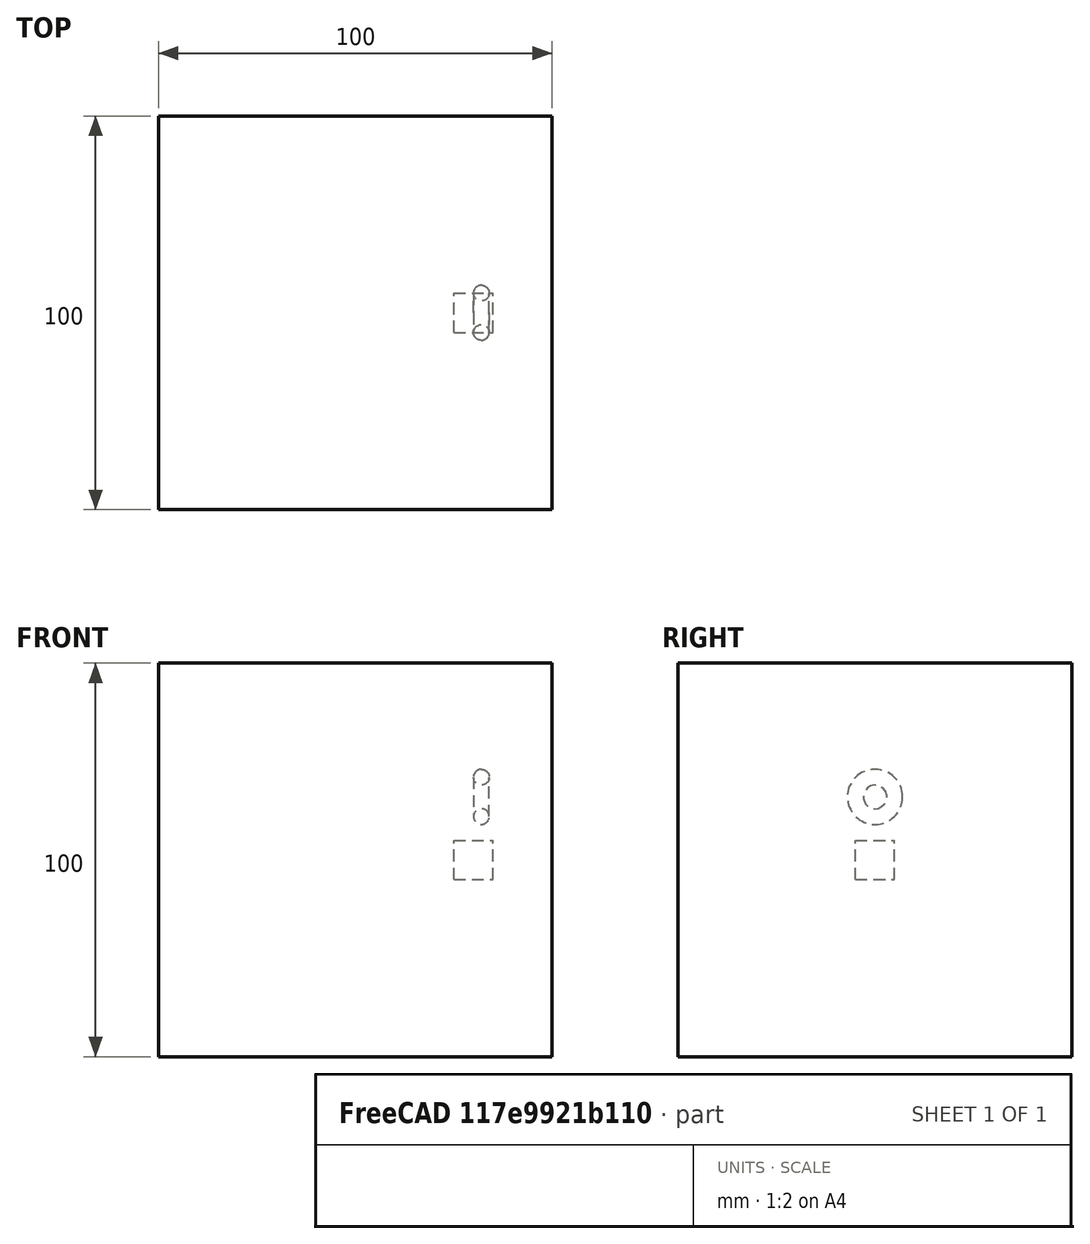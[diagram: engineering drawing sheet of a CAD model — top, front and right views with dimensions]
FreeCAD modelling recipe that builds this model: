
FCSTD DOCUMENT  (FreeCAD 0.20RUnknown)
Label: polarArray-7
License: All rights reserved
objects: App::DocumentObjectGroupPython×1251, Part::FeaturePython×4, App::Part×2, Part::MultiFuse×1
note: 4 computed .brp shape members not serialized (recipe doc carries the construction recipe); baked Part::Feature solids carry a one-line shape summary decoded from their .brp

FEATURE [App::DocumentObjectGroupPython] HALFPI  # scripted group (container) (typed FeaturePython)
  name = HALFPI
  value = pi/2.
FEATURE [App::DocumentObjectGroupPython] PI  # scripted group (container) (typed FeaturePython)
  name = PI
  value = 1.*pi
FEATURE [App::DocumentObjectGroupPython] TWOPI  # scripted group (container) (typed FeaturePython)
  name = TWOPI
  value = 2.*pi
FEATURE [App::DocumentObjectGroupPython] Constants  # scripted group (container) (typed FeaturePython)
  Group = -> [HALFPI,PI,TWOPI]
FEATURE [App::DocumentObjectGroupPython] Variables  # scripted group (container) (typed FeaturePython)
FEATURE [App::DocumentObjectGroupPython] Quantities  # scripted group (container) (typed FeaturePython)
FEATURE [App::DocumentObjectGroupPython] Isotopes  # scripted group (container) (typed FeaturePython)
FEATURE [App::DocumentObjectGroupPython] Elements  # scripted group (container) (typed FeaturePython)
FEATURE [App::DocumentObjectGroupPython] Matrix  # scripted group (container) (typed FeaturePython)
FEATURE [App::DocumentObjectGroupPython] Surfaces  # scripted group (container) (typed FeaturePython)
FEATURE [App::DocumentObjectGroupPython] Opticals  # scripted group (container) (typed FeaturePython)
  Group = -> [Matrix,Surfaces]
FEATURE [App::DocumentObjectGroupPython] G4Isotopes  # scripted group (container) (typed FeaturePython)
FEATURE [App::DocumentObjectGroupPython] H_element  # scripted group (container) (typed FeaturePython)
  Z = 1
  atom_value = 1.008
  formula = H
  name = H_element
FEATURE [App::DocumentObjectGroupPython] He_element  # scripted group (container) (typed FeaturePython)
  Z = 2
  atom_value = 4.0026
  formula = He
  name = He_element
FEATURE [App::DocumentObjectGroupPython] Li_element  # scripted group (container) (typed FeaturePython)
  Z = 3
  atom_value = 6.94
  formula = Li
  name = Li_element
FEATURE [App::DocumentObjectGroupPython] Be_element  # scripted group (container) (typed FeaturePython)
  Z = 4
  atom_value = 9.01218
  formula = Be
  name = Be_element
FEATURE [App::DocumentObjectGroupPython] B_element  # scripted group (container) (typed FeaturePython)
  Z = 5
  atom_value = 10.81
  formula = B
  name = B_element
FEATURE [App::DocumentObjectGroupPython] C_element  # scripted group (container) (typed FeaturePython)
  Z = 6
  atom_value = 12.011
  formula = C
  name = C_element
FEATURE [App::DocumentObjectGroupPython] N_element  # scripted group (container) (typed FeaturePython)
  Z = 7
  atom_value = 14.007
  formula = N
  name = N_element
FEATURE [App::DocumentObjectGroupPython] O_element  # scripted group (container) (typed FeaturePython)
  Z = 8
  atom_value = 15.999
  formula = O
  name = O_element
FEATURE [App::DocumentObjectGroupPython] F_element  # scripted group (container) (typed FeaturePython)
  Z = 9
  atom_value = 18.9984
  formula = F
  name = F_element
FEATURE [App::DocumentObjectGroupPython] Ne_element  # scripted group (container) (typed FeaturePython)
  Z = 10
  atom_value = 20.1797
  formula = Ne
  name = Ne_element
FEATURE [App::DocumentObjectGroupPython] Na_element  # scripted group (container) (typed FeaturePython)
  Z = 11
  atom_value = 22.9898
  formula = Na
  name = Na_element
FEATURE [App::DocumentObjectGroupPython] Mg_element  # scripted group (container) (typed FeaturePython)
  Z = 12
  atom_value = 24.305
  formula = Mg
  name = Mg_element
FEATURE [App::DocumentObjectGroupPython] Al_element  # scripted group (container) (typed FeaturePython)
  Z = 13
  atom_value = 26.9815
  formula = Al
  name = Al_element
FEATURE [App::DocumentObjectGroupPython] Si_element  # scripted group (container) (typed FeaturePython)
  Z = 14
  atom_value = 28.085
  formula = Si
  name = Si_element
FEATURE [App::DocumentObjectGroupPython] P_element  # scripted group (container) (typed FeaturePython)
  Z = 15
  atom_value = 30.9738
  formula = P
  name = P_element
FEATURE [App::DocumentObjectGroupPython] S_element  # scripted group (container) (typed FeaturePython)
  Z = 16
  atom_value = 32.06
  formula = S
  name = S_element
FEATURE [App::DocumentObjectGroupPython] Cl_element  # scripted group (container) (typed FeaturePython)
  Z = 17
  atom_value = 35.45
  formula = Cl
  name = Cl_element
FEATURE [App::DocumentObjectGroupPython] Ar_element  # scripted group (container) (typed FeaturePython)
  Z = 18
  atom_value = 39.95
  formula = Ar
  name = Ar_element
FEATURE [App::DocumentObjectGroupPython] K_element  # scripted group (container) (typed FeaturePython)
  Z = 19
  atom_value = 39.0983
  formula = K
  name = K_element
FEATURE [App::DocumentObjectGroupPython] Ca_element  # scripted group (container) (typed FeaturePython)
  Z = 20
  atom_value = 40.078
  formula = Ca
  name = Ca_element
FEATURE [App::DocumentObjectGroupPython] Sc_element  # scripted group (container) (typed FeaturePython)
  Z = 21
  atom_value = 44.9559
  formula = Sc
  name = Sc_element
FEATURE [App::DocumentObjectGroupPython] Ti_element  # scripted group (container) (typed FeaturePython)
  Z = 22
  atom_value = 47.867
  formula = Ti
  name = Ti_element
FEATURE [App::DocumentObjectGroupPython] V_element  # scripted group (container) (typed FeaturePython)
  Z = 23
  atom_value = 50.9415
  formula = V
  name = V_element
FEATURE [App::DocumentObjectGroupPython] Cr_element  # scripted group (container) (typed FeaturePython)
  Z = 24
  atom_value = 51.9961
  formula = Cr
  name = Cr_element
FEATURE [App::DocumentObjectGroupPython] Mn_element  # scripted group (container) (typed FeaturePython)
  Z = 25
  atom_value = 54.938
  formula = Mn
  name = Mn_element
FEATURE [App::DocumentObjectGroupPython] Fe_element  # scripted group (container) (typed FeaturePython)
  Z = 26
  atom_value = 55.845
  formula = Fe
  name = Fe_element
FEATURE [App::DocumentObjectGroupPython] Co_element  # scripted group (container) (typed FeaturePython)
  Z = 27
  atom_value = 58.9332
  formula = Co
  name = Co_element
FEATURE [App::DocumentObjectGroupPython] Ni_element  # scripted group (container) (typed FeaturePython)
  Z = 28
  atom_value = 58.6934
  formula = Ni
  name = Ni_element
FEATURE [App::DocumentObjectGroupPython] Cu_element  # scripted group (container) (typed FeaturePython)
  Z = 29
  atom_value = 63.546
  formula = Cu
  name = Cu_element
FEATURE [App::DocumentObjectGroupPython] Zn_element  # scripted group (container) (typed FeaturePython)
  Z = 30
  atom_value = 65.38
  formula = Zn
  name = Zn_element
FEATURE [App::DocumentObjectGroupPython] Ga_element  # scripted group (container) (typed FeaturePython)
  Z = 31
  atom_value = 69.723
  formula = Ga
  name = Ga_element
FEATURE [App::DocumentObjectGroupPython] Ge_element  # scripted group (container) (typed FeaturePython)
  Z = 32
  atom_value = 72.63
  formula = Ge
  name = Ge_element
FEATURE [App::DocumentObjectGroupPython] As_element  # scripted group (container) (typed FeaturePython)
  Z = 33
  atom_value = 74.9216
  formula = As
  name = As_element
FEATURE [App::DocumentObjectGroupPython] Se_element  # scripted group (container) (typed FeaturePython)
  Z = 34
  atom_value = 78.971
  formula = Se
  name = Se_element
FEATURE [App::DocumentObjectGroupPython] Br_element  # scripted group (container) (typed FeaturePython)
  Z = 35
  atom_value = 79.904
  formula = Br
  name = Br_element
FEATURE [App::DocumentObjectGroupPython] Kr_element  # scripted group (container) (typed FeaturePython)
  Z = 36
  atom_value = 83.798
  formula = Kr
  name = Kr_element
FEATURE [App::DocumentObjectGroupPython] Rb_element  # scripted group (container) (typed FeaturePython)
  Z = 37
  atom_value = 85.4678
  formula = Rb
  name = Rb_element
FEATURE [App::DocumentObjectGroupPython] Sr_element  # scripted group (container) (typed FeaturePython)
  Z = 38
  atom_value = 87.62
  formula = Sr
  name = Sr_element
FEATURE [App::DocumentObjectGroupPython] Y_element  # scripted group (container) (typed FeaturePython)
  Z = 39
  atom_value = 88.9058
  formula = Y
  name = Y_element
FEATURE [App::DocumentObjectGroupPython] Zr_element  # scripted group (container) (typed FeaturePython)
  Z = 40
  atom_value = 91.224
  formula = Zr
  name = Zr_element
FEATURE [App::DocumentObjectGroupPython] Nb_element  # scripted group (container) (typed FeaturePython)
  Z = 41
  atom_value = 92.9064
  formula = Nb
  name = Nb_element
FEATURE [App::DocumentObjectGroupPython] Mo_element  # scripted group (container) (typed FeaturePython)
  Z = 42
  atom_value = 95.95
  formula = Mo
  name = Mo_element
FEATURE [App::DocumentObjectGroupPython] Tc_element  # scripted group (container) (typed FeaturePython)
  Z = 43
  atom_value = 97
  formula = Tc
  name = Tc_element
FEATURE [App::DocumentObjectGroupPython] Ru_element  # scripted group (container) (typed FeaturePython)
  Z = 44
  atom_value = 101.07
  formula = Ru
  name = Ru_element
FEATURE [App::DocumentObjectGroupPython] Rh_element  # scripted group (container) (typed FeaturePython)
  Z = 45
  atom_value = 102.905
  formula = Rh
  name = Rh_element
FEATURE [App::DocumentObjectGroupPython] Pd_element  # scripted group (container) (typed FeaturePython)
  Z = 46
  atom_value = 106.42
  formula = Pd
  name = Pd_element
FEATURE [App::DocumentObjectGroupPython] Ag_element  # scripted group (container) (typed FeaturePython)
  Z = 47
  atom_value = 107.868
  formula = Ag
  name = Ag_element
FEATURE [App::DocumentObjectGroupPython] Cd_element  # scripted group (container) (typed FeaturePython)
  Z = 48
  atom_value = 112.414
  formula = Cd
  name = Cd_element
FEATURE [App::DocumentObjectGroupPython] In_element  # scripted group (container) (typed FeaturePython)
  Z = 49
  atom_value = 114.818
  formula = In
  name = In_element
FEATURE [App::DocumentObjectGroupPython] Sn_element  # scripted group (container) (typed FeaturePython)
  Z = 50
  atom_value = 118.71
  formula = Sn
  name = Sn_element
FEATURE [App::DocumentObjectGroupPython] Sb_element  # scripted group (container) (typed FeaturePython)
  Z = 51
  atom_value = 121.76
  formula = Sb
  name = Sb_element
FEATURE [App::DocumentObjectGroupPython] Te_element  # scripted group (container) (typed FeaturePython)
  Z = 52
  atom_value = 127.6
  formula = Te
  name = Te_element
FEATURE [App::DocumentObjectGroupPython] I_element  # scripted group (container) (typed FeaturePython)
  Z = 53
  atom_value = 126.904
  formula = I
  name = I_element
FEATURE [App::DocumentObjectGroupPython] Xe_element  # scripted group (container) (typed FeaturePython)
  Z = 54
  atom_value = 131.293
  formula = Xe
  name = Xe_element
FEATURE [App::DocumentObjectGroupPython] Cs_element  # scripted group (container) (typed FeaturePython)
  Z = 55
  atom_value = 132.905
  formula = Cs
  name = Cs_element
FEATURE [App::DocumentObjectGroupPython] Ba_element  # scripted group (container) (typed FeaturePython)
  Z = 56
  atom_value = 137.327
  formula = Ba
  name = Ba_element
FEATURE [App::DocumentObjectGroupPython] La_element  # scripted group (container) (typed FeaturePython)
  Z = 57
  atom_value = 138.905
  formula = La
  name = La_element
FEATURE [App::DocumentObjectGroupPython] Ce_element  # scripted group (container) (typed FeaturePython)
  Z = 58
  atom_value = 140.116
  formula = Ce
  name = Ce_element
FEATURE [App::DocumentObjectGroupPython] Pr_element  # scripted group (container) (typed FeaturePython)
  Z = 59
  atom_value = 140.908
  formula = Pr
  name = Pr_element
FEATURE [App::DocumentObjectGroupPython] Nd_element  # scripted group (container) (typed FeaturePython)
  Z = 60
  atom_value = 144.242
  formula = Nd
  name = Nd_element
FEATURE [App::DocumentObjectGroupPython] Pm_element  # scripted group (container) (typed FeaturePython)
  Z = 61
  atom_value = 145
  formula = Pm
  name = Pm_element
FEATURE [App::DocumentObjectGroupPython] Sm_element  # scripted group (container) (typed FeaturePython)
  Z = 62
  atom_value = 150.36
  formula = Sm
  name = Sm_element
FEATURE [App::DocumentObjectGroupPython] Eu_element  # scripted group (container) (typed FeaturePython)
  Z = 63
  atom_value = 151.964
  formula = Eu
  name = Eu_element
FEATURE [App::DocumentObjectGroupPython] Gd_element  # scripted group (container) (typed FeaturePython)
  Z = 64
  atom_value = 157.25
  formula = Gd
  name = Gd_element
FEATURE [App::DocumentObjectGroupPython] Tb_element  # scripted group (container) (typed FeaturePython)
  Z = 65
  atom_value = 158.925
  formula = Tb
  name = Tb_element
FEATURE [App::DocumentObjectGroupPython] Dy_element  # scripted group (container) (typed FeaturePython)
  Z = 66
  atom_value = 162.5
  formula = Dy
  name = Dy_element
FEATURE [App::DocumentObjectGroupPython] Ho_element  # scripted group (container) (typed FeaturePython)
  Z = 67
  atom_value = 164.93
  formula = Ho
  name = Ho_element
FEATURE [App::DocumentObjectGroupPython] Er_element  # scripted group (container) (typed FeaturePython)
  Z = 68
  atom_value = 167.259
  formula = Er
  name = Er_element
FEATURE [App::DocumentObjectGroupPython] Tm_element  # scripted group (container) (typed FeaturePython)
  Z = 69
  atom_value = 168.934
  formula = Tm
  name = Tm_element
FEATURE [App::DocumentObjectGroupPython] Yb_element  # scripted group (container) (typed FeaturePython)
  Z = 70
  atom_value = 173.045
  formula = Yb
  name = Yb_element
FEATURE [App::DocumentObjectGroupPython] Lu_element  # scripted group (container) (typed FeaturePython)
  Z = 71
  atom_value = 174.967
  formula = Lu
  name = Lu_element
FEATURE [App::DocumentObjectGroupPython] Hf_element  # scripted group (container) (typed FeaturePython)
  Z = 72
  atom_value = 178.49
  formula = Hf
  name = Hf_element
FEATURE [App::DocumentObjectGroupPython] Ta_element  # scripted group (container) (typed FeaturePython)
  Z = 73
  atom_value = 180.948
  formula = Ta
  name = Ta_element
FEATURE [App::DocumentObjectGroupPython] W_element  # scripted group (container) (typed FeaturePython)
  Z = 74
  atom_value = 183.84
  formula = W
  name = W_element
FEATURE [App::DocumentObjectGroupPython] Re_element  # scripted group (container) (typed FeaturePython)
  Z = 75
  atom_value = 186.207
  formula = Re
  name = Re_element
FEATURE [App::DocumentObjectGroupPython] Os_element  # scripted group (container) (typed FeaturePython)
  Z = 76
  atom_value = 190.23
  formula = Os
  name = Os_element
FEATURE [App::DocumentObjectGroupPython] Ir_element  # scripted group (container) (typed FeaturePython)
  Z = 77
  atom_value = 192.217
  formula = Ir
  name = Ir_element
FEATURE [App::DocumentObjectGroupPython] Pt_element  # scripted group (container) (typed FeaturePython)
  Z = 78
  atom_value = 195.084
  formula = Pt
  name = Pt_element
FEATURE [App::DocumentObjectGroupPython] Au_element  # scripted group (container) (typed FeaturePython)
  Z = 79
  atom_value = 196.967
  formula = Au
  name = Au_element
FEATURE [App::DocumentObjectGroupPython] Hg_element  # scripted group (container) (typed FeaturePython)
  Z = 80
  atom_value = 200.592
  formula = Hg
  name = Hg_element
FEATURE [App::DocumentObjectGroupPython] Tl_element  # scripted group (container) (typed FeaturePython)
  Z = 81
  atom_value = 204.38
  formula = Tl
  name = Tl_element
FEATURE [App::DocumentObjectGroupPython] Pb_element  # scripted group (container) (typed FeaturePython)
  Z = 82
  atom_value = 207.2
  formula = Pb
  name = Pb_element
FEATURE [App::DocumentObjectGroupPython] Bi_element  # scripted group (container) (typed FeaturePython)
  Z = 83
  atom_value = 208.98
  formula = Bi
  name = Bi_element
FEATURE [App::DocumentObjectGroupPython] Po_element  # scripted group (container) (typed FeaturePython)
  Z = 84
  atom_value = 209
  formula = Po
  name = Po_element
FEATURE [App::DocumentObjectGroupPython] At_element  # scripted group (container) (typed FeaturePython)
  Z = 85
  atom_value = 210
  formula = At
  name = At_element
FEATURE [App::DocumentObjectGroupPython] Rn_element  # scripted group (container) (typed FeaturePython)
  Z = 86
  atom_value = 222
  formula = Rn
  name = Rn_element
FEATURE [App::DocumentObjectGroupPython] Fr_element  # scripted group (container) (typed FeaturePython)
  Z = 87
  atom_value = 223
  formula = Fr
  name = Fr_element
FEATURE [App::DocumentObjectGroupPython] Ra_element  # scripted group (container) (typed FeaturePython)
  Z = 88
  atom_value = 226
  formula = Ra
  name = Ra_element
FEATURE [App::DocumentObjectGroupPython] Ac_element  # scripted group (container) (typed FeaturePython)
  Z = 89
  atom_value = 227
  formula = Ac
  name = Ac_element
FEATURE [App::DocumentObjectGroupPython] Th_element  # scripted group (container) (typed FeaturePython)
  Z = 90
  atom_value = 232.038
  formula = Th
  name = Th_element
FEATURE [App::DocumentObjectGroupPython] Pa_element  # scripted group (container) (typed FeaturePython)
  Z = 91
  atom_value = 231.036
  formula = Pa
  name = Pa_element
FEATURE [App::DocumentObjectGroupPython] U_element  # scripted group (container) (typed FeaturePython)
  Z = 92
  atom_value = 238.029
  formula = U
  name = U_element
FEATURE [App::DocumentObjectGroupPython] Np_element  # scripted group (container) (typed FeaturePython)
  Z = 93
  atom_value = 237
  formula = Np
  name = Np_element
FEATURE [App::DocumentObjectGroupPython] Pu_element  # scripted group (container) (typed FeaturePython)
  Z = 94
  atom_value = 244
  formula = Pu
  name = Pu_element
FEATURE [App::DocumentObjectGroupPython] Am_element  # scripted group (container) (typed FeaturePython)
  Z = 95
  atom_value = 243
  formula = Am
  name = Am_element
FEATURE [App::DocumentObjectGroupPython] Cm_element  # scripted group (container) (typed FeaturePython)
  Z = 96
  atom_value = 247
  formula = Cm
  name = Cm_element
FEATURE [App::DocumentObjectGroupPython] Bk_element  # scripted group (container) (typed FeaturePython)
  Z = 97
  atom_value = 247
  formula = Bk
  name = Bk_element
FEATURE [App::DocumentObjectGroupPython] Cf_element  # scripted group (container) (typed FeaturePython)
  Z = 98
  atom_value = 251
  formula = Cf
  name = Cf_element
FEATURE [App::DocumentObjectGroupPython] G4Elements  # scripted group (container) (typed FeaturePython)
  Group = -> [H_element,He_element,Li_element,Be_element,B_element,C_element,N_element,O_element,F_element,Ne_element,Na_element,Mg_element,Al_element,Si_element,P_element,S_element,Cl_element,Ar_element,K_element,Ca_element,Sc_element,Ti_element,V_element,Cr_element,Mn_element,Fe_element,Co_element,Ni_element,Cu_element,Zn_element,Ga_element,Ge_element,As_element,Se_element,Br_element,Kr_element,Rb_element,+61 more]
FEATURE [App::DocumentObjectGroupPython] H_element001  label="H_element : 0.101"  # scripted group (container) (typed FeaturePython)
  n = 0.101327
FEATURE [App::DocumentObjectGroupPython] C_element001  label="C_element : 0.775"  # scripted group (container) (typed FeaturePython)
  n = 0.7755
FEATURE [App::DocumentObjectGroupPython] N_element001  label="N_element : 0.035"  # scripted group (container) (typed FeaturePython)
  n = 0.035057
FEATURE [App::DocumentObjectGroupPython] O_element001  label="O_element : 0.052"  # scripted group (container) (typed FeaturePython)
  n = 0.0523159
FEATURE [App::DocumentObjectGroupPython] F_element001  label="F_element : 0.017"  # scripted group (container) (typed FeaturePython)
  n = 0.017422
FEATURE [App::DocumentObjectGroupPython] Ca_element001  label="Ca_element : 0.018"  # scripted group (container) (typed FeaturePython)
  n = 0.018378
FEATURE [App::DocumentObjectGroupPython] G4_A_150_TISSUE  label="G4_A-150_TISSUE"  # scripted group (container) (typed FeaturePython)
  Dunit = g/cm3
  Dvalue = 1.127
  Group = -> [H_element001,C_element001,N_element001,O_element001,F_element001,Ca_element001]
  conduct = 2
  density = 1
  expand = 3
  formula = G4_A-150_TISSUE
  name = G4_A-150_TISSUE
  specific = 4
FEATURE [App::DocumentObjectGroupPython] C_element002  label="C_element : 3"  # scripted group (container) (typed FeaturePython)
  n = 3
  ref = C_element
FEATURE [App::DocumentObjectGroupPython] H_element002  label="H_element : 6"  # scripted group (container) (typed FeaturePython)
  n = 6
  ref = H_element
FEATURE [App::DocumentObjectGroupPython] O_element002  label="O_element : 1"  # scripted group (container) (typed FeaturePython)
  n = 1
  ref = O_element
FEATURE [App::DocumentObjectGroupPython] G4_ACETONE  # scripted group (container) (typed FeaturePython)
  Dunit = g/cm3
  Dvalue = 0.7899
  Group = -> [C_element002,H_element002,O_element002]
  conduct = 2
  density = 1
  expand = 3
  formula = G4_ACETONE
  name = G4_ACETONE
  specific = 4
FEATURE [App::DocumentObjectGroupPython] C_element003  label="C_element : 2"  # scripted group (container) (typed FeaturePython)
  n = 2
  ref = C_element
FEATURE [App::DocumentObjectGroupPython] H_element003  label="H_element : 2"  # scripted group (container) (typed FeaturePython)
  n = 2
  ref = H_element
FEATURE [App::DocumentObjectGroupPython] G4_ACETYLENE  # scripted group (container) (typed FeaturePython)
  Dunit = g/cm3
  Dvalue = 0.0010967
  Group = -> [C_element003,H_element003]
  conduct = 2
  density = 1
  expand = 3
  formula = G4_ACETYLENE
  name = G4_ACETYLENE
  specific = 4
FEATURE [App::DocumentObjectGroupPython] C_element004  label="C_element : 5"  # scripted group (container) (typed FeaturePython)
  n = 5
  ref = C_element
FEATURE [App::DocumentObjectGroupPython] H_element004  label="H_element : 5"  # scripted group (container) (typed FeaturePython)
  n = 5
  ref = H_element
FEATURE [App::DocumentObjectGroupPython] N_element002  label="N_element : 5"  # scripted group (container) (typed FeaturePython)
  n = 5
  ref = N_element
FEATURE [App::DocumentObjectGroupPython] G4_ADENINE  # scripted group (container) (typed FeaturePython)
  Dunit = g/cm3
  Dvalue = 1.6
  Group = -> [C_element004,H_element004,N_element002]
  conduct = 2
  density = 1
  expand = 3
  formula = G4_ADENINE
  name = G4_ADENINE
  specific = 4
FEATURE [App::DocumentObjectGroupPython] H_element005  label="H_element : 0.114"  # scripted group (container) (typed FeaturePython)
  n = 0.114
FEATURE [App::DocumentObjectGroupPython] C_element005  label="C_element : 0.598"  # scripted group (container) (typed FeaturePython)
  n = 0.598
FEATURE [App::DocumentObjectGroupPython] N_element003  label="N_element : 0.007"  # scripted group (container) (typed FeaturePython)
  n = 0.007
FEATURE [App::DocumentObjectGroupPython] O_element003  label="O_element : 0.278"  # scripted group (container) (typed FeaturePython)
  n = 0.278
FEATURE [App::DocumentObjectGroupPython] Na_element001  label="Na_element : 0.001"  # scripted group (container) (typed FeaturePython)
  n = 0.001
FEATURE [App::DocumentObjectGroupPython] S_element001  label="S_element : 0.001"  # scripted group (container) (typed FeaturePython)
  n = 0.001
FEATURE [App::DocumentObjectGroupPython] Cl_element001  label="Cl_element : 0.001"  # scripted group (container) (typed FeaturePython)
  n = 0.001
FEATURE [App::DocumentObjectGroupPython] G4_ADIPOSE_TISSUE_ICRP  # scripted group (container) (typed FeaturePython)
  Dunit = g/cm3
  Dvalue = 0.95
  Group = -> [H_element005,C_element005,N_element003,O_element003,Na_element001,S_element001,Cl_element001]
  conduct = 2
  density = 1
  expand = 3
  formula = G4_ADIPOSE_TISSUE_ICRP
  name = G4_ADIPOSE_TISSUE_ICRP
  specific = 4
FEATURE [App::DocumentObjectGroupPython] C_element006  label="C_element : 0.000"  # scripted group (container) (typed FeaturePython)
  n = 0.000124
FEATURE [App::DocumentObjectGroupPython] N_element004  label="N_element : 0.755"  # scripted group (container) (typed FeaturePython)
  n = 0.755268
FEATURE [App::DocumentObjectGroupPython] O_element004  label="O_element : 0.232"  # scripted group (container) (typed FeaturePython)
  n = 0.231781
FEATURE [App::DocumentObjectGroupPython] Ar_element001  label="Ar_element : 0.013"  # scripted group (container) (typed FeaturePython)
  n = 0.012827
FEATURE [App::DocumentObjectGroupPython] G4_AIR  # scripted group (container) (typed FeaturePython)
  Dunit = g/cm3
  Dvalue = 0.00120479
  Group = -> [C_element006,N_element004,O_element004,Ar_element001]
  conduct = 2
  density = 1
  expand = 3
  formula = G4_AIR
  name = G4_AIR
  specific = 4
FEATURE [App::DocumentObjectGroupPython] C_element007  label="C_element : 006"  # scripted group (container) (typed FeaturePython)
  n = 3
  ref = C_element
FEATURE [App::DocumentObjectGroupPython] H_element006  label="H_element : 7"  # scripted group (container) (typed FeaturePython)
  n = 7
  ref = H_element
FEATURE [App::DocumentObjectGroupPython] N_element005  label="N_element : 1"  # scripted group (container) (typed FeaturePython)
  n = 1
  ref = N_element
FEATURE [App::DocumentObjectGroupPython] O_element005  label="O_element : 2"  # scripted group (container) (typed FeaturePython)
  n = 2
  ref = O_element
FEATURE [App::DocumentObjectGroupPython] G4_ALANINE  # scripted group (container) (typed FeaturePython)
  Dunit = g/cm3
  Dvalue = 1.42
  Group = -> [C_element007,H_element006,N_element005,O_element005]
  conduct = 2
  density = 1
  expand = 3
  formula = G4_ALANINE
  name = G4_ALANINE
  specific = 4
FEATURE [App::DocumentObjectGroupPython] Al_element001  label="Al_element : 2"  # scripted group (container) (typed FeaturePython)
  n = 2
  ref = Al_element
FEATURE [App::DocumentObjectGroupPython] O_element006  label="O_element : 3"  # scripted group (container) (typed FeaturePython)
  n = 3
  ref = O_element
FEATURE [App::DocumentObjectGroupPython] G4_ALUMINUM_OXIDE  # scripted group (container) (typed FeaturePython)
  Dunit = g/cm3
  Dvalue = 3.97
  Group = -> [Al_element001,O_element006]
  conduct = 2
  density = 1
  expand = 3
  formula = G4_ALUMINUM_OXIDE
  name = G4_ALUMINUM_OXIDE
  specific = 4
FEATURE [App::DocumentObjectGroupPython] H_element007  label="H_element : 0.106"  # scripted group (container) (typed FeaturePython)
  n = 0.10593
FEATURE [App::DocumentObjectGroupPython] C_element008  label="C_element : 0.789"  # scripted group (container) (typed FeaturePython)
  n = 0.788974
FEATURE [App::DocumentObjectGroupPython] O_element007  label="O_element : 0.105"  # scripted group (container) (typed FeaturePython)
  n = 0.105096
FEATURE [App::DocumentObjectGroupPython] G4_AMBER  # scripted group (container) (typed FeaturePython)
  Dunit = g/cm3
  Dvalue = 1.1
  Group = -> [H_element007,C_element008,O_element007]
  conduct = 2
  density = 1
  expand = 3
  formula = G4_AMBER
  name = G4_AMBER
  specific = 4
FEATURE [App::DocumentObjectGroupPython] N_element006  label="N_element : 006"  # scripted group (container) (typed FeaturePython)
  n = 1
  ref = N_element
FEATURE [App::DocumentObjectGroupPython] H_element008  label="H_element : 3"  # scripted group (container) (typed FeaturePython)
  n = 3
  ref = H_element
FEATURE [App::DocumentObjectGroupPython] G4_AMMONIA  # scripted group (container) (typed FeaturePython)
  Dunit = g/cm3
  Dvalue = 0.000826019
  Group = -> [N_element006,H_element008]
  conduct = 2
  density = 1
  expand = 3
  formula = G4_AMMONIA
  name = G4_AMMONIA
  specific = 4
FEATURE [App::DocumentObjectGroupPython] C_element009  label="C_element : 6"  # scripted group (container) (typed FeaturePython)
  n = 6
  ref = C_element
FEATURE [App::DocumentObjectGroupPython] H_element009  label="H_element : 008"  # scripted group (container) (typed FeaturePython)
  n = 7
  ref = H_element
FEATURE [App::DocumentObjectGroupPython] N_element007  label="N_element : 007"  # scripted group (container) (typed FeaturePython)
  n = 1
  ref = N_element
FEATURE [App::DocumentObjectGroupPython] G4_ANILINE  # scripted group (container) (typed FeaturePython)
  Dunit = g/cm3
  Dvalue = 1.0235
  Group = -> [C_element009,H_element009,N_element007]
  conduct = 2
  density = 1
  expand = 3
  formula = G4_ANILINE
  name = G4_ANILINE
  specific = 4
FEATURE [App::DocumentObjectGroupPython] C_element010  label="C_element : 14"  # scripted group (container) (typed FeaturePython)
  n = 14
  ref = C_element
FEATURE [App::DocumentObjectGroupPython] H_element010  label="H_element : 10"  # scripted group (container) (typed FeaturePython)
  n = 10
  ref = H_element
FEATURE [App::DocumentObjectGroupPython] G4_ANTHRACENE  # scripted group (container) (typed FeaturePython)
  Dunit = g/cm3
  Dvalue = 1.283
  Group = -> [C_element010,H_element010]
  conduct = 2
  density = 1
  expand = 3
  formula = G4_ANTHRACENE
  name = G4_ANTHRACENE
  specific = 4
FEATURE [App::DocumentObjectGroupPython] H_element011  label="H_element : 0.065"  # scripted group (container) (typed FeaturePython)
  n = 0.0654709
FEATURE [App::DocumentObjectGroupPython] C_element011  label="C_element : 0.537"  # scripted group (container) (typed FeaturePython)
  n = 0.536944
FEATURE [App::DocumentObjectGroupPython] N_element008  label="N_element : 0.021"  # scripted group (container) (typed FeaturePython)
  n = 0.0215
FEATURE [App::DocumentObjectGroupPython] O_element008  label="O_element : 0.032"  # scripted group (container) (typed FeaturePython)
  n = 0.032085
FEATURE [App::DocumentObjectGroupPython] F_element002  label="F_element : 0.167"  # scripted group (container) (typed FeaturePython)
  n = 0.167411
FEATURE [App::DocumentObjectGroupPython] Ca_element002  label="Ca_element : 0.177"  # scripted group (container) (typed FeaturePython)
  n = 0.176589
FEATURE [App::DocumentObjectGroupPython] G4_B_100_BONE  label="G4_B-100_BONE"  # scripted group (container) (typed FeaturePython)
  Dunit = g/cm3
  Dvalue = 1.45
  Group = -> [H_element011,C_element011,N_element008,O_element008,F_element002,Ca_element002]
  conduct = 2
  density = 1
  expand = 3
  formula = G4_B-100_BONE
  name = G4_B-100_BONE
  specific = 4
FEATURE [App::DocumentObjectGroupPython] H_element012  label="H_element : 0.057"  # scripted group (container) (typed FeaturePython)
  n = 0.057441
FEATURE [App::DocumentObjectGroupPython] C_element012  label="C_element : 0.790"  # scripted group (container) (typed FeaturePython)
  n = 0.774591
FEATURE [App::DocumentObjectGroupPython] O_element009  label="O_element : 0.168"  # scripted group (container) (typed FeaturePython)
  n = 0.167968
FEATURE [App::DocumentObjectGroupPython] G4_BAKELITE  # scripted group (container) (typed FeaturePython)
  Dunit = g/cm3
  Dvalue = 1.25
  Group = -> [H_element012,C_element012,O_element009]
  conduct = 2
  density = 1
  expand = 3
  formula = G4_BAKELITE
  name = G4_BAKELITE
  specific = 4
FEATURE [App::DocumentObjectGroupPython] Ba_element001  label="Ba_element : 1"  # scripted group (container) (typed FeaturePython)
  n = 1
  ref = Ba_element
FEATURE [App::DocumentObjectGroupPython] F_element003  label="F_element : 2"  # scripted group (container) (typed FeaturePython)
  n = 2
  ref = F_element
FEATURE [App::DocumentObjectGroupPython] G4_BARIUM_FLUORIDE  # scripted group (container) (typed FeaturePython)
  Dunit = g/cm3
  Dvalue = 4.89
  Group = -> [Ba_element001,F_element003]
  conduct = 2
  density = 1
  expand = 3
  formula = G4_BARIUM_FLUORIDE
  name = G4_BARIUM_FLUORIDE
  specific = 4
FEATURE [App::DocumentObjectGroupPython] Ba_element002  label="Ba_element : 002"  # scripted group (container) (typed FeaturePython)
  n = 1
  ref = Ba_element
FEATURE [App::DocumentObjectGroupPython] S_element002  label="S_element : 1"  # scripted group (container) (typed FeaturePython)
  n = 1
  ref = S_element
FEATURE [App::DocumentObjectGroupPython] O_element010  label="O_element : 4"  # scripted group (container) (typed FeaturePython)
  n = 4
  ref = O_element
FEATURE [App::DocumentObjectGroupPython] G4_BARIUM_SULFATE  # scripted group (container) (typed FeaturePython)
  Dunit = g/cm3
  Dvalue = 4.5
  Group = -> [Ba_element002,S_element002,O_element010]
  conduct = 2
  density = 1
  expand = 3
  formula = G4_BARIUM_SULFATE
  name = G4_BARIUM_SULFATE
  specific = 4
FEATURE [App::DocumentObjectGroupPython] C_element013  label="C_element : 007"  # scripted group (container) (typed FeaturePython)
  n = 6
  ref = C_element
FEATURE [App::DocumentObjectGroupPython] H_element013  label="H_element : 009"  # scripted group (container) (typed FeaturePython)
  n = 6
  ref = H_element
FEATURE [App::DocumentObjectGroupPython] G4_BENZENE  # scripted group (container) (typed FeaturePython)
  Dunit = g/cm3
  Dvalue = 0.87865
  Group = -> [C_element013,H_element013]
  conduct = 2
  density = 1
  expand = 3
  formula = G4_BENZENE
  name = G4_BENZENE
  specific = 4
FEATURE [App::DocumentObjectGroupPython] Be_element001  label="Be_element : 1"  # scripted group (container) (typed FeaturePython)
  n = 1
  ref = Be_element
FEATURE [App::DocumentObjectGroupPython] O_element011  label="O_element : 005"  # scripted group (container) (typed FeaturePython)
  n = 1
  ref = O_element
FEATURE [App::DocumentObjectGroupPython] G4_BERYLLIUM_OXIDE  # scripted group (container) (typed FeaturePython)
  Dunit = g/cm3
  Dvalue = 3.01
  Group = -> [Be_element001,O_element011]
  conduct = 2
  density = 1
  expand = 3
  formula = G4_BERYLLIUM_OXIDE
  name = G4_BERYLLIUM_OXIDE
  specific = 4
FEATURE [App::DocumentObjectGroupPython] Bi_element001  label="Bi_element : 4"  # scripted group (container) (typed FeaturePython)
  n = 4
  ref = Bi_element
FEATURE [App::DocumentObjectGroupPython] Ge_element001  label="Ge_element : 3"  # scripted group (container) (typed FeaturePython)
  n = 3
  ref = Ge_element
FEATURE [App::DocumentObjectGroupPython] O_element012  label="O_element : 12"  # scripted group (container) (typed FeaturePython)
  n = 12
  ref = O_element
FEATURE [App::DocumentObjectGroupPython] G4_BGO  # scripted group (container) (typed FeaturePython)
  Dunit = g/cm3
  Dvalue = 7.13
  Group = -> [Bi_element001,Ge_element001,O_element012]
  conduct = 2
  density = 1
  expand = 3
  formula = G4_BGO
  name = G4_BGO
  specific = 4
FEATURE [App::DocumentObjectGroupPython] H_element014  label="H_element : 0.102"  # scripted group (container) (typed FeaturePython)
  n = 0.102
FEATURE [App::DocumentObjectGroupPython] C_element014  label="C_element : 0.110"  # scripted group (container) (typed FeaturePython)
  n = 0.11
FEATURE [App::DocumentObjectGroupPython] N_element009  label="N_element : 0.033"  # scripted group (container) (typed FeaturePython)
  n = 0.033
FEATURE [App::DocumentObjectGroupPython] O_element013  label="O_element : 0.745"  # scripted group (container) (typed FeaturePython)
  n = 0.745
FEATURE [App::DocumentObjectGroupPython] Na_element002  label="Na_element : 0.002"  # scripted group (container) (typed FeaturePython)
  n = 0.001
FEATURE [App::DocumentObjectGroupPython] P_element001  label="P_element : 0.001"  # scripted group (container) (typed FeaturePython)
  n = 0.001
FEATURE [App::DocumentObjectGroupPython] S_element003  label="S_element : 0.002"  # scripted group (container) (typed FeaturePython)
  n = 0.002
FEATURE [App::DocumentObjectGroupPython] Cl_element002  label="Cl_element : 0.003"  # scripted group (container) (typed FeaturePython)
  n = 0.003
FEATURE [App::DocumentObjectGroupPython] K_element001  label="K_element : 0.002"  # scripted group (container) (typed FeaturePython)
  n = 0.002
FEATURE [App::DocumentObjectGroupPython] Fe_element001  label="Fe_element : 0.001"  # scripted group (container) (typed FeaturePython)
  n = 0.001
FEATURE [App::DocumentObjectGroupPython] G4_BLOOD_ICRP  # scripted group (container) (typed FeaturePython)
  Dunit = g/cm3
  Dvalue = 1.06
  Group = -> [H_element014,C_element014,N_element009,O_element013,Na_element002,P_element001,S_element003,Cl_element002,K_element001,Fe_element001]
  conduct = 2
  density = 1
  expand = 3
  formula = G4_BLOOD_ICRP
  name = G4_BLOOD_ICRP
  specific = 4
FEATURE [App::DocumentObjectGroupPython] H_element015  label="H_element : 0.064"  # scripted group (container) (typed FeaturePython)
  n = 0.064
FEATURE [App::DocumentObjectGroupPython] C_element015  label="C_element : 0.278"  # scripted group (container) (typed FeaturePython)
  n = 0.278
FEATURE [App::DocumentObjectGroupPython] N_element010  label="N_element : 0.027"  # scripted group (container) (typed FeaturePython)
  n = 0.027
FEATURE [App::DocumentObjectGroupPython] O_element014  label="O_element : 0.410"  # scripted group (container) (typed FeaturePython)
  n = 0.41
FEATURE [App::DocumentObjectGroupPython] Mg_element001  label="Mg_element : 0.002"  # scripted group (container) (typed FeaturePython)
  n = 0.002
FEATURE [App::DocumentObjectGroupPython] P_element002  label="P_element : 0.070"  # scripted group (container) (typed FeaturePython)
  n = 0.07
FEATURE [App::DocumentObjectGroupPython] S_element004  label="S_element : 0.003"  # scripted group (container) (typed FeaturePython)
  n = 0.002
FEATURE [App::DocumentObjectGroupPython] Ca_element003  label="Ca_element : 0.147"  # scripted group (container) (typed FeaturePython)
  n = 0.147
FEATURE [App::DocumentObjectGroupPython] G4_BONE_COMPACT_ICRU  # scripted group (container) (typed FeaturePython)
  Dunit = g/cm3
  Dvalue = 1.85
  Group = -> [H_element015,C_element015,N_element010,O_element014,Mg_element001,P_element002,S_element004,Ca_element003]
  conduct = 2
  density = 1
  expand = 3
  formula = G4_BONE_COMPACT_ICRU
  name = G4_BONE_COMPACT_ICRU
  specific = 4
FEATURE [App::DocumentObjectGroupPython] H_element016  label="H_element : 0.034"  # scripted group (container) (typed FeaturePython)
  n = 0.034
FEATURE [App::DocumentObjectGroupPython] C_element016  label="C_element : 0.155"  # scripted group (container) (typed FeaturePython)
  n = 0.155
FEATURE [App::DocumentObjectGroupPython] N_element011  label="N_element : 0.042"  # scripted group (container) (typed FeaturePython)
  n = 0.042
FEATURE [App::DocumentObjectGroupPython] O_element015  label="O_element : 0.435"  # scripted group (container) (typed FeaturePython)
  n = 0.435
FEATURE [App::DocumentObjectGroupPython] Na_element003  label="Na_element : 0.003"  # scripted group (container) (typed FeaturePython)
  n = 0.001
FEATURE [App::DocumentObjectGroupPython] Mg_element002  label="Mg_element : 0.003"  # scripted group (container) (typed FeaturePython)
  n = 0.002
FEATURE [App::DocumentObjectGroupPython] P_element003  label="P_element : 0.103"  # scripted group (container) (typed FeaturePython)
  n = 0.103
FEATURE [App::DocumentObjectGroupPython] S_element005  label="S_element : 0.004"  # scripted group (container) (typed FeaturePython)
  n = 0.003
FEATURE [App::DocumentObjectGroupPython] Ca_element004  label="Ca_element : 0.225"  # scripted group (container) (typed FeaturePython)
  n = 0.225
FEATURE [App::DocumentObjectGroupPython] G4_BONE_CORTICAL_ICRP  # scripted group (container) (typed FeaturePython)
  Dunit = g/cm3
  Dvalue = 1.92
  Group = -> [H_element016,C_element016,N_element011,O_element015,Na_element003,Mg_element002,P_element003,S_element005,Ca_element004]
  conduct = 2
  density = 1
  expand = 3
  formula = G4_BONE_CORTICAL_ICRP
  name = G4_BONE_CORTICAL_ICRP
  specific = 4
FEATURE [App::DocumentObjectGroupPython] B_element001  label="B_element : 4"  # scripted group (container) (typed FeaturePython)
  n = 4
  ref = B_element
FEATURE [App::DocumentObjectGroupPython] C_element017  label="C_element : 1"  # scripted group (container) (typed FeaturePython)
  n = 1
  ref = C_element
FEATURE [App::DocumentObjectGroupPython] G4_BORON_CARBIDE  # scripted group (container) (typed FeaturePython)
  Dunit = g/cm3
  Dvalue = 2.52
  Group = -> [B_element001,C_element017]
  conduct = 2
  density = 1
  expand = 3
  formula = G4_BORON_CARBIDE
  name = G4_BORON_CARBIDE
  specific = 4
FEATURE [App::DocumentObjectGroupPython] B_element002  label="B_element : 2"  # scripted group (container) (typed FeaturePython)
  n = 2
  ref = B_element
FEATURE [App::DocumentObjectGroupPython] O_element016  label="O_element : 006"  # scripted group (container) (typed FeaturePython)
  n = 3
  ref = O_element
FEATURE [App::DocumentObjectGroupPython] G4_BORON_OXIDE  # scripted group (container) (typed FeaturePython)
  Dunit = g/cm3
  Dvalue = 1.812
  Group = -> [B_element002,O_element016]
  conduct = 2
  density = 1
  expand = 3
  formula = G4_BORON_OXIDE
  name = G4_BORON_OXIDE
  specific = 4
FEATURE [App::DocumentObjectGroupPython] H_element017  label="H_element : 0.107"  # scripted group (container) (typed FeaturePython)
  n = 0.107
FEATURE [App::DocumentObjectGroupPython] C_element018  label="C_element : 0.145"  # scripted group (container) (typed FeaturePython)
  n = 0.145
FEATURE [App::DocumentObjectGroupPython] N_element012  label="N_element : 0.022"  # scripted group (container) (typed FeaturePython)
  n = 0.022
FEATURE [App::DocumentObjectGroupPython] O_element017  label="O_element : 0.712"  # scripted group (container) (typed FeaturePython)
  n = 0.712
FEATURE [App::DocumentObjectGroupPython] Na_element004  label="Na_element : 0.004"  # scripted group (container) (typed FeaturePython)
  n = 0.002
FEATURE [App::DocumentObjectGroupPython] P_element004  label="P_element : 0.004"  # scripted group (container) (typed FeaturePython)
  n = 0.004
FEATURE [App::DocumentObjectGroupPython] S_element006  label="S_element : 0.005"  # scripted group (container) (typed FeaturePython)
  n = 0.002
FEATURE [App::DocumentObjectGroupPython] Cl_element003  label="Cl_element : 0.004"  # scripted group (container) (typed FeaturePython)
  n = 0.003
FEATURE [App::DocumentObjectGroupPython] K_element002  label="K_element : 0.003"  # scripted group (container) (typed FeaturePython)
  n = 0.003
FEATURE [App::DocumentObjectGroupPython] G4_BRAIN_ICRP  # scripted group (container) (typed FeaturePython)
  Dunit = g/cm3
  Dvalue = 1.04
  Group = -> [H_element017,C_element018,N_element012,O_element017,Na_element004,P_element004,S_element006,Cl_element003,K_element002]
  conduct = 2
  density = 1
  expand = 3
  formula = G4_BRAIN_ICRP
  name = G4_BRAIN_ICRP
  specific = 4
FEATURE [App::DocumentObjectGroupPython] C_element019  label="C_element : 4"  # scripted group (container) (typed FeaturePython)
  n = 4
  ref = C_element
FEATURE [App::DocumentObjectGroupPython] H_element018  label="H_element : 010"  # scripted group (container) (typed FeaturePython)
  n = 10
  ref = H_element
FEATURE [App::DocumentObjectGroupPython] G4_BUTANE  # scripted group (container) (typed FeaturePython)
  Dunit = g/cm3
  Dvalue = 0.00249343
  Group = -> [C_element019,H_element018]
  conduct = 2
  density = 1
  expand = 3
  formula = G4_BUTANE
  name = G4_BUTANE
  specific = 4
FEATURE [App::DocumentObjectGroupPython] C_element020  label="C_element : 008"  # scripted group (container) (typed FeaturePython)
  n = 4
  ref = C_element
FEATURE [App::DocumentObjectGroupPython] H_element019  label="H_element : 011"  # scripted group (container) (typed FeaturePython)
  n = 10
  ref = H_element
FEATURE [App::DocumentObjectGroupPython] O_element018  label="O_element : 007"  # scripted group (container) (typed FeaturePython)
  n = 1
  ref = O_element
FEATURE [App::DocumentObjectGroupPython] G4_N_BUTYL_ALCOHOL  label="G4_N-BUTYL_ALCOHOL"  # scripted group (container) (typed FeaturePython)
  Dunit = g/cm3
  Dvalue = 0.8098
  Group = -> [C_element020,H_element019,O_element018]
  conduct = 2
  density = 1
  expand = 3
  formula = G4_N-BUTYL_ALCOHOL
  name = G4_N-BUTYL_ALCOHOL
  specific = 4
FEATURE [App::DocumentObjectGroupPython] H_element020  label="H_element : 0.025"  # scripted group (container) (typed FeaturePython)
  n = 0.02468
FEATURE [App::DocumentObjectGroupPython] C_element021  label="C_element : 0.502"  # scripted group (container) (typed FeaturePython)
  n = 0.501611
FEATURE [App::DocumentObjectGroupPython] O_element019  label="O_element : 0.005"  # scripted group (container) (typed FeaturePython)
  n = 0.004527
FEATURE [App::DocumentObjectGroupPython] F_element004  label="F_element : 0.465"  # scripted group (container) (typed FeaturePython)
  n = 0.465209
FEATURE [App::DocumentObjectGroupPython] Si_element001  label="Si_element : 0.004"  # scripted group (container) (typed FeaturePython)
  n = 0.003973
FEATURE [App::DocumentObjectGroupPython] G4_C_552  label="G4_C-552"  # scripted group (container) (typed FeaturePython)
  Dunit = g/cm3
  Dvalue = 1.76
  Group = -> [H_element020,C_element021,O_element019,F_element004,Si_element001]
  conduct = 2
  density = 1
  expand = 3
  formula = G4_C-552
  name = G4_C-552
  specific = 4
FEATURE [App::DocumentObjectGroupPython] Cd_element001  label="Cd_element : 1"  # scripted group (container) (typed FeaturePython)
  n = 1
  ref = Cd_element
FEATURE [App::DocumentObjectGroupPython] Te_element001  label="Te_element : 1"  # scripted group (container) (typed FeaturePython)
  n = 1
  ref = Te_element
FEATURE [App::DocumentObjectGroupPython] G4_CADMIUM_TELLURIDE  # scripted group (container) (typed FeaturePython)
  Dunit = g/cm3
  Dvalue = 6.2
  Group = -> [Cd_element001,Te_element001]
  conduct = 2
  density = 1
  expand = 3
  formula = G4_CADMIUM_TELLURIDE
  name = G4_CADMIUM_TELLURIDE
  specific = 4
FEATURE [App::DocumentObjectGroupPython] Cd_element002  label="Cd_element : 002"  # scripted group (container) (typed FeaturePython)
  n = 1
  ref = Cd_element
FEATURE [App::DocumentObjectGroupPython] W_element001  label="W_element : 1"  # scripted group (container) (typed FeaturePython)
  n = 1
  ref = W_element
FEATURE [App::DocumentObjectGroupPython] O_element020  label="O_element : 008"  # scripted group (container) (typed FeaturePython)
  n = 4
  ref = O_element
FEATURE [App::DocumentObjectGroupPython] G4_CADMIUM_TUNGSTATE  # scripted group (container) (typed FeaturePython)
  Dunit = g/cm3
  Dvalue = 7.9
  Group = -> [Cd_element002,W_element001,O_element020]
  conduct = 2
  density = 1
  expand = 3
  formula = G4_CADMIUM_TUNGSTATE
  name = G4_CADMIUM_TUNGSTATE
  specific = 4
FEATURE [App::DocumentObjectGroupPython] Ca_element005  label="Ca_element : 1"  # scripted group (container) (typed FeaturePython)
  n = 1
  ref = Ca_element
FEATURE [App::DocumentObjectGroupPython] C_element022  label="C_element : 009"  # scripted group (container) (typed FeaturePython)
  n = 1
  ref = C_element
FEATURE [App::DocumentObjectGroupPython] O_element021  label="O_element : 009"  # scripted group (container) (typed FeaturePython)
  n = 3
  ref = O_element
FEATURE [App::DocumentObjectGroupPython] G4_CALCIUM_CARBONATE  # scripted group (container) (typed FeaturePython)
  Dunit = g/cm3
  Dvalue = 2.8
  Group = -> [Ca_element005,C_element022,O_element021]
  conduct = 2
  density = 1
  expand = 3
  formula = G4_CALCIUM_CARBONATE
  name = G4_CALCIUM_CARBONATE
  specific = 4
FEATURE [App::DocumentObjectGroupPython] Ca_element006  label="Ca_element : 002"  # scripted group (container) (typed FeaturePython)
  n = 1
  ref = Ca_element
FEATURE [App::DocumentObjectGroupPython] F_element005  label="F_element : 003"  # scripted group (container) (typed FeaturePython)
  n = 2
  ref = F_element
FEATURE [App::DocumentObjectGroupPython] G4_CALCIUM_FLUORIDE  # scripted group (container) (typed FeaturePython)
  Dunit = g/cm3
  Dvalue = 3.18
  Group = -> [Ca_element006,F_element005]
  conduct = 2
  density = 1
  expand = 3
  formula = G4_CALCIUM_FLUORIDE
  name = G4_CALCIUM_FLUORIDE
  specific = 4
FEATURE [App::DocumentObjectGroupPython] Ca_element007  label="Ca_element : 003"  # scripted group (container) (typed FeaturePython)
  n = 1
  ref = Ca_element
FEATURE [App::DocumentObjectGroupPython] O_element022  label="O_element : 010"  # scripted group (container) (typed FeaturePython)
  n = 1
  ref = O_element
FEATURE [App::DocumentObjectGroupPython] G4_CALCIUM_OXIDE  # scripted group (container) (typed FeaturePython)
  Dunit = g/cm3
  Dvalue = 3.3
  Group = -> [Ca_element007,O_element022]
  conduct = 2
  density = 1
  expand = 3
  formula = G4_CALCIUM_OXIDE
  name = G4_CALCIUM_OXIDE
  specific = 4
FEATURE [App::DocumentObjectGroupPython] Ca_element008  label="Ca_element : 004"  # scripted group (container) (typed FeaturePython)
  n = 1
  ref = Ca_element
FEATURE [App::DocumentObjectGroupPython] S_element007  label="S_element : 002"  # scripted group (container) (typed FeaturePython)
  n = 1
  ref = S_element
FEATURE [App::DocumentObjectGroupPython] O_element023  label="O_element : 011"  # scripted group (container) (typed FeaturePython)
  n = 4
  ref = O_element
FEATURE [App::DocumentObjectGroupPython] G4_CALCIUM_SULFATE  # scripted group (container) (typed FeaturePython)
  Dunit = g/cm3
  Dvalue = 2.96
  Group = -> [Ca_element008,S_element007,O_element023]
  conduct = 2
  density = 1
  expand = 3
  formula = G4_CALCIUM_SULFATE
  name = G4_CALCIUM_SULFATE
  specific = 4
FEATURE [App::DocumentObjectGroupPython] Ca_element009  label="Ca_element : 005"  # scripted group (container) (typed FeaturePython)
  n = 1
  ref = Ca_element
FEATURE [App::DocumentObjectGroupPython] W_element002  label="W_element : 002"  # scripted group (container) (typed FeaturePython)
  n = 1
  ref = W_element
FEATURE [App::DocumentObjectGroupPython] O_element024  label="O_element : 012"  # scripted group (container) (typed FeaturePython)
  n = 4
  ref = O_element
FEATURE [App::DocumentObjectGroupPython] G4_CALCIUM_TUNGSTATE  # scripted group (container) (typed FeaturePython)
  Dunit = g/cm3
  Dvalue = 6.062
  Group = -> [Ca_element009,W_element002,O_element024]
  conduct = 2
  density = 1
  expand = 3
  formula = G4_CALCIUM_TUNGSTATE
  name = G4_CALCIUM_TUNGSTATE
  specific = 4
FEATURE [App::DocumentObjectGroupPython] C_element023  label="C_element : 010"  # scripted group (container) (typed FeaturePython)
  n = 1
  ref = C_element
FEATURE [App::DocumentObjectGroupPython] O_element025  label="O_element : 013"  # scripted group (container) (typed FeaturePython)
  n = 2
  ref = O_element
FEATURE [App::DocumentObjectGroupPython] G4_CARBON_DIOXIDE  # scripted group (container) (typed FeaturePython)
  Dunit = g/cm3
  Dvalue = 0.00184212
  Group = -> [C_element023,O_element025]
  conduct = 2
  density = 1
  expand = 3
  formula = G4_CARBON_DIOXIDE
  name = G4_CARBON_DIOXIDE
  specific = 4
FEATURE [App::DocumentObjectGroupPython] C_element024  label="C_element : 011"  # scripted group (container) (typed FeaturePython)
  n = 1
  ref = C_element
FEATURE [App::DocumentObjectGroupPython] Cl_element004  label="Cl_element : 4"  # scripted group (container) (typed FeaturePython)
  n = 4
  ref = Cl_element
FEATURE [App::DocumentObjectGroupPython] G4_CARBON_TETRACHLORIDE  # scripted group (container) (typed FeaturePython)
  Dunit = g/cm3
  Dvalue = 1.594
  Group = -> [C_element024,Cl_element004]
  conduct = 2
  density = 1
  expand = 3
  formula = G4_CARBON_TETRACHLORIDE
  name = G4_CARBON_TETRACHLORIDE
  specific = 4
FEATURE [App::DocumentObjectGroupPython] C_element025  label="C_element : 012"  # scripted group (container) (typed FeaturePython)
  n = 6
  ref = C_element
FEATURE [App::DocumentObjectGroupPython] H_element021  label="H_element : 012"  # scripted group (container) (typed FeaturePython)
  n = 10
  ref = H_element
FEATURE [App::DocumentObjectGroupPython] O_element026  label="O_element : 5"  # scripted group (container) (typed FeaturePython)
  n = 5
  ref = O_element
FEATURE [App::DocumentObjectGroupPython] G4_CELLULOSE_CELLOPHANE  # scripted group (container) (typed FeaturePython)
  Dunit = g/cm3
  Dvalue = 1.42
  Group = -> [C_element025,H_element021,O_element026]
  conduct = 2
  density = 1
  expand = 3
  formula = G4_CELLULOSE_CELLOPHANE
  name = G4_CELLULOSE_CELLOPHANE
  specific = 4
FEATURE [App::DocumentObjectGroupPython] H_element022  label="H_element : 0.067"  # scripted group (container) (typed FeaturePython)
  n = 0.067125
FEATURE [App::DocumentObjectGroupPython] C_element026  label="C_element : 0.545"  # scripted group (container) (typed FeaturePython)
  n = 0.545403
FEATURE [App::DocumentObjectGroupPython] O_element027  label="O_element : 0.387"  # scripted group (container) (typed FeaturePython)
  n = 0.387472
FEATURE [App::DocumentObjectGroupPython] G4_CELLULOSE_BUTYRATE  # scripted group (container) (typed FeaturePython)
  Dunit = g/cm3
  Dvalue = 1.2
  Group = -> [H_element022,C_element026,O_element027]
  conduct = 2
  density = 1
  expand = 3
  formula = G4_CELLULOSE_BUTYRATE
  name = G4_CELLULOSE_BUTYRATE
  specific = 4
FEATURE [App::DocumentObjectGroupPython] H_element023  label="H_element : 0.029"  # scripted group (container) (typed FeaturePython)
  n = 0.029216
FEATURE [App::DocumentObjectGroupPython] C_element027  label="C_element : 0.271"  # scripted group (container) (typed FeaturePython)
  n = 0.271296
FEATURE [App::DocumentObjectGroupPython] N_element013  label="N_element : 0.121"  # scripted group (container) (typed FeaturePython)
  n = 0.121276
FEATURE [App::DocumentObjectGroupPython] O_element028  label="O_element : 0.578"  # scripted group (container) (typed FeaturePython)
  n = 0.578212
FEATURE [App::DocumentObjectGroupPython] G4_CELLULOSE_NITRATE  # scripted group (container) (typed FeaturePython)
  Dunit = g/cm3
  Dvalue = 1.49
  Group = -> [H_element023,C_element027,N_element013,O_element028]
  conduct = 2
  density = 1
  expand = 3
  formula = G4_CELLULOSE_NITRATE
  name = G4_CELLULOSE_NITRATE
  specific = 4
FEATURE [App::DocumentObjectGroupPython] H_element024  label="H_element : 0.108"  # scripted group (container) (typed FeaturePython)
  n = 0.107596
FEATURE [App::DocumentObjectGroupPython] N_element014  label="N_element : 0.001"  # scripted group (container) (typed FeaturePython)
  n = 0.0008
FEATURE [App::DocumentObjectGroupPython] O_element029  label="O_element : 0.875"  # scripted group (container) (typed FeaturePython)
  n = 0.874976
FEATURE [App::DocumentObjectGroupPython] S_element008  label="S_element : 0.015"  # scripted group (container) (typed FeaturePython)
  n = 0.014627
FEATURE [App::DocumentObjectGroupPython] Ce_element001  label="Ce_element : 0.002"  # scripted group (container) (typed FeaturePython)
  n = 0.002001
FEATURE [App::DocumentObjectGroupPython] G4_CERIC_SULFATE  # scripted group (container) (typed FeaturePython)
  Dunit = g/cm3
  Dvalue = 1.03
  Group = -> [H_element024,N_element014,O_element029,S_element008,Ce_element001]
  conduct = 2
  density = 1
  expand = 3
  formula = G4_CERIC_SULFATE
  name = G4_CERIC_SULFATE
  specific = 4
FEATURE [App::DocumentObjectGroupPython] Cs_element001  label="Cs_element : 1"  # scripted group (container) (typed FeaturePython)
  n = 1
  ref = Cs_element
FEATURE [App::DocumentObjectGroupPython] F_element006  label="F_element : 1"  # scripted group (container) (typed FeaturePython)
  n = 1
  ref = F_element
FEATURE [App::DocumentObjectGroupPython] G4_CESIUM_FLUORIDE  # scripted group (container) (typed FeaturePython)
  Dunit = g/cm3
  Dvalue = 4.115
  Group = -> [Cs_element001,F_element006]
  conduct = 2
  density = 1
  expand = 3
  formula = G4_CESIUM_FLUORIDE
  name = G4_CESIUM_FLUORIDE
  specific = 4
FEATURE [App::DocumentObjectGroupPython] Cs_element002  label="Cs_element : 002"  # scripted group (container) (typed FeaturePython)
  n = 1
  ref = Cs_element
FEATURE [App::DocumentObjectGroupPython] I_element001  label="I_element : 1"  # scripted group (container) (typed FeaturePython)
  n = 1
  ref = I_element
FEATURE [App::DocumentObjectGroupPython] G4_CESIUM_IODIDE  # scripted group (container) (typed FeaturePython)
  Dunit = g/cm3
  Dvalue = 4.51
  Group = -> [Cs_element002,I_element001]
  conduct = 2
  density = 1
  expand = 3
  formula = G4_CESIUM_IODIDE
  name = G4_CESIUM_IODIDE
  specific = 4
FEATURE [App::DocumentObjectGroupPython] C_element028  label="C_element : 013"  # scripted group (container) (typed FeaturePython)
  n = 6
  ref = C_element
FEATURE [App::DocumentObjectGroupPython] H_element025  label="H_element : 013"  # scripted group (container) (typed FeaturePython)
  n = 5
  ref = H_element
FEATURE [App::DocumentObjectGroupPython] Cl_element005  label="Cl_element : 1"  # scripted group (container) (typed FeaturePython)
  n = 1
  ref = Cl_element
FEATURE [App::DocumentObjectGroupPython] G4_CHLOROBENZENE  # scripted group (container) (typed FeaturePython)
  Dunit = g/cm3
  Dvalue = 1.1058
  Group = -> [C_element028,H_element025,Cl_element005]
  conduct = 2
  density = 1
  expand = 3
  formula = G4_CHLOROBENZENE
  name = G4_CHLOROBENZENE
  specific = 4
FEATURE [App::DocumentObjectGroupPython] C_element029  label="C_element : 014"  # scripted group (container) (typed FeaturePython)
  n = 1
  ref = C_element
FEATURE [App::DocumentObjectGroupPython] H_element026  label="H_element : 1"  # scripted group (container) (typed FeaturePython)
  n = 1
  ref = H_element
FEATURE [App::DocumentObjectGroupPython] Cl_element006  label="Cl_element : 3"  # scripted group (container) (typed FeaturePython)
  n = 3
  ref = Cl_element
FEATURE [App::DocumentObjectGroupPython] G4_CHLOROFORM  # scripted group (container) (typed FeaturePython)
  Dunit = g/cm3
  Dvalue = 1.4832
  Group = -> [C_element029,H_element026,Cl_element006]
  conduct = 2
  density = 1
  expand = 3
  formula = G4_CHLOROFORM
  name = G4_CHLOROFORM
  specific = 4
FEATURE [App::DocumentObjectGroupPython] H_element027  label="H_element : 0.010"  # scripted group (container) (typed FeaturePython)
  n = 0.01
FEATURE [App::DocumentObjectGroupPython] C_element030  label="C_element : 0.001"  # scripted group (container) (typed FeaturePython)
  n = 0.001
FEATURE [App::DocumentObjectGroupPython] O_element030  label="O_element : 0.529"  # scripted group (container) (typed FeaturePython)
  n = 0.529107
FEATURE [App::DocumentObjectGroupPython] Na_element005  label="Na_element : 0.016"  # scripted group (container) (typed FeaturePython)
  n = 0.016
FEATURE [App::DocumentObjectGroupPython] Mg_element003  label="Mg_element : 0.004"  # scripted group (container) (typed FeaturePython)
  n = 0.002
FEATURE [App::DocumentObjectGroupPython] Al_element002  label="Al_element : 0.034"  # scripted group (container) (typed FeaturePython)
  n = 0.033872
FEATURE [App::DocumentObjectGroupPython] Si_element002  label="Si_element : 0.337"  # scripted group (container) (typed FeaturePython)
  n = 0.337021
FEATURE [App::DocumentObjectGroupPython] K_element003  label="K_element : 0.013"  # scripted group (container) (typed FeaturePython)
  n = 0.013
FEATURE [App::DocumentObjectGroupPython] Ca_element010  label="Ca_element : 0.044"  # scripted group (container) (typed FeaturePython)
  n = 0.044
FEATURE [App::DocumentObjectGroupPython] Fe_element002  label="Fe_element : 0.014"  # scripted group (container) (typed FeaturePython)
  n = 0.014
FEATURE [App::DocumentObjectGroupPython] G4_CONCRETE  # scripted group (container) (typed FeaturePython)
  Dunit = g/cm3
  Dvalue = 2.3
  Group = -> [H_element027,C_element030,O_element030,Na_element005,Mg_element003,Al_element002,Si_element002,K_element003,Ca_element010,Fe_element002]
  conduct = 2
  density = 1
  expand = 3
  formula = G4_CONCRETE
  name = G4_CONCRETE
  specific = 4
FEATURE [App::DocumentObjectGroupPython] C_element031  label="C_element : 015"  # scripted group (container) (typed FeaturePython)
  n = 6
  ref = C_element
FEATURE [App::DocumentObjectGroupPython] H_element028  label="H_element : 12"  # scripted group (container) (typed FeaturePython)
  n = 12
  ref = H_element
FEATURE [App::DocumentObjectGroupPython] G4_CYCLOHEXANE  # scripted group (container) (typed FeaturePython)
  Dunit = g/cm3
  Dvalue = 0.779
  Group = -> [C_element031,H_element028]
  conduct = 2
  density = 1
  expand = 3
  formula = G4_CYCLOHEXANE
  name = G4_CYCLOHEXANE
  specific = 4
FEATURE [App::DocumentObjectGroupPython] C_element032  label="C_element : 016"  # scripted group (container) (typed FeaturePython)
  n = 6
  ref = C_element
FEATURE [App::DocumentObjectGroupPython] H_element029  label="H_element : 4"  # scripted group (container) (typed FeaturePython)
  n = 4
  ref = H_element
FEATURE [App::DocumentObjectGroupPython] Cl_element007  label="Cl_element : 2"  # scripted group (container) (typed FeaturePython)
  n = 2
  ref = Cl_element
FEATURE [App::DocumentObjectGroupPython] G4_1_2_DICHLOROBENZENE  label="G4_1.2-DICHLOROBENZENE"  # scripted group (container) (typed FeaturePython)
  Dunit = g/cm3
  Dvalue = 1.3048
  Group = -> [C_element032,H_element029,Cl_element007]
  conduct = 2
  density = 1
  expand = 3
  formula = G4_1.2-DICHLOROBENZENE
  name = G4_1.2-DICHLOROBENZENE
  specific = 4
FEATURE [App::DocumentObjectGroupPython] C_element033  label="C_element : 017"  # scripted group (container) (typed FeaturePython)
  n = 4
  ref = C_element
FEATURE [App::DocumentObjectGroupPython] H_element030  label="H_element : 8"  # scripted group (container) (typed FeaturePython)
  n = 8
  ref = H_element
FEATURE [App::DocumentObjectGroupPython] O_element031  label="O_element : 014"  # scripted group (container) (typed FeaturePython)
  n = 1
  ref = O_element
FEATURE [App::DocumentObjectGroupPython] Cl_element008  label="Cl_element : 005"  # scripted group (container) (typed FeaturePython)
  n = 2
  ref = Cl_element
FEATURE [App::DocumentObjectGroupPython] G4_DICHLORODIETHYL_ETHER  # scripted group (container) (typed FeaturePython)
  Dunit = g/cm3
  Dvalue = 1.2199
  Group = -> [C_element033,H_element030,O_element031,Cl_element008]
  conduct = 2
  density = 1
  expand = 3
  formula = G4_DICHLORODIETHYL_ETHER
  name = G4_DICHLORODIETHYL_ETHER
  specific = 4
FEATURE [App::DocumentObjectGroupPython] C_element034  label="C_element : 018"  # scripted group (container) (typed FeaturePython)
  n = 2
  ref = C_element
FEATURE [App::DocumentObjectGroupPython] H_element031  label="H_element : 014"  # scripted group (container) (typed FeaturePython)
  n = 4
  ref = H_element
FEATURE [App::DocumentObjectGroupPython] Cl_element009  label="Cl_element : 006"  # scripted group (container) (typed FeaturePython)
  n = 2
  ref = Cl_element
FEATURE [App::DocumentObjectGroupPython] G4_1_2_DICHLOROETHANE  label="G4_1.2-DICHLOROETHANE"  # scripted group (container) (typed FeaturePython)
  Dunit = g/cm3
  Dvalue = 1.2351
  Group = -> [C_element034,H_element031,Cl_element009]
  conduct = 2
  density = 1
  expand = 3
  formula = G4_1.2-DICHLOROETHANE
  name = G4_1.2-DICHLOROETHANE
  specific = 4
FEATURE [App::DocumentObjectGroupPython] C_element035  label="C_element : 019"  # scripted group (container) (typed FeaturePython)
  n = 4
  ref = C_element
FEATURE [App::DocumentObjectGroupPython] H_element032  label="H_element : 015"  # scripted group (container) (typed FeaturePython)
  n = 10
  ref = H_element
FEATURE [App::DocumentObjectGroupPython] O_element032  label="O_element : 015"  # scripted group (container) (typed FeaturePython)
  n = 1
  ref = O_element
FEATURE [App::DocumentObjectGroupPython] G4_DIETHYL_ETHER  # scripted group (container) (typed FeaturePython)
  Dunit = g/cm3
  Dvalue = 0.71378
  Group = -> [C_element035,H_element032,O_element032]
  conduct = 2
  density = 1
  expand = 3
  formula = G4_DIETHYL_ETHER
  name = G4_DIETHYL_ETHER
  specific = 4
FEATURE [App::DocumentObjectGroupPython] C_element036  label="C_element : 020"  # scripted group (container) (typed FeaturePython)
  n = 3
  ref = C_element
FEATURE [App::DocumentObjectGroupPython] H_element033  label="H_element : 016"  # scripted group (container) (typed FeaturePython)
  n = 7
  ref = H_element
FEATURE [App::DocumentObjectGroupPython] N_element015  label="N_element : 008"  # scripted group (container) (typed FeaturePython)
  n = 1
  ref = N_element
FEATURE [App::DocumentObjectGroupPython] O_element033  label="O_element : 016"  # scripted group (container) (typed FeaturePython)
  n = 1
  ref = O_element
FEATURE [App::DocumentObjectGroupPython] G4_N_N_DIMETHYL_FORMAMIDE  label="G4_N.N-DIMETHYL_FORMAMIDE"  # scripted group (container) (typed FeaturePython)
  Dunit = g/cm3
  Dvalue = 0.9487
  Group = -> [C_element036,H_element033,N_element015,O_element033]
  conduct = 2
  density = 1
  expand = 3
  formula = G4_N.N-DIMETHYL_FORMAMIDE
  name = G4_N.N-DIMETHYL_FORMAMIDE
  specific = 4
FEATURE [App::DocumentObjectGroupPython] C_element037  label="C_element : 021"  # scripted group (container) (typed FeaturePython)
  n = 2
  ref = C_element
FEATURE [App::DocumentObjectGroupPython] H_element034  label="H_element : 017"  # scripted group (container) (typed FeaturePython)
  n = 6
  ref = H_element
FEATURE [App::DocumentObjectGroupPython] O_element034  label="O_element : 017"  # scripted group (container) (typed FeaturePython)
  n = 1
  ref = O_element
FEATURE [App::DocumentObjectGroupPython] S_element009  label="S_element : 003"  # scripted group (container) (typed FeaturePython)
  n = 1
  ref = S_element
FEATURE [App::DocumentObjectGroupPython] G4_DIMETHYL_SULFOXIDE  # scripted group (container) (typed FeaturePython)
  Dunit = g/cm3
  Dvalue = 1.1014
  Group = -> [C_element037,H_element034,O_element034,S_element009]
  conduct = 2
  density = 1
  expand = 3
  formula = G4_DIMETHYL_SULFOXIDE
  name = G4_DIMETHYL_SULFOXIDE
  specific = 4
FEATURE [App::DocumentObjectGroupPython] C_element038  label="C_element : 022"  # scripted group (container) (typed FeaturePython)
  n = 2
  ref = C_element
FEATURE [App::DocumentObjectGroupPython] H_element035  label="H_element : 018"  # scripted group (container) (typed FeaturePython)
  n = 6
  ref = H_element
FEATURE [App::DocumentObjectGroupPython] G4_ETHANE  # scripted group (container) (typed FeaturePython)
  Dunit = g/cm3
  Dvalue = 0.00125324
  Group = -> [C_element038,H_element035]
  conduct = 2
  density = 1
  expand = 3
  formula = G4_ETHANE
  name = G4_ETHANE
  specific = 4
FEATURE [App::DocumentObjectGroupPython] C_element039  label="C_element : 023"  # scripted group (container) (typed FeaturePython)
  n = 2
  ref = C_element
FEATURE [App::DocumentObjectGroupPython] H_element036  label="H_element : 019"  # scripted group (container) (typed FeaturePython)
  n = 6
  ref = H_element
FEATURE [App::DocumentObjectGroupPython] O_element035  label="O_element : 018"  # scripted group (container) (typed FeaturePython)
  n = 1
  ref = O_element
FEATURE [App::DocumentObjectGroupPython] G4_ETHYL_ALCOHOL  # scripted group (container) (typed FeaturePython)
  Dunit = g/cm3
  Dvalue = 0.7893
  Group = -> [C_element039,H_element036,O_element035]
  conduct = 2
  density = 1
  expand = 3
  formula = G4_ETHYL_ALCOHOL
  name = G4_ETHYL_ALCOHOL
  specific = 4
FEATURE [App::DocumentObjectGroupPython] H_element037  label="H_element : 0.090"  # scripted group (container) (typed FeaturePython)
  n = 0.090027
FEATURE [App::DocumentObjectGroupPython] C_element040  label="C_element : 0.585"  # scripted group (container) (typed FeaturePython)
  n = 0.585182
FEATURE [App::DocumentObjectGroupPython] O_element036  label="O_element : 0.325"  # scripted group (container) (typed FeaturePython)
  n = 0.324791
FEATURE [App::DocumentObjectGroupPython] G4_ETHYL_CELLULOSE  # scripted group (container) (typed FeaturePython)
  Dunit = g/cm3
  Dvalue = 1.13
  Group = -> [H_element037,C_element040,O_element036]
  conduct = 2
  density = 1
  expand = 3
  formula = G4_ETHYL_CELLULOSE
  name = G4_ETHYL_CELLULOSE
  specific = 4
FEATURE [App::DocumentObjectGroupPython] C_element041  label="C_element : 024"  # scripted group (container) (typed FeaturePython)
  n = 2
  ref = C_element
FEATURE [App::DocumentObjectGroupPython] H_element038  label="H_element : 020"  # scripted group (container) (typed FeaturePython)
  n = 4
  ref = H_element
FEATURE [App::DocumentObjectGroupPython] G4_ETHYLENE  # scripted group (container) (typed FeaturePython)
  Dunit = g/cm3
  Dvalue = 0.00117497
  Group = -> [C_element041,H_element038]
  conduct = 2
  density = 1
  expand = 3
  formula = G4_ETHYLENE
  name = G4_ETHYLENE
  specific = 4
FEATURE [App::DocumentObjectGroupPython] H_element039  label="H_element : 0.096"  # scripted group (container) (typed FeaturePython)
  n = 0.096
FEATURE [App::DocumentObjectGroupPython] C_element042  label="C_element : 0.195"  # scripted group (container) (typed FeaturePython)
  n = 0.195
FEATURE [App::DocumentObjectGroupPython] N_element016  label="N_element : 0.057"  # scripted group (container) (typed FeaturePython)
  n = 0.057
FEATURE [App::DocumentObjectGroupPython] O_element037  label="O_element : 0.646"  # scripted group (container) (typed FeaturePython)
  n = 0.646
FEATURE [App::DocumentObjectGroupPython] Na_element006  label="Na_element : 0.017"  # scripted group (container) (typed FeaturePython)
  n = 0.001
FEATURE [App::DocumentObjectGroupPython] P_element005  label="P_element : 0.104"  # scripted group (container) (typed FeaturePython)
  n = 0.001
FEATURE [App::DocumentObjectGroupPython] S_element010  label="S_element : 0.016"  # scripted group (container) (typed FeaturePython)
  n = 0.003
FEATURE [App::DocumentObjectGroupPython] Cl_element010  label="Cl_element : 0.005"  # scripted group (container) (typed FeaturePython)
  n = 0.001
FEATURE [App::DocumentObjectGroupPython] G4_EYE_LENS_ICRP  # scripted group (container) (typed FeaturePython)
  Dunit = g/cm3
  Dvalue = 1.07
  Group = -> [H_element039,C_element042,N_element016,O_element037,Na_element006,P_element005,S_element010,Cl_element010]
  conduct = 2
  density = 1
  expand = 3
  formula = G4_EYE_LENS_ICRP
  name = G4_EYE_LENS_ICRP
  specific = 4
FEATURE [App::DocumentObjectGroupPython] Fe_element003  label="Fe_element : 2"  # scripted group (container) (typed FeaturePython)
  n = 2
  ref = Fe_element
FEATURE [App::DocumentObjectGroupPython] O_element038  label="O_element : 019"  # scripted group (container) (typed FeaturePython)
  n = 3
  ref = O_element
FEATURE [App::DocumentObjectGroupPython] G4_FERRIC_OXIDE  # scripted group (container) (typed FeaturePython)
  Dunit = g/cm3
  Dvalue = 5.2
  Group = -> [Fe_element003,O_element038]
  conduct = 2
  density = 1
  expand = 3
  formula = G4_FERRIC_OXIDE
  name = G4_FERRIC_OXIDE
  specific = 4
FEATURE [App::DocumentObjectGroupPython] Fe_element004  label="Fe_element : 1"  # scripted group (container) (typed FeaturePython)
  n = 1
  ref = Fe_element
FEATURE [App::DocumentObjectGroupPython] B_element003  label="B_element : 1"  # scripted group (container) (typed FeaturePython)
  n = 1
  ref = B_element
FEATURE [App::DocumentObjectGroupPython] G4_FERROBORIDE  # scripted group (container) (typed FeaturePython)
  Dunit = g/cm3
  Dvalue = 7.15
  Group = -> [Fe_element004,B_element003]
  conduct = 2
  density = 1
  expand = 3
  formula = G4_FERROBORIDE
  name = G4_FERROBORIDE
  specific = 4
FEATURE [App::DocumentObjectGroupPython] Fe_element005  label="Fe_element : 003"  # scripted group (container) (typed FeaturePython)
  n = 1
  ref = Fe_element
FEATURE [App::DocumentObjectGroupPython] O_element039  label="O_element : 020"  # scripted group (container) (typed FeaturePython)
  n = 1
  ref = O_element
FEATURE [App::DocumentObjectGroupPython] G4_FERROUS_OXIDE  # scripted group (container) (typed FeaturePython)
  Dunit = g/cm3
  Dvalue = 5.7
  Group = -> [Fe_element005,O_element039]
  conduct = 2
  density = 1
  expand = 3
  formula = G4_FERROUS_OXIDE
  name = G4_FERROUS_OXIDE
  specific = 4
FEATURE [App::DocumentObjectGroupPython] H_element040  label="H_element : 0.115"  # scripted group (container) (typed FeaturePython)
  n = 0.108259
FEATURE [App::DocumentObjectGroupPython] N_element017  label="N_element : 0.000"  # scripted group (container) (typed FeaturePython)
  n = 2.7e-05
FEATURE [App::DocumentObjectGroupPython] O_element040  label="O_element : 0.879"  # scripted group (container) (typed FeaturePython)
  n = 0.878636
FEATURE [App::DocumentObjectGroupPython] Na_element007  label="Na_element : 0.000"  # scripted group (container) (typed FeaturePython)
  n = 2.2e-05
FEATURE [App::DocumentObjectGroupPython] S_element011  label="S_element : 0.013"  # scripted group (container) (typed FeaturePython)
  n = 0.012968
FEATURE [App::DocumentObjectGroupPython] Cl_element011  label="Cl_element : 0.000"  # scripted group (container) (typed FeaturePython)
  n = 3.4e-05
FEATURE [App::DocumentObjectGroupPython] Fe_element006  label="Fe_element : 0.000"  # scripted group (container) (typed FeaturePython)
  n = 5.4e-05
FEATURE [App::DocumentObjectGroupPython] G4_FERROUS_SULFATE  # scripted group (container) (typed FeaturePython)
  Dunit = g/cm3
  Dvalue = 1.024
  Group = -> [H_element040,N_element017,O_element040,Na_element007,S_element011,Cl_element011,Fe_element006]
  conduct = 2
  density = 1
  expand = 3
  formula = G4_FERROUS_SULFATE
  name = G4_FERROUS_SULFATE
  specific = 4
FEATURE [App::DocumentObjectGroupPython] C_element043  label="C_element : 0.099"  # scripted group (container) (typed FeaturePython)
  n = 0.099335
FEATURE [App::DocumentObjectGroupPython] F_element007  label="F_element : 0.314"  # scripted group (container) (typed FeaturePython)
  n = 0.314247
FEATURE [App::DocumentObjectGroupPython] Cl_element012  label="Cl_element : 0.586"  # scripted group (container) (typed FeaturePython)
  n = 0.586418
FEATURE [App::DocumentObjectGroupPython] G4_FREON_12  label="G4_FREON-12"  # scripted group (container) (typed FeaturePython)
  Dunit = g/cm3
  Dvalue = 1.12
  Group = -> [C_element043,F_element007,Cl_element012]
  conduct = 2
  density = 1
  expand = 3
  formula = G4_FREON-12
  name = G4_FREON-12
  specific = 4
FEATURE [App::DocumentObjectGroupPython] C_element044  label="C_element : 0.057"  # scripted group (container) (typed FeaturePython)
  n = 0.057245
FEATURE [App::DocumentObjectGroupPython] F_element008  label="F_element : 0.181"  # scripted group (container) (typed FeaturePython)
  n = 0.181096
FEATURE [App::DocumentObjectGroupPython] Br_element001  label="Br_element : 0.762"  # scripted group (container) (typed FeaturePython)
  n = 0.761659
FEATURE [App::DocumentObjectGroupPython] G4_FREON_12B2  label="G4_FREON-12B2"  # scripted group (container) (typed FeaturePython)
  Dunit = g/cm3
  Dvalue = 1.8
  Group = -> [C_element044,F_element008,Br_element001]
  conduct = 2
  density = 1
  expand = 3
  formula = G4_FREON-12B2
  name = G4_FREON-12B2
  specific = 4
FEATURE [App::DocumentObjectGroupPython] C_element045  label="C_element : 0.115"  # scripted group (container) (typed FeaturePython)
  n = 0.114983
FEATURE [App::DocumentObjectGroupPython] F_element009  label="F_element : 0.546"  # scripted group (container) (typed FeaturePython)
  n = 0.545621
FEATURE [App::DocumentObjectGroupPython] Cl_element013  label="Cl_element : 0.339"  # scripted group (container) (typed FeaturePython)
  n = 0.339396
FEATURE [App::DocumentObjectGroupPython] G4_FREON_13  label="G4_FREON-13"  # scripted group (container) (typed FeaturePython)
  Dunit = g/cm3
  Dvalue = 0.95
  Group = -> [C_element045,F_element009,Cl_element013]
  conduct = 2
  density = 1
  expand = 3
  formula = G4_FREON-13
  name = G4_FREON-13
  specific = 4
FEATURE [App::DocumentObjectGroupPython] C_element046  label="C_element : 025"  # scripted group (container) (typed FeaturePython)
  n = 1
  ref = C_element
FEATURE [App::DocumentObjectGroupPython] F_element010  label="F_element : 3"  # scripted group (container) (typed FeaturePython)
  n = 3
  ref = F_element
FEATURE [App::DocumentObjectGroupPython] Br_element002  label="Br_element : 1"  # scripted group (container) (typed FeaturePython)
  n = 1
  ref = Br_element
FEATURE [App::DocumentObjectGroupPython] G4_FREON_13B1  label="G4_FREON-13B1"  # scripted group (container) (typed FeaturePython)
  Dunit = g/cm3
  Dvalue = 1.5
  Group = -> [C_element046,F_element010,Br_element002]
  conduct = 2
  density = 1
  expand = 3
  formula = G4_FREON-13B1
  name = G4_FREON-13B1
  specific = 4
FEATURE [App::DocumentObjectGroupPython] C_element047  label="C_element : 0.061"  # scripted group (container) (typed FeaturePython)
  n = 0.061309
FEATURE [App::DocumentObjectGroupPython] F_element011  label="F_element : 0.291"  # scripted group (container) (typed FeaturePython)
  n = 0.290924
FEATURE [App::DocumentObjectGroupPython] I_element002  label="I_element : 0.648"  # scripted group (container) (typed FeaturePython)
  n = 0.647767
FEATURE [App::DocumentObjectGroupPython] G4_FREON_13I1  label="G4_FREON-13I1"  # scripted group (container) (typed FeaturePython)
  Dunit = g/cm3
  Dvalue = 1.8
  Group = -> [C_element047,F_element011,I_element002]
  conduct = 2
  density = 1
  expand = 3
  formula = G4_FREON-13I1
  name = G4_FREON-13I1
  specific = 4
FEATURE [App::DocumentObjectGroupPython] Gd_element001  label="Gd_element : 2"  # scripted group (container) (typed FeaturePython)
  n = 2
  ref = Gd_element
FEATURE [App::DocumentObjectGroupPython] O_element041  label="O_element : 021"  # scripted group (container) (typed FeaturePython)
  n = 2
  ref = O_element
FEATURE [App::DocumentObjectGroupPython] S_element012  label="S_element : 004"  # scripted group (container) (typed FeaturePython)
  n = 1
  ref = S_element
FEATURE [App::DocumentObjectGroupPython] G4_GADOLINIUM_OXYSULFIDE  # scripted group (container) (typed FeaturePython)
  Dunit = g/cm3
  Dvalue = 7.44
  Group = -> [Gd_element001,O_element041,S_element012]
  conduct = 2
  density = 1
  expand = 3
  formula = G4_GADOLINIUM_OXYSULFIDE
  name = G4_GADOLINIUM_OXYSULFIDE
  specific = 4
FEATURE [App::DocumentObjectGroupPython] Ga_element001  label="Ga_element : 1"  # scripted group (container) (typed FeaturePython)
  n = 1
  ref = Ga_element
FEATURE [App::DocumentObjectGroupPython] As_element001  label="As_element : 1"  # scripted group (container) (typed FeaturePython)
  n = 1
  ref = As_element
FEATURE [App::DocumentObjectGroupPython] G4_GALLIUM_ARSENIDE  # scripted group (container) (typed FeaturePython)
  Dunit = g/cm3
  Dvalue = 5.31
  Group = -> [Ga_element001,As_element001]
  conduct = 2
  density = 1
  expand = 3
  formula = G4_GALLIUM_ARSENIDE
  name = G4_GALLIUM_ARSENIDE
  specific = 4
FEATURE [App::DocumentObjectGroupPython] H_element041  label="H_element : 0.081"  # scripted group (container) (typed FeaturePython)
  n = 0.08118
FEATURE [App::DocumentObjectGroupPython] C_element048  label="C_element : 0.416"  # scripted group (container) (typed FeaturePython)
  n = 0.41606
FEATURE [App::DocumentObjectGroupPython] N_element018  label="N_element : 0.111"  # scripted group (container) (typed FeaturePython)
  n = 0.11124
FEATURE [App::DocumentObjectGroupPython] O_element042  label="O_element : 0.381"  # scripted group (container) (typed FeaturePython)
  n = 0.38064
FEATURE [App::DocumentObjectGroupPython] S_element013  label="S_element : 0.011"  # scripted group (container) (typed FeaturePython)
  n = 0.01088
FEATURE [App::DocumentObjectGroupPython] G4_GEL_PHOTO_EMULSION  # scripted group (container) (typed FeaturePython)
  Dunit = g/cm3
  Dvalue = 1.2914
  Group = -> [H_element041,C_element048,N_element018,O_element042,S_element013]
  conduct = 2
  density = 1
  expand = 3
  formula = G4_GEL_PHOTO_EMULSION
  name = G4_GEL_PHOTO_EMULSION
  specific = 4
FEATURE [App::DocumentObjectGroupPython] B_element004  label="B_element : 0.040"  # scripted group (container) (typed FeaturePython)
  n = 0.0400639
FEATURE [App::DocumentObjectGroupPython] O_element043  label="O_element : 0.540"  # scripted group (container) (typed FeaturePython)
  n = 0.539561
FEATURE [App::DocumentObjectGroupPython] Na_element008  label="Na_element : 0.028"  # scripted group (container) (typed FeaturePython)
  n = 0.0281909
FEATURE [App::DocumentObjectGroupPython] Al_element003  label="Al_element : 0.012"  # scripted group (container) (typed FeaturePython)
  n = 0.011644
FEATURE [App::DocumentObjectGroupPython] Si_element003  label="Si_element : 0.377"  # scripted group (container) (typed FeaturePython)
  n = 0.377219
FEATURE [App::DocumentObjectGroupPython] K_element004  label="K_element : 0.014"  # scripted group (container) (typed FeaturePython)
  n = 0.00332099
FEATURE [App::DocumentObjectGroupPython] G4_Pyrex_Glass  # scripted group (container) (typed FeaturePython)
  Dunit = g/cm3
  Dvalue = 2.23
  Group = -> [B_element004,O_element043,Na_element008,Al_element003,Si_element003,K_element004]
  conduct = 2
  density = 1
  expand = 3
  formula = G4_Pyrex_Glass
  name = G4_Pyrex_Glass
  specific = 4
FEATURE [App::DocumentObjectGroupPython] O_element044  label="O_element : 0.156"  # scripted group (container) (typed FeaturePython)
  n = 0.156453
FEATURE [App::DocumentObjectGroupPython] Si_element004  label="Si_element : 0.081"  # scripted group (container) (typed FeaturePython)
  n = 0.080866
FEATURE [App::DocumentObjectGroupPython] Ti_element001  label="Ti_element : 0.008"  # scripted group (container) (typed FeaturePython)
  n = 0.008092
FEATURE [App::DocumentObjectGroupPython] As_element002  label="As_element : 0.003"  # scripted group (container) (typed FeaturePython)
  n = 0.002651
FEATURE [App::DocumentObjectGroupPython] Pb_element001  label="Pb_element : 0.752"  # scripted group (container) (typed FeaturePython)
  n = 0.751938
FEATURE [App::DocumentObjectGroupPython] G4_GLASS_LEAD  # scripted group (container) (typed FeaturePython)
  Dunit = g/cm3
  Dvalue = 6.22
  Group = -> [O_element044,Si_element004,Ti_element001,As_element002,Pb_element001]
  conduct = 2
  density = 1
  expand = 3
  formula = G4_GLASS_LEAD
  name = G4_GLASS_LEAD
  specific = 4
FEATURE [App::DocumentObjectGroupPython] O_element045  label="O_element : 0.460"  # scripted group (container) (typed FeaturePython)
  n = 0.4598
FEATURE [App::DocumentObjectGroupPython] Na_element009  label="Na_element : 0.096"  # scripted group (container) (typed FeaturePython)
  n = 0.0964411
FEATURE [App::DocumentObjectGroupPython] Si_element005  label="Si_element : 0.378"  # scripted group (container) (typed FeaturePython)
  n = 0.336553
FEATURE [App::DocumentObjectGroupPython] Ca_element011  label="Ca_element : 0.107"  # scripted group (container) (typed FeaturePython)
  n = 0.107205
FEATURE [App::DocumentObjectGroupPython] G4_GLASS_PLATE  # scripted group (container) (typed FeaturePython)
  Dunit = g/cm3
  Dvalue = 2.4
  Group = -> [O_element045,Na_element009,Si_element005,Ca_element011]
  conduct = 2
  density = 1
  expand = 3
  formula = G4_GLASS_PLATE
  name = G4_GLASS_PLATE
  specific = 4
FEATURE [App::DocumentObjectGroupPython] C_element049  label="C_element : 026"  # scripted group (container) (typed FeaturePython)
  n = 5
  ref = C_element
FEATURE [App::DocumentObjectGroupPython] H_element042  label="H_element : 021"  # scripted group (container) (typed FeaturePython)
  n = 10
  ref = H_element
FEATURE [App::DocumentObjectGroupPython] N_element019  label="N_element : 2"  # scripted group (container) (typed FeaturePython)
  n = 2
  ref = N_element
FEATURE [App::DocumentObjectGroupPython] O_element046  label="O_element : 022"  # scripted group (container) (typed FeaturePython)
  n = 3
  ref = O_element
FEATURE [App::DocumentObjectGroupPython] G4_GLUTAMINE  # scripted group (container) (typed FeaturePython)
  Dunit = g/cm3
  Dvalue = 1.46
  Group = -> [C_element049,H_element042,N_element019,O_element046]
  conduct = 2
  density = 1
  expand = 3
  formula = G4_GLUTAMINE
  name = G4_GLUTAMINE
  specific = 4
FEATURE [App::DocumentObjectGroupPython] C_element050  label="C_element : 027"  # scripted group (container) (typed FeaturePython)
  n = 3
  ref = C_element
FEATURE [App::DocumentObjectGroupPython] H_element043  label="H_element : 022"  # scripted group (container) (typed FeaturePython)
  n = 8
  ref = H_element
FEATURE [App::DocumentObjectGroupPython] O_element047  label="O_element : 023"  # scripted group (container) (typed FeaturePython)
  n = 3
  ref = O_element
FEATURE [App::DocumentObjectGroupPython] G4_GLYCEROL  # scripted group (container) (typed FeaturePython)
  Dunit = g/cm3
  Dvalue = 1.2613
  Group = -> [C_element050,H_element043,O_element047]
  conduct = 2
  density = 1
  expand = 3
  formula = G4_GLYCEROL
  name = G4_GLYCEROL
  specific = 4
FEATURE [App::DocumentObjectGroupPython] C_element051  label="C_element : 028"  # scripted group (container) (typed FeaturePython)
  n = 5
  ref = C_element
FEATURE [App::DocumentObjectGroupPython] H_element044  label="H_element : 023"  # scripted group (container) (typed FeaturePython)
  n = 5
  ref = H_element
FEATURE [App::DocumentObjectGroupPython] N_element020  label="N_element : 009"  # scripted group (container) (typed FeaturePython)
  n = 5
  ref = N_element
FEATURE [App::DocumentObjectGroupPython] O_element048  label="O_element : 024"  # scripted group (container) (typed FeaturePython)
  n = 1
  ref = O_element
FEATURE [App::DocumentObjectGroupPython] G4_GUANINE  # scripted group (container) (typed FeaturePython)
  Dunit = g/cm3
  Dvalue = 2.2
  Group = -> [C_element051,H_element044,N_element020,O_element048]
  conduct = 2
  density = 1
  expand = 3
  formula = G4_GUANINE
  name = G4_GUANINE
  specific = 4
FEATURE [App::DocumentObjectGroupPython] Ca_element012  label="Ca_element : 006"  # scripted group (container) (typed FeaturePython)
  n = 1
  ref = Ca_element
FEATURE [App::DocumentObjectGroupPython] S_element014  label="S_element : 005"  # scripted group (container) (typed FeaturePython)
  n = 1
  ref = S_element
FEATURE [App::DocumentObjectGroupPython] O_element049  label="O_element : 6"  # scripted group (container) (typed FeaturePython)
  n = 6
  ref = O_element
FEATURE [App::DocumentObjectGroupPython] H_element045  label="H_element : 024"  # scripted group (container) (typed FeaturePython)
  n = 4
  ref = H_element
FEATURE [App::DocumentObjectGroupPython] G4_GYPSUM  # scripted group (container) (typed FeaturePython)
  Dunit = g/cm3
  Dvalue = 2.32
  Group = -> [Ca_element012,S_element014,O_element049,H_element045]
  conduct = 2
  density = 1
  expand = 3
  formula = G4_GYPSUM
  name = G4_GYPSUM
  specific = 4
FEATURE [App::DocumentObjectGroupPython] C_element052  label="C_element : 7"  # scripted group (container) (typed FeaturePython)
  n = 7
  ref = C_element
FEATURE [App::DocumentObjectGroupPython] H_element046  label="H_element : 16"  # scripted group (container) (typed FeaturePython)
  n = 16
  ref = H_element
FEATURE [App::DocumentObjectGroupPython] G4_N_HEPTANE  label="G4_N-HEPTANE"  # scripted group (container) (typed FeaturePython)
  Dunit = g/cm3
  Dvalue = 0.68376
  Group = -> [C_element052,H_element046]
  conduct = 2
  density = 1
  expand = 3
  formula = G4_N-HEPTANE
  name = G4_N-HEPTANE
  specific = 4
FEATURE [App::DocumentObjectGroupPython] C_element053  label="C_element : 029"  # scripted group (container) (typed FeaturePython)
  n = 6
  ref = C_element
FEATURE [App::DocumentObjectGroupPython] H_element047  label="H_element : 14"  # scripted group (container) (typed FeaturePython)
  n = 14
  ref = H_element
FEATURE [App::DocumentObjectGroupPython] G4_N_HEXANE  label="G4_N-HEXANE"  # scripted group (container) (typed FeaturePython)
  Dunit = g/cm3
  Dvalue = 0.6603
  Group = -> [C_element053,H_element047]
  conduct = 2
  density = 1
  expand = 3
  formula = G4_N-HEXANE
  name = G4_N-HEXANE
  specific = 4
FEATURE [App::DocumentObjectGroupPython] C_element054  label="C_element : 22"  # scripted group (container) (typed FeaturePython)
  n = 22
  ref = C_element
FEATURE [App::DocumentObjectGroupPython] H_element048  label="H_element : 025"  # scripted group (container) (typed FeaturePython)
  n = 10
  ref = H_element
FEATURE [App::DocumentObjectGroupPython] N_element021  label="N_element : 010"  # scripted group (container) (typed FeaturePython)
  n = 2
  ref = N_element
FEATURE [App::DocumentObjectGroupPython] O_element050  label="O_element : 025"  # scripted group (container) (typed FeaturePython)
  n = 5
  ref = O_element
FEATURE [App::DocumentObjectGroupPython] G4_KAPTON  # scripted group (container) (typed FeaturePython)
  Dunit = g/cm3
  Dvalue = 1.42
  Group = -> [C_element054,H_element048,N_element021,O_element050]
  conduct = 2
  density = 1
  expand = 3
  formula = G4_KAPTON
  name = G4_KAPTON
  specific = 4
FEATURE [App::DocumentObjectGroupPython] La_element001  label="La_element : 1"  # scripted group (container) (typed FeaturePython)
  n = 1
  ref = La_element
FEATURE [App::DocumentObjectGroupPython] Br_element003  label="Br_element : 002"  # scripted group (container) (typed FeaturePython)
  n = 1
  ref = Br_element
FEATURE [App::DocumentObjectGroupPython] O_element051  label="O_element : 026"  # scripted group (container) (typed FeaturePython)
  n = 1
  ref = O_element
FEATURE [App::DocumentObjectGroupPython] G4_LANTHANUM_OXYBROMIDE  # scripted group (container) (typed FeaturePython)
  Dunit = g/cm3
  Dvalue = 6.28
  Group = -> [La_element001,Br_element003,O_element051]
  conduct = 2
  density = 1
  expand = 3
  formula = G4_LANTHANUM_OXYBROMIDE
  name = G4_LANTHANUM_OXYBROMIDE
  specific = 4
FEATURE [App::DocumentObjectGroupPython] La_element002  label="La_element : 2"  # scripted group (container) (typed FeaturePython)
  n = 2
  ref = La_element
FEATURE [App::DocumentObjectGroupPython] O_element052  label="O_element : 027"  # scripted group (container) (typed FeaturePython)
  n = 2
  ref = O_element
FEATURE [App::DocumentObjectGroupPython] S_element015  label="S_element : 006"  # scripted group (container) (typed FeaturePython)
  n = 1
  ref = S_element
FEATURE [App::DocumentObjectGroupPython] G4_LANTHANUM_OXYSULFIDE  # scripted group (container) (typed FeaturePython)
  Dunit = g/cm3
  Dvalue = 5.86
  Group = -> [La_element002,O_element052,S_element015]
  conduct = 2
  density = 1
  expand = 3
  formula = G4_LANTHANUM_OXYSULFIDE
  name = G4_LANTHANUM_OXYSULFIDE
  specific = 4
FEATURE [App::DocumentObjectGroupPython] O_element053  label="O_element : 0.072"  # scripted group (container) (typed FeaturePython)
  n = 0.071682
FEATURE [App::DocumentObjectGroupPython] Pb_element002  label="Pb_element : 0.928"  # scripted group (container) (typed FeaturePython)
  n = 0.928318
FEATURE [App::DocumentObjectGroupPython] G4_LEAD_OXIDE  # scripted group (container) (typed FeaturePython)
  Dunit = g/cm3
  Dvalue = 9.53
  Group = -> [O_element053,Pb_element002]
  conduct = 2
  density = 1
  expand = 3
  formula = G4_LEAD_OXIDE
  name = G4_LEAD_OXIDE
  specific = 4
FEATURE [App::DocumentObjectGroupPython] Li_element001  label="Li_element : 1"  # scripted group (container) (typed FeaturePython)
  n = 1
  ref = Li_element
FEATURE [App::DocumentObjectGroupPython] N_element022  label="N_element : 011"  # scripted group (container) (typed FeaturePython)
  n = 1
  ref = N_element
FEATURE [App::DocumentObjectGroupPython] H_element049  label="H_element : 026"  # scripted group (container) (typed FeaturePython)
  n = 2
  ref = H_element
FEATURE [App::DocumentObjectGroupPython] G4_LITHIUM_AMIDE  # scripted group (container) (typed FeaturePython)
  Dunit = g/cm3
  Dvalue = 1.178
  Group = -> [Li_element001,N_element022,H_element049]
  conduct = 2
  density = 1
  expand = 3
  formula = G4_LITHIUM_AMIDE
  name = G4_LITHIUM_AMIDE
  specific = 4
FEATURE [App::DocumentObjectGroupPython] Li_element002  label="Li_element : 2"  # scripted group (container) (typed FeaturePython)
  n = 2
  ref = Li_element
FEATURE [App::DocumentObjectGroupPython] C_element055  label="C_element : 030"  # scripted group (container) (typed FeaturePython)
  n = 1
  ref = C_element
FEATURE [App::DocumentObjectGroupPython] O_element054  label="O_element : 028"  # scripted group (container) (typed FeaturePython)
  n = 3
  ref = O_element
FEATURE [App::DocumentObjectGroupPython] G4_LITHIUM_CARBONATE  # scripted group (container) (typed FeaturePython)
  Dunit = g/cm3
  Dvalue = 2.11
  Group = -> [Li_element002,C_element055,O_element054]
  conduct = 2
  density = 1
  expand = 3
  formula = G4_LITHIUM_CARBONATE
  name = G4_LITHIUM_CARBONATE
  specific = 4
FEATURE [App::DocumentObjectGroupPython] Li_element003  label="Li_element : 003"  # scripted group (container) (typed FeaturePython)
  n = 1
  ref = Li_element
FEATURE [App::DocumentObjectGroupPython] F_element012  label="F_element : 004"  # scripted group (container) (typed FeaturePython)
  n = 1
  ref = F_element
FEATURE [App::DocumentObjectGroupPython] G4_LITHIUM_FLUORIDE  # scripted group (container) (typed FeaturePython)
  Dunit = g/cm3
  Dvalue = 2.635
  Group = -> [Li_element003,F_element012]
  conduct = 2
  density = 1
  expand = 3
  formula = G4_LITHIUM_FLUORIDE
  name = G4_LITHIUM_FLUORIDE
  specific = 4
FEATURE [App::DocumentObjectGroupPython] Li_element004  label="Li_element : 004"  # scripted group (container) (typed FeaturePython)
  n = 1
  ref = Li_element
FEATURE [App::DocumentObjectGroupPython] H_element050  label="H_element : 027"  # scripted group (container) (typed FeaturePython)
  n = 1
  ref = H_element
FEATURE [App::DocumentObjectGroupPython] G4_LITHIUM_HYDRIDE  # scripted group (container) (typed FeaturePython)
  Dunit = g/cm3
  Dvalue = 0.82
  Group = -> [Li_element004,H_element050]
  conduct = 2
  density = 1
  expand = 3
  formula = G4_LITHIUM_HYDRIDE
  name = G4_LITHIUM_HYDRIDE
  specific = 4
FEATURE [App::DocumentObjectGroupPython] Li_element005  label="Li_element : 005"  # scripted group (container) (typed FeaturePython)
  n = 1
  ref = Li_element
FEATURE [App::DocumentObjectGroupPython] I_element003  label="I_element : 002"  # scripted group (container) (typed FeaturePython)
  n = 1
  ref = I_element
FEATURE [App::DocumentObjectGroupPython] G4_LITHIUM_IODIDE  # scripted group (container) (typed FeaturePython)
  Dunit = g/cm3
  Dvalue = 3.494
  Group = -> [Li_element005,I_element003]
  conduct = 2
  density = 1
  expand = 3
  formula = G4_LITHIUM_IODIDE
  name = G4_LITHIUM_IODIDE
  specific = 4
FEATURE [App::DocumentObjectGroupPython] Li_element006  label="Li_element : 006"  # scripted group (container) (typed FeaturePython)
  n = 2
  ref = Li_element
FEATURE [App::DocumentObjectGroupPython] O_element055  label="O_element : 029"  # scripted group (container) (typed FeaturePython)
  n = 1
  ref = O_element
FEATURE [App::DocumentObjectGroupPython] G4_LITHIUM_OXIDE  # scripted group (container) (typed FeaturePython)
  Dunit = g/cm3
  Dvalue = 2.013
  Group = -> [Li_element006,O_element055]
  conduct = 2
  density = 1
  expand = 3
  formula = G4_LITHIUM_OXIDE
  name = G4_LITHIUM_OXIDE
  specific = 4
FEATURE [App::DocumentObjectGroupPython] Li_element007  label="Li_element : 007"  # scripted group (container) (typed FeaturePython)
  n = 2
  ref = Li_element
FEATURE [App::DocumentObjectGroupPython] B_element005  label="B_element : 005"  # scripted group (container) (typed FeaturePython)
  n = 4
  ref = B_element
FEATURE [App::DocumentObjectGroupPython] O_element056  label="O_element : 7"  # scripted group (container) (typed FeaturePython)
  n = 7
  ref = O_element
FEATURE [App::DocumentObjectGroupPython] G4_LITHIUM_TETRABORATE  # scripted group (container) (typed FeaturePython)
  Dunit = g/cm3
  Dvalue = 2.44
  Group = -> [Li_element007,B_element005,O_element056]
  conduct = 2
  density = 1
  expand = 3
  formula = G4_LITHIUM_TETRABORATE
  name = G4_LITHIUM_TETRABORATE
  specific = 4
FEATURE [App::DocumentObjectGroupPython] H_element051  label="H_element : 0.105"  # scripted group (container) (typed FeaturePython)
  n = 0.105
FEATURE [App::DocumentObjectGroupPython] C_element056  label="C_element : 0.083"  # scripted group (container) (typed FeaturePython)
  n = 0.083
FEATURE [App::DocumentObjectGroupPython] N_element023  label="N_element : 0.023"  # scripted group (container) (typed FeaturePython)
  n = 0.023
FEATURE [App::DocumentObjectGroupPython] O_element057  label="O_element : 0.779"  # scripted group (container) (typed FeaturePython)
  n = 0.779
FEATURE [App::DocumentObjectGroupPython] Na_element010  label="Na_element : 0.097"  # scripted group (container) (typed FeaturePython)
  n = 0.002
FEATURE [App::DocumentObjectGroupPython] P_element006  label="P_element : 0.105"  # scripted group (container) (typed FeaturePython)
  n = 0.001
FEATURE [App::DocumentObjectGroupPython] S_element016  label="S_element : 0.017"  # scripted group (container) (typed FeaturePython)
  n = 0.002
FEATURE [App::DocumentObjectGroupPython] Cl_element014  label="Cl_element : 0.587"  # scripted group (container) (typed FeaturePython)
  n = 0.003
FEATURE [App::DocumentObjectGroupPython] K_element005  label="K_element : 0.015"  # scripted group (container) (typed FeaturePython)
  n = 0.002
FEATURE [App::DocumentObjectGroupPython] G4_LUNG_ICRP  # scripted group (container) (typed FeaturePython)
  Dunit = g/cm3
  Dvalue = 1.04
  Group = -> [H_element051,C_element056,N_element023,O_element057,Na_element010,P_element006,S_element016,Cl_element014,K_element005]
  conduct = 2
  density = 1
  expand = 3
  formula = G4_LUNG_ICRP
  name = G4_LUNG_ICRP
  specific = 4
FEATURE [App::DocumentObjectGroupPython] H_element052  label="H_element : 0.116"  # scripted group (container) (typed FeaturePython)
  n = 0.114318
FEATURE [App::DocumentObjectGroupPython] C_element057  label="C_element : 0.656"  # scripted group (container) (typed FeaturePython)
  n = 0.655824
FEATURE [App::DocumentObjectGroupPython] O_element058  label="O_element : 0.092"  # scripted group (container) (typed FeaturePython)
  n = 0.0921831
FEATURE [App::DocumentObjectGroupPython] Mg_element004  label="Mg_element : 0.135"  # scripted group (container) (typed FeaturePython)
  n = 0.134792
FEATURE [App::DocumentObjectGroupPython] Ca_element013  label="Ca_element : 0.003"  # scripted group (container) (typed FeaturePython)
  n = 0.002883
FEATURE [App::DocumentObjectGroupPython] G4_M3_WAX  # scripted group (container) (typed FeaturePython)
  Dunit = g/cm3
  Dvalue = 1.05
  Group = -> [H_element052,C_element057,O_element058,Mg_element004,Ca_element013]
  conduct = 2
  density = 1
  expand = 3
  formula = G4_M3_WAX
  name = G4_M3_WAX
  specific = 4
FEATURE [App::DocumentObjectGroupPython] Mg_element005  label="Mg_element : 1"  # scripted group (container) (typed FeaturePython)
  n = 1
  ref = Mg_element
FEATURE [App::DocumentObjectGroupPython] C_element058  label="C_element : 031"  # scripted group (container) (typed FeaturePython)
  n = 1
  ref = C_element
FEATURE [App::DocumentObjectGroupPython] O_element059  label="O_element : 030"  # scripted group (container) (typed FeaturePython)
  n = 3
  ref = O_element
FEATURE [App::DocumentObjectGroupPython] G4_MAGNESIUM_CARBONATE  # scripted group (container) (typed FeaturePython)
  Dunit = g/cm3
  Dvalue = 2.958
  Group = -> [Mg_element005,C_element058,O_element059]
  conduct = 2
  density = 1
  expand = 3
  formula = G4_MAGNESIUM_CARBONATE
  name = G4_MAGNESIUM_CARBONATE
  specific = 4
FEATURE [App::DocumentObjectGroupPython] Mg_element006  label="Mg_element : 002"  # scripted group (container) (typed FeaturePython)
  n = 1
  ref = Mg_element
FEATURE [App::DocumentObjectGroupPython] F_element013  label="F_element : 005"  # scripted group (container) (typed FeaturePython)
  n = 2
  ref = F_element
FEATURE [App::DocumentObjectGroupPython] G4_MAGNESIUM_FLUORIDE  # scripted group (container) (typed FeaturePython)
  Dunit = g/cm3
  Dvalue = 3
  Group = -> [Mg_element006,F_element013]
  conduct = 2
  density = 1
  expand = 3
  formula = G4_MAGNESIUM_FLUORIDE
  name = G4_MAGNESIUM_FLUORIDE
  specific = 4
FEATURE [App::DocumentObjectGroupPython] Mg_element007  label="Mg_element : 003"  # scripted group (container) (typed FeaturePython)
  n = 1
  ref = Mg_element
FEATURE [App::DocumentObjectGroupPython] O_element060  label="O_element : 031"  # scripted group (container) (typed FeaturePython)
  n = 1
  ref = O_element
FEATURE [App::DocumentObjectGroupPython] G4_MAGNESIUM_OXIDE  # scripted group (container) (typed FeaturePython)
  Dunit = g/cm3
  Dvalue = 3.58
  Group = -> [Mg_element007,O_element060]
  conduct = 2
  density = 1
  expand = 3
  formula = G4_MAGNESIUM_OXIDE
  name = G4_MAGNESIUM_OXIDE
  specific = 4
FEATURE [App::DocumentObjectGroupPython] Mg_element008  label="Mg_element : 004"  # scripted group (container) (typed FeaturePython)
  n = 1
  ref = Mg_element
FEATURE [App::DocumentObjectGroupPython] B_element006  label="B_element : 006"  # scripted group (container) (typed FeaturePython)
  n = 4
  ref = B_element
FEATURE [App::DocumentObjectGroupPython] O_element061  label="O_element : 032"  # scripted group (container) (typed FeaturePython)
  n = 7
  ref = O_element
FEATURE [App::DocumentObjectGroupPython] G4_MAGNESIUM_TETRABORATE  # scripted group (container) (typed FeaturePython)
  Dunit = g/cm3
  Dvalue = 2.53
  Group = -> [Mg_element008,B_element006,O_element061]
  conduct = 2
  density = 1
  expand = 3
  formula = G4_MAGNESIUM_TETRABORATE
  name = G4_MAGNESIUM_TETRABORATE
  specific = 4
FEATURE [App::DocumentObjectGroupPython] Hg_element001  label="Hg_element : 1"  # scripted group (container) (typed FeaturePython)
  n = 1
  ref = Hg_element
FEATURE [App::DocumentObjectGroupPython] I_element004  label="I_element : 2"  # scripted group (container) (typed FeaturePython)
  n = 2
  ref = I_element
FEATURE [App::DocumentObjectGroupPython] G4_MERCURIC_IODIDE  # scripted group (container) (typed FeaturePython)
  Dunit = g/cm3
  Dvalue = 6.36
  Group = -> [Hg_element001,I_element004]
  conduct = 2
  density = 1
  expand = 3
  formula = G4_MERCURIC_IODIDE
  name = G4_MERCURIC_IODIDE
  specific = 4
FEATURE [App::DocumentObjectGroupPython] C_element059  label="C_element : 032"  # scripted group (container) (typed FeaturePython)
  n = 1
  ref = C_element
FEATURE [App::DocumentObjectGroupPython] H_element053  label="H_element : 028"  # scripted group (container) (typed FeaturePython)
  n = 4
  ref = H_element
FEATURE [App::DocumentObjectGroupPython] G4_METHANE  # scripted group (container) (typed FeaturePython)
  Dunit = g/cm3
  Dvalue = 0.000667151
  Group = -> [C_element059,H_element053]
  conduct = 2
  density = 1
  expand = 3
  formula = G4_METHANE
  name = G4_METHANE
  specific = 4
FEATURE [App::DocumentObjectGroupPython] C_element060  label="C_element : 033"  # scripted group (container) (typed FeaturePython)
  n = 1
  ref = C_element
FEATURE [App::DocumentObjectGroupPython] H_element054  label="H_element : 029"  # scripted group (container) (typed FeaturePython)
  n = 4
  ref = H_element
FEATURE [App::DocumentObjectGroupPython] O_element062  label="O_element : 033"  # scripted group (container) (typed FeaturePython)
  n = 1
  ref = O_element
FEATURE [App::DocumentObjectGroupPython] G4_METHANOL  # scripted group (container) (typed FeaturePython)
  Dunit = g/cm3
  Dvalue = 0.7914
  Group = -> [C_element060,H_element054,O_element062]
  conduct = 2
  density = 1
  expand = 3
  formula = G4_METHANOL
  name = G4_METHANOL
  specific = 4
FEATURE [App::DocumentObjectGroupPython] H_element055  label="H_element : 0.134"  # scripted group (container) (typed FeaturePython)
  n = 0.13404
FEATURE [App::DocumentObjectGroupPython] C_element061  label="C_element : 0.778"  # scripted group (container) (typed FeaturePython)
  n = 0.77796
FEATURE [App::DocumentObjectGroupPython] O_element063  label="O_element : 0.035"  # scripted group (container) (typed FeaturePython)
  n = 0.03502
FEATURE [App::DocumentObjectGroupPython] Mg_element009  label="Mg_element : 0.039"  # scripted group (container) (typed FeaturePython)
  n = 0.038594
FEATURE [App::DocumentObjectGroupPython] Ti_element002  label="Ti_element : 0.014"  # scripted group (container) (typed FeaturePython)
  n = 0.014386
FEATURE [App::DocumentObjectGroupPython] G4_MIX_D_WAX  # scripted group (container) (typed FeaturePython)
  Dunit = g/cm3
  Dvalue = 0.99
  Group = -> [H_element055,C_element061,O_element063,Mg_element009,Ti_element002]
  conduct = 2
  density = 1
  expand = 3
  formula = G4_MIX_D_WAX
  name = G4_MIX_D_WAX
  specific = 4
FEATURE [App::DocumentObjectGroupPython] H_element056  label="H_element : 0.135"  # scripted group (container) (typed FeaturePython)
  n = 0.081192
FEATURE [App::DocumentObjectGroupPython] C_element062  label="C_element : 0.583"  # scripted group (container) (typed FeaturePython)
  n = 0.583442
FEATURE [App::DocumentObjectGroupPython] N_element024  label="N_element : 0.018"  # scripted group (container) (typed FeaturePython)
  n = 0.017798
FEATURE [App::DocumentObjectGroupPython] O_element064  label="O_element : 0.186"  # scripted group (container) (typed FeaturePython)
  n = 0.186381
FEATURE [App::DocumentObjectGroupPython] Mg_element010  label="Mg_element : 0.130"  # scripted group (container) (typed FeaturePython)
  n = 0.130287
FEATURE [App::DocumentObjectGroupPython] Cl_element015  label="Cl_element : 0.588"  # scripted group (container) (typed FeaturePython)
  n = 0.0009
FEATURE [App::DocumentObjectGroupPython] G4_MS20_TISSUE  # scripted group (container) (typed FeaturePython)
  Dunit = g/cm3
  Dvalue = 1
  Group = -> [H_element056,C_element062,N_element024,O_element064,Mg_element010,Cl_element015]
  conduct = 2
  density = 1
  expand = 3
  formula = G4_MS20_TISSUE
  name = G4_MS20_TISSUE
  specific = 4
FEATURE [App::DocumentObjectGroupPython] H_element057  label="H_element : 0.136"  # scripted group (container) (typed FeaturePython)
  n = 0.102
FEATURE [App::DocumentObjectGroupPython] C_element063  label="C_element : 0.143"  # scripted group (container) (typed FeaturePython)
  n = 0.143
FEATURE [App::DocumentObjectGroupPython] N_element025  label="N_element : 0.034"  # scripted group (container) (typed FeaturePython)
  n = 0.034
FEATURE [App::DocumentObjectGroupPython] O_element065  label="O_element : 0.710"  # scripted group (container) (typed FeaturePython)
  n = 0.71
FEATURE [App::DocumentObjectGroupPython] Na_element011  label="Na_element : 0.098"  # scripted group (container) (typed FeaturePython)
  n = 0.001
FEATURE [App::DocumentObjectGroupPython] P_element007  label="P_element : 0.002"  # scripted group (container) (typed FeaturePython)
  n = 0.002
FEATURE [App::DocumentObjectGroupPython] S_element017  label="S_element : 0.018"  # scripted group (container) (typed FeaturePython)
  n = 0.003
FEATURE [App::DocumentObjectGroupPython] Cl_element016  label="Cl_element : 0.589"  # scripted group (container) (typed FeaturePython)
  n = 0.001
FEATURE [App::DocumentObjectGroupPython] K_element006  label="K_element : 0.004"  # scripted group (container) (typed FeaturePython)
  n = 0.004
FEATURE [App::DocumentObjectGroupPython] G4_MUSCLE_SKELETAL_ICRP  # scripted group (container) (typed FeaturePython)
  Dunit = g/cm3
  Dvalue = 1.05
  Group = -> [H_element057,C_element063,N_element025,O_element065,Na_element011,P_element007,S_element017,Cl_element016,K_element006]
  conduct = 2
  density = 1
  expand = 3
  formula = G4_MUSCLE_SKELETAL_ICRP
  name = G4_MUSCLE_SKELETAL_ICRP
  specific = 4
FEATURE [App::DocumentObjectGroupPython] H_element058  label="H_element : 0.137"  # scripted group (container) (typed FeaturePython)
  n = 0.102102
FEATURE [App::DocumentObjectGroupPython] C_element064  label="C_element : 0.123"  # scripted group (container) (typed FeaturePython)
  n = 0.123123
FEATURE [App::DocumentObjectGroupPython] N_element026  label="N_element : 0.756"  # scripted group (container) (typed FeaturePython)
  n = 0.035035
FEATURE [App::DocumentObjectGroupPython] O_element066  label="O_element : 0.730"  # scripted group (container) (typed FeaturePython)
  n = 0.72973
FEATURE [App::DocumentObjectGroupPython] Na_element012  label="Na_element : 0.099"  # scripted group (container) (typed FeaturePython)
  n = 0.001001
FEATURE [App::DocumentObjectGroupPython] P_element008  label="P_element : 0.106"  # scripted group (container) (typed FeaturePython)
  n = 0.002002
FEATURE [App::DocumentObjectGroupPython] S_element018  label="S_element : 0.019"  # scripted group (container) (typed FeaturePython)
  n = 0.004004
FEATURE [App::DocumentObjectGroupPython] K_element007  label="K_element : 0.016"  # scripted group (container) (typed FeaturePython)
  n = 0.003003
FEATURE [App::DocumentObjectGroupPython] G4_MUSCLE_STRIATED_ICRU  # scripted group (container) (typed FeaturePython)
  Dunit = g/cm3
  Dvalue = 1.04
  Group = -> [H_element058,C_element064,N_element026,O_element066,Na_element012,P_element008,S_element018,K_element007]
  conduct = 2
  density = 1
  expand = 3
  formula = G4_MUSCLE_STRIATED_ICRU
  name = G4_MUSCLE_STRIATED_ICRU
  specific = 4
FEATURE [App::DocumentObjectGroupPython] H_element059  label="H_element : 0.098"  # scripted group (container) (typed FeaturePython)
  n = 0.0982341
FEATURE [App::DocumentObjectGroupPython] C_element065  label="C_element : 0.156"  # scripted group (container) (typed FeaturePython)
  n = 0.156214
FEATURE [App::DocumentObjectGroupPython] N_element027  label="N_element : 0.757"  # scripted group (container) (typed FeaturePython)
  n = 0.035451
FEATURE [App::DocumentObjectGroupPython] O_element067  label="O_element : 0.880"  # scripted group (container) (typed FeaturePython)
  n = 0.710101
FEATURE [App::DocumentObjectGroupPython] G4_MUSCLE_WITH_SUCROSE  # scripted group (container) (typed FeaturePython)
  Dunit = g/cm3
  Dvalue = 1.11
  Group = -> [H_element059,C_element065,N_element027,O_element067]
  conduct = 2
  density = 1
  expand = 3
  formula = G4_MUSCLE_WITH_SUCROSE
  name = G4_MUSCLE_WITH_SUCROSE
  specific = 4
FEATURE [App::DocumentObjectGroupPython] H_element060  label="H_element : 0.138"  # scripted group (container) (typed FeaturePython)
  n = 0.101969
FEATURE [App::DocumentObjectGroupPython] C_element066  label="C_element : 0.120"  # scripted group (container) (typed FeaturePython)
  n = 0.120058
FEATURE [App::DocumentObjectGroupPython] N_element028  label="N_element : 0.758"  # scripted group (container) (typed FeaturePython)
  n = 0.035451
FEATURE [App::DocumentObjectGroupPython] O_element068  label="O_element : 0.743"  # scripted group (container) (typed FeaturePython)
  n = 0.742522
FEATURE [App::DocumentObjectGroupPython] G4_MUSCLE_WITHOUT_SUCROSE  # scripted group (container) (typed FeaturePython)
  Dunit = g/cm3
  Dvalue = 1.07
  Group = -> [H_element060,C_element066,N_element028,O_element068]
  conduct = 2
  density = 1
  expand = 3
  formula = G4_MUSCLE_WITHOUT_SUCROSE
  name = G4_MUSCLE_WITHOUT_SUCROSE
  specific = 4
FEATURE [App::DocumentObjectGroupPython] C_element067  label="C_element : 10"  # scripted group (container) (typed FeaturePython)
  n = 10
  ref = C_element
FEATURE [App::DocumentObjectGroupPython] H_element061  label="H_element : 030"  # scripted group (container) (typed FeaturePython)
  n = 8
  ref = H_element
FEATURE [App::DocumentObjectGroupPython] G4_NAPHTHALENE  # scripted group (container) (typed FeaturePython)
  Dunit = g/cm3
  Dvalue = 1.145
  Group = -> [C_element067,H_element061]
  conduct = 2
  density = 1
  expand = 3
  formula = G4_NAPHTHALENE
  name = G4_NAPHTHALENE
  specific = 4
FEATURE [App::DocumentObjectGroupPython] C_element068  label="C_element : 034"  # scripted group (container) (typed FeaturePython)
  n = 6
  ref = C_element
FEATURE [App::DocumentObjectGroupPython] H_element062  label="H_element : 031"  # scripted group (container) (typed FeaturePython)
  n = 5
  ref = H_element
FEATURE [App::DocumentObjectGroupPython] N_element029  label="N_element : 012"  # scripted group (container) (typed FeaturePython)
  n = 1
  ref = N_element
FEATURE [App::DocumentObjectGroupPython] O_element069  label="O_element : 034"  # scripted group (container) (typed FeaturePython)
  n = 2
  ref = O_element
FEATURE [App::DocumentObjectGroupPython] G4_NITROBENZENE  # scripted group (container) (typed FeaturePython)
  Dunit = g/cm3
  Dvalue = 1.19867
  Group = -> [C_element068,H_element062,N_element029,O_element069]
  conduct = 2
  density = 1
  expand = 3
  formula = G4_NITROBENZENE
  name = G4_NITROBENZENE
  specific = 4
FEATURE [App::DocumentObjectGroupPython] N_element030  label="N_element : 013"  # scripted group (container) (typed FeaturePython)
  n = 2
  ref = N_element
FEATURE [App::DocumentObjectGroupPython] O_element070  label="O_element : 035"  # scripted group (container) (typed FeaturePython)
  n = 1
  ref = O_element
FEATURE [App::DocumentObjectGroupPython] G4_NITROUS_OXIDE  # scripted group (container) (typed FeaturePython)
  Dunit = g/cm3
  Dvalue = 0.00183094
  Group = -> [N_element030,O_element070]
  conduct = 2
  density = 1
  expand = 3
  formula = G4_NITROUS_OXIDE
  name = G4_NITROUS_OXIDE
  specific = 4
FEATURE [App::DocumentObjectGroupPython] H_element063  label="H_element : 0.104"  # scripted group (container) (typed FeaturePython)
  n = 0.103509
FEATURE [App::DocumentObjectGroupPython] C_element069  label="C_element : 0.648"  # scripted group (container) (typed FeaturePython)
  n = 0.648416
FEATURE [App::DocumentObjectGroupPython] N_element031  label="N_element : 0.100"  # scripted group (container) (typed FeaturePython)
  n = 0.0995361
FEATURE [App::DocumentObjectGroupPython] O_element071  label="O_element : 0.149"  # scripted group (container) (typed FeaturePython)
  n = 0.148539
FEATURE [App::DocumentObjectGroupPython] G4_NYLON_8062  label="G4_NYLON-8062"  # scripted group (container) (typed FeaturePython)
  Dunit = g/cm3
  Dvalue = 1.08
  Group = -> [H_element063,C_element069,N_element031,O_element071]
  conduct = 2
  density = 1
  expand = 3
  formula = G4_NYLON-8062
  name = G4_NYLON-8062
  specific = 4
FEATURE [App::DocumentObjectGroupPython] C_element070  label="C_element : 035"  # scripted group (container) (typed FeaturePython)
  n = 6
  ref = C_element
FEATURE [App::DocumentObjectGroupPython] H_element064  label="H_element : 11"  # scripted group (container) (typed FeaturePython)
  n = 11
  ref = H_element
FEATURE [App::DocumentObjectGroupPython] N_element032  label="N_element : 014"  # scripted group (container) (typed FeaturePython)
  n = 1
  ref = N_element
FEATURE [App::DocumentObjectGroupPython] O_element072  label="O_element : 036"  # scripted group (container) (typed FeaturePython)
  n = 1
  ref = O_element
FEATURE [App::DocumentObjectGroupPython] G4_NYLON_6_6  label="G4_NYLON-6-6"  # scripted group (container) (typed FeaturePython)
  Dunit = g/cm3
  Dvalue = 1.14
  Group = -> [C_element070,H_element064,N_element032,O_element072]
  conduct = 2
  density = 1
  expand = 3
  formula = G4_NYLON-6-6
  name = G4_NYLON-6-6
  specific = 4
FEATURE [App::DocumentObjectGroupPython] H_element065  label="H_element : 0.139"  # scripted group (container) (typed FeaturePython)
  n = 0.107062
FEATURE [App::DocumentObjectGroupPython] C_element071  label="C_element : 0.680"  # scripted group (container) (typed FeaturePython)
  n = 0.680449
FEATURE [App::DocumentObjectGroupPython] N_element033  label="N_element : 0.099"  # scripted group (container) (typed FeaturePython)
  n = 0.099189
FEATURE [App::DocumentObjectGroupPython] O_element073  label="O_element : 0.113"  # scripted group (container) (typed FeaturePython)
  n = 0.1133
FEATURE [App::DocumentObjectGroupPython] G4_NYLON_6_10  label="G4_NYLON-6-10"  # scripted group (container) (typed FeaturePython)
  Dunit = g/cm3
  Dvalue = 1.14
  Group = -> [H_element065,C_element071,N_element033,O_element073]
  conduct = 2
  density = 1
  expand = 3
  formula = G4_NYLON-6-10
  name = G4_NYLON-6-10
  specific = 4
FEATURE [App::DocumentObjectGroupPython] H_element066  label="H_element : 0.140"  # scripted group (container) (typed FeaturePython)
  n = 0.115476
FEATURE [App::DocumentObjectGroupPython] C_element072  label="C_element : 0.721"  # scripted group (container) (typed FeaturePython)
  n = 0.720818
FEATURE [App::DocumentObjectGroupPython] N_element034  label="N_element : 0.076"  # scripted group (container) (typed FeaturePython)
  n = 0.0764169
FEATURE [App::DocumentObjectGroupPython] O_element074  label="O_element : 0.087"  # scripted group (container) (typed FeaturePython)
  n = 0.0872889
FEATURE [App::DocumentObjectGroupPython] G4_NYLON_11_RILSAN  label="G4_NYLON-11_RILSAN"  # scripted group (container) (typed FeaturePython)
  Dunit = g/cm3
  Dvalue = 1.425
  Group = -> [H_element066,C_element072,N_element034,O_element074]
  conduct = 2
  density = 1
  expand = 3
  formula = G4_NYLON-11_RILSAN
  name = G4_NYLON-11_RILSAN
  specific = 4
FEATURE [App::DocumentObjectGroupPython] C_element073  label="C_element : 8"  # scripted group (container) (typed FeaturePython)
  n = 8
  ref = C_element
FEATURE [App::DocumentObjectGroupPython] H_element067  label="H_element : 18"  # scripted group (container) (typed FeaturePython)
  n = 18
  ref = H_element
FEATURE [App::DocumentObjectGroupPython] G4_OCTANE  # scripted group (container) (typed FeaturePython)
  Dunit = g/cm3
  Dvalue = 0.7026
  Group = -> [C_element073,H_element067]
  conduct = 2
  density = 1
  expand = 3
  formula = G4_OCTANE
  name = G4_OCTANE
  specific = 4
FEATURE [App::DocumentObjectGroupPython] C_element074  label="C_element : 25"  # scripted group (container) (typed FeaturePython)
  n = 25
  ref = C_element
FEATURE [App::DocumentObjectGroupPython] H_element068  label="H_element : 52"  # scripted group (container) (typed FeaturePython)
  n = 52
  ref = H_element
FEATURE [App::DocumentObjectGroupPython] G4_PARAFFIN  # scripted group (container) (typed FeaturePython)
  Dunit = g/cm3
  Dvalue = 0.93
  Group = -> [C_element074,H_element068]
  conduct = 2
  density = 1
  expand = 3
  formula = G4_PARAFFIN
  name = G4_PARAFFIN
  specific = 4
FEATURE [App::DocumentObjectGroupPython] C_element075  label="C_element : 036"  # scripted group (container) (typed FeaturePython)
  n = 5
  ref = C_element
FEATURE [App::DocumentObjectGroupPython] H_element069  label="H_element : 032"  # scripted group (container) (typed FeaturePython)
  n = 12
  ref = H_element
FEATURE [App::DocumentObjectGroupPython] G4_N_PENTANE  label="G4_N-PENTANE"  # scripted group (container) (typed FeaturePython)
  Dunit = g/cm3
  Dvalue = 0.6262
  Group = -> [C_element075,H_element069]
  conduct = 2
  density = 1
  expand = 3
  formula = G4_N-PENTANE
  name = G4_N-PENTANE
  specific = 4
FEATURE [App::DocumentObjectGroupPython] H_element070  label="H_element : 0.014"  # scripted group (container) (typed FeaturePython)
  n = 0.0141
FEATURE [App::DocumentObjectGroupPython] C_element076  label="C_element : 0.072"  # scripted group (container) (typed FeaturePython)
  n = 0.072261
FEATURE [App::DocumentObjectGroupPython] N_element035  label="N_element : 0.019"  # scripted group (container) (typed FeaturePython)
  n = 0.01932
FEATURE [App::DocumentObjectGroupPython] O_element075  label="O_element : 0.066"  # scripted group (container) (typed FeaturePython)
  n = 0.066101
FEATURE [App::DocumentObjectGroupPython] S_element019  label="S_element : 0.020"  # scripted group (container) (typed FeaturePython)
  n = 0.00189
FEATURE [App::DocumentObjectGroupPython] Br_element004  label="Br_element : 0.349"  # scripted group (container) (typed FeaturePython)
  n = 0.349103
FEATURE [App::DocumentObjectGroupPython] Ag_element001  label="Ag_element : 0.474"  # scripted group (container) (typed FeaturePython)
  n = 0.474105
FEATURE [App::DocumentObjectGroupPython] I_element005  label="I_element : 0.003"  # scripted group (container) (typed FeaturePython)
  n = 0.00312
FEATURE [App::DocumentObjectGroupPython] G4_PHOTO_EMULSION  # scripted group (container) (typed FeaturePython)
  Dunit = g/cm3
  Dvalue = 3.815
  Group = -> [H_element070,C_element076,N_element035,O_element075,S_element019,Br_element004,Ag_element001,I_element005]
  conduct = 2
  density = 1
  expand = 3
  formula = G4_PHOTO_EMULSION
  name = G4_PHOTO_EMULSION
  specific = 4
FEATURE [App::DocumentObjectGroupPython] C_element077  label="C_element : 9"  # scripted group (container) (typed FeaturePython)
  n = 9
  ref = C_element
FEATURE [App::DocumentObjectGroupPython] H_element071  label="H_element : 033"  # scripted group (container) (typed FeaturePython)
  n = 10
  ref = H_element
FEATURE [App::DocumentObjectGroupPython] G4_PLASTIC_SC_VINYLTOLUENE  # scripted group (container) (typed FeaturePython)
  Dunit = g/cm3
  Dvalue = 1.032
  Group = -> [C_element077,H_element071]
  conduct = 2
  density = 1
  expand = 3
  formula = G4_PLASTIC_SC_VINYLTOLUENE
  name = G4_PLASTIC_SC_VINYLTOLUENE
  specific = 4
FEATURE [App::DocumentObjectGroupPython] Pu_element001  label="Pu_element : 1"  # scripted group (container) (typed FeaturePython)
  n = 1
  ref = Pu_element
FEATURE [App::DocumentObjectGroupPython] O_element076  label="O_element : 037"  # scripted group (container) (typed FeaturePython)
  n = 2
  ref = O_element
FEATURE [App::DocumentObjectGroupPython] G4_PLUTONIUM_DIOXIDE  # scripted group (container) (typed FeaturePython)
  Dunit = g/cm3
  Dvalue = 11.46
  Group = -> [Pu_element001,O_element076]
  conduct = 2
  density = 1
  expand = 3
  formula = G4_PLUTONIUM_DIOXIDE
  name = G4_PLUTONIUM_DIOXIDE
  specific = 4
FEATURE [App::DocumentObjectGroupPython] C_element078  label="C_element : 037"  # scripted group (container) (typed FeaturePython)
  n = 3
  ref = C_element
FEATURE [App::DocumentObjectGroupPython] H_element072  label="H_element : 034"  # scripted group (container) (typed FeaturePython)
  n = 3
  ref = H_element
FEATURE [App::DocumentObjectGroupPython] N_element036  label="N_element : 015"  # scripted group (container) (typed FeaturePython)
  n = 1
  ref = N_element
FEATURE [App::DocumentObjectGroupPython] G4_POLYACRYLONITRILE  # scripted group (container) (typed FeaturePython)
  Dunit = g/cm3
  Dvalue = 1.17
  Group = -> [C_element078,H_element072,N_element036]
  conduct = 2
  density = 1
  expand = 3
  formula = G4_POLYACRYLONITRILE
  name = G4_POLYACRYLONITRILE
  specific = 4
FEATURE [App::DocumentObjectGroupPython] C_element079  label="C_element : 16"  # scripted group (container) (typed FeaturePython)
  n = 16
  ref = C_element
FEATURE [App::DocumentObjectGroupPython] H_element073  label="H_element : 035"  # scripted group (container) (typed FeaturePython)
  n = 14
  ref = H_element
FEATURE [App::DocumentObjectGroupPython] O_element077  label="O_element : 038"  # scripted group (container) (typed FeaturePython)
  n = 3
  ref = O_element
FEATURE [App::DocumentObjectGroupPython] G4_POLYCARBONATE  # scripted group (container) (typed FeaturePython)
  Dunit = g/cm3
  Dvalue = 1.2
  Group = -> [C_element079,H_element073,O_element077]
  conduct = 2
  density = 1
  expand = 3
  formula = G4_POLYCARBONATE
  name = G4_POLYCARBONATE
  specific = 4
FEATURE [App::DocumentObjectGroupPython] C_element080  label="C_element : 038"  # scripted group (container) (typed FeaturePython)
  n = 8
  ref = C_element
FEATURE [App::DocumentObjectGroupPython] H_element074  label="H_element : 036"  # scripted group (container) (typed FeaturePython)
  n = 7
  ref = H_element
FEATURE [App::DocumentObjectGroupPython] Cl_element017  label="Cl_element : 007"  # scripted group (container) (typed FeaturePython)
  n = 1
  ref = Cl_element
FEATURE [App::DocumentObjectGroupPython] G4_POLYCHLOROSTYRENE  # scripted group (container) (typed FeaturePython)
  Dunit = g/cm3
  Dvalue = 1.3
  Group = -> [C_element080,H_element074,Cl_element017]
  conduct = 2
  density = 1
  expand = 3
  formula = G4_POLYCHLOROSTYRENE
  name = G4_POLYCHLOROSTYRENE
  specific = 4
FEATURE [App::DocumentObjectGroupPython] C_element081  label="C_element : 039"  # scripted group (container) (typed FeaturePython)
  n = 1
  ref = C_element
FEATURE [App::DocumentObjectGroupPython] H_element075  label="H_element : 037"  # scripted group (container) (typed FeaturePython)
  n = 2
  ref = H_element
FEATURE [App::DocumentObjectGroupPython] G4_POLYETHYLENE  # scripted group (container) (typed FeaturePython)
  Dunit = g/cm3
  Dvalue = 0.94
  Group = -> [C_element081,H_element075]
  conduct = 2
  density = 1
  expand = 3
  formula = G4_POLYETHYLENE
  name = G4_POLYETHYLENE
  specific = 4
FEATURE [App::DocumentObjectGroupPython] C_element082  label="C_element : 040"  # scripted group (container) (typed FeaturePython)
  n = 10
  ref = C_element
FEATURE [App::DocumentObjectGroupPython] H_element076  label="H_element : 038"  # scripted group (container) (typed FeaturePython)
  n = 8
  ref = H_element
FEATURE [App::DocumentObjectGroupPython] O_element078  label="O_element : 039"  # scripted group (container) (typed FeaturePython)
  n = 4
  ref = O_element
FEATURE [App::DocumentObjectGroupPython] G4_MYLAR  # scripted group (container) (typed FeaturePython)
  Dunit = g/cm3
  Dvalue = 1.4
  Group = -> [C_element082,H_element076,O_element078]
  conduct = 2
  density = 1
  expand = 3
  formula = G4_MYLAR
  name = G4_MYLAR
  specific = 4
FEATURE [App::DocumentObjectGroupPython] C_element083  label="C_element : 041"  # scripted group (container) (typed FeaturePython)
  n = 5
  ref = C_element
FEATURE [App::DocumentObjectGroupPython] H_element077  label="H_element : 039"  # scripted group (container) (typed FeaturePython)
  n = 8
  ref = H_element
FEATURE [App::DocumentObjectGroupPython] O_element079  label="O_element : 040"  # scripted group (container) (typed FeaturePython)
  n = 2
  ref = O_element
FEATURE [App::DocumentObjectGroupPython] G4_PLEXIGLASS  # scripted group (container) (typed FeaturePython)
  Dunit = g/cm3
  Dvalue = 1.19
  Group = -> [C_element083,H_element077,O_element079]
  conduct = 2
  density = 1
  expand = 3
  formula = G4_PLEXIGLASS
  name = G4_PLEXIGLASS
  specific = 4
FEATURE [App::DocumentObjectGroupPython] C_element084  label="C_element : 042"  # scripted group (container) (typed FeaturePython)
  n = 1
  ref = C_element
FEATURE [App::DocumentObjectGroupPython] H_element078  label="H_element : 040"  # scripted group (container) (typed FeaturePython)
  n = 2
  ref = H_element
FEATURE [App::DocumentObjectGroupPython] O_element080  label="O_element : 041"  # scripted group (container) (typed FeaturePython)
  n = 1
  ref = O_element
FEATURE [App::DocumentObjectGroupPython] G4_POLYOXYMETHYLENE  # scripted group (container) (typed FeaturePython)
  Dunit = g/cm3
  Dvalue = 1.425
  Group = -> [C_element084,H_element078,O_element080]
  conduct = 2
  density = 1
  expand = 3
  formula = G4_POLYOXYMETHYLENE
  name = G4_POLYOXYMETHYLENE
  specific = 4
FEATURE [App::DocumentObjectGroupPython] C_element085  label="C_element : 043"  # scripted group (container) (typed FeaturePython)
  n = 2
  ref = C_element
FEATURE [App::DocumentObjectGroupPython] H_element079  label="H_element : 041"  # scripted group (container) (typed FeaturePython)
  n = 4
  ref = H_element
FEATURE [App::DocumentObjectGroupPython] G4_POLYPROPYLENE  # scripted group (container) (typed FeaturePython)
  Dunit = g/cm3
  Dvalue = 0.9
  Group = -> [C_element085,H_element079]
  conduct = 2
  density = 1
  expand = 3
  formula = G4_POLYPROPYLENE
  name = G4_POLYPROPYLENE
  specific = 4
FEATURE [App::DocumentObjectGroupPython] C_element086  label="C_element : 044"  # scripted group (container) (typed FeaturePython)
  n = 8
  ref = C_element
FEATURE [App::DocumentObjectGroupPython] H_element080  label="H_element : 042"  # scripted group (container) (typed FeaturePython)
  n = 8
  ref = H_element
FEATURE [App::DocumentObjectGroupPython] G4_POLYSTYRENE  # scripted group (container) (typed FeaturePython)
  Dunit = g/cm3
  Dvalue = 1.06
  Group = -> [C_element086,H_element080]
  conduct = 2
  density = 1
  expand = 3
  formula = G4_POLYSTYRENE
  name = G4_POLYSTYRENE
  specific = 4
FEATURE [App::DocumentObjectGroupPython] C_element087  label="C_element : 045"  # scripted group (container) (typed FeaturePython)
  n = 2
  ref = C_element
FEATURE [App::DocumentObjectGroupPython] F_element014  label="F_element : 4"  # scripted group (container) (typed FeaturePython)
  n = 4
  ref = F_element
FEATURE [App::DocumentObjectGroupPython] G4_TEFLON  # scripted group (container) (typed FeaturePython)
  Dunit = g/cm3
  Dvalue = 2.2
  Group = -> [C_element087,F_element014]
  conduct = 2
  density = 1
  expand = 3
  formula = G4_TEFLON
  name = G4_TEFLON
  specific = 4
FEATURE [App::DocumentObjectGroupPython] C_element088  label="C_element : 046"  # scripted group (container) (typed FeaturePython)
  n = 2
  ref = C_element
FEATURE [App::DocumentObjectGroupPython] F_element015  label="F_element : 006"  # scripted group (container) (typed FeaturePython)
  n = 3
  ref = F_element
FEATURE [App::DocumentObjectGroupPython] Cl_element018  label="Cl_element : 008"  # scripted group (container) (typed FeaturePython)
  n = 1
  ref = Cl_element
FEATURE [App::DocumentObjectGroupPython] G4_POLYTRIFLUOROCHLOROETHYLENE  # scripted group (container) (typed FeaturePython)
  Dunit = g/cm3
  Dvalue = 2.1
  Group = -> [C_element088,F_element015,Cl_element018]
  conduct = 2
  density = 1
  expand = 3
  formula = G4_POLYTRIFLUOROCHLOROETHYLENE
  name = G4_POLYTRIFLUOROCHLOROETHYLENE
  specific = 4
FEATURE [App::DocumentObjectGroupPython] C_element089  label="C_element : 047"  # scripted group (container) (typed FeaturePython)
  n = 4
  ref = C_element
FEATURE [App::DocumentObjectGroupPython] H_element081  label="H_element : 043"  # scripted group (container) (typed FeaturePython)
  n = 6
  ref = H_element
FEATURE [App::DocumentObjectGroupPython] O_element081  label="O_element : 042"  # scripted group (container) (typed FeaturePython)
  n = 2
  ref = O_element
FEATURE [App::DocumentObjectGroupPython] G4_POLYVINYL_ACETATE  # scripted group (container) (typed FeaturePython)
  Dunit = g/cm3
  Dvalue = 1.19
  Group = -> [C_element089,H_element081,O_element081]
  conduct = 2
  density = 1
  expand = 3
  formula = G4_POLYVINYL_ACETATE
  name = G4_POLYVINYL_ACETATE
  specific = 4
FEATURE [App::DocumentObjectGroupPython] C_element090  label="C_element : 048"  # scripted group (container) (typed FeaturePython)
  n = 2
  ref = C_element
FEATURE [App::DocumentObjectGroupPython] H_element082  label="H_element : 044"  # scripted group (container) (typed FeaturePython)
  n = 4
  ref = H_element
FEATURE [App::DocumentObjectGroupPython] O_element082  label="O_element : 043"  # scripted group (container) (typed FeaturePython)
  n = 1
  ref = O_element
FEATURE [App::DocumentObjectGroupPython] G4_POLYVINYL_ALCOHOL  # scripted group (container) (typed FeaturePython)
  Dunit = g/cm3
  Dvalue = 1.3
  Group = -> [C_element090,H_element082,O_element082]
  conduct = 2
  density = 1
  expand = 3
  formula = G4_POLYVINYL_ALCOHOL
  name = G4_POLYVINYL_ALCOHOL
  specific = 4
FEATURE [App::DocumentObjectGroupPython] C_element091  label="C_element : 049"  # scripted group (container) (typed FeaturePython)
  n = 8
  ref = C_element
FEATURE [App::DocumentObjectGroupPython] H_element083  label="H_element : 045"  # scripted group (container) (typed FeaturePython)
  n = 14
  ref = H_element
FEATURE [App::DocumentObjectGroupPython] O_element083  label="O_element : 044"  # scripted group (container) (typed FeaturePython)
  n = 2
  ref = O_element
FEATURE [App::DocumentObjectGroupPython] G4_POLYVINYL_BUTYRAL  # scripted group (container) (typed FeaturePython)
  Dunit = g/cm3
  Dvalue = 1.12
  Group = -> [C_element091,H_element083,O_element083]
  conduct = 2
  density = 1
  expand = 3
  formula = G4_POLYVINYL_BUTYRAL
  name = G4_POLYVINYL_BUTYRAL
  specific = 4
FEATURE [App::DocumentObjectGroupPython] C_element092  label="C_element : 050"  # scripted group (container) (typed FeaturePython)
  n = 2
  ref = C_element
FEATURE [App::DocumentObjectGroupPython] H_element084  label="H_element : 046"  # scripted group (container) (typed FeaturePython)
  n = 3
  ref = H_element
FEATURE [App::DocumentObjectGroupPython] Cl_element019  label="Cl_element : 009"  # scripted group (container) (typed FeaturePython)
  n = 1
  ref = Cl_element
FEATURE [App::DocumentObjectGroupPython] G4_POLYVINYL_CHLORIDE  # scripted group (container) (typed FeaturePython)
  Dunit = g/cm3
  Dvalue = 1.3
  Group = -> [C_element092,H_element084,Cl_element019]
  conduct = 2
  density = 1
  expand = 3
  formula = G4_POLYVINYL_CHLORIDE
  name = G4_POLYVINYL_CHLORIDE
  specific = 4
FEATURE [App::DocumentObjectGroupPython] C_element093  label="C_element : 051"  # scripted group (container) (typed FeaturePython)
  n = 2
  ref = C_element
FEATURE [App::DocumentObjectGroupPython] H_element085  label="H_element : 047"  # scripted group (container) (typed FeaturePython)
  n = 2
  ref = H_element
FEATURE [App::DocumentObjectGroupPython] Cl_element020  label="Cl_element : 010"  # scripted group (container) (typed FeaturePython)
  n = 2
  ref = Cl_element
FEATURE [App::DocumentObjectGroupPython] G4_POLYVINYLIDENE_CHLORIDE  # scripted group (container) (typed FeaturePython)
  Dunit = g/cm3
  Dvalue = 1.7
  Group = -> [C_element093,H_element085,Cl_element020]
  conduct = 2
  density = 1
  expand = 3
  formula = G4_POLYVINYLIDENE_CHLORIDE
  name = G4_POLYVINYLIDENE_CHLORIDE
  specific = 4
FEATURE [App::DocumentObjectGroupPython] C_element094  label="C_element : 052"  # scripted group (container) (typed FeaturePython)
  n = 2
  ref = C_element
FEATURE [App::DocumentObjectGroupPython] H_element086  label="H_element : 048"  # scripted group (container) (typed FeaturePython)
  n = 2
  ref = H_element
FEATURE [App::DocumentObjectGroupPython] F_element016  label="F_element : 007"  # scripted group (container) (typed FeaturePython)
  n = 2
  ref = F_element
FEATURE [App::DocumentObjectGroupPython] G4_POLYVINYLIDENE_FLUORIDE  # scripted group (container) (typed FeaturePython)
  Dunit = g/cm3
  Dvalue = 1.76
  Group = -> [C_element094,H_element086,F_element016]
  conduct = 2
  density = 1
  expand = 3
  formula = G4_POLYVINYLIDENE_FLUORIDE
  name = G4_POLYVINYLIDENE_FLUORIDE
  specific = 4
FEATURE [App::DocumentObjectGroupPython] C_element095  label="C_element : 053"  # scripted group (container) (typed FeaturePython)
  n = 6
  ref = C_element
FEATURE [App::DocumentObjectGroupPython] H_element087  label="H_element : 9"  # scripted group (container) (typed FeaturePython)
  n = 9
  ref = H_element
FEATURE [App::DocumentObjectGroupPython] N_element037  label="N_element : 016"  # scripted group (container) (typed FeaturePython)
  n = 1
  ref = N_element
FEATURE [App::DocumentObjectGroupPython] O_element084  label="O_element : 045"  # scripted group (container) (typed FeaturePython)
  n = 1
  ref = O_element
FEATURE [App::DocumentObjectGroupPython] G4_POLYVINYL_PYRROLIDONE  # scripted group (container) (typed FeaturePython)
  Dunit = g/cm3
  Dvalue = 1.25
  Group = -> [C_element095,H_element087,N_element037,O_element084]
  conduct = 2
  density = 1
  expand = 3
  formula = G4_POLYVINYL_PYRROLIDONE
  name = G4_POLYVINYL_PYRROLIDONE
  specific = 4
FEATURE [App::DocumentObjectGroupPython] K_element008  label="K_element : 1"  # scripted group (container) (typed FeaturePython)
  n = 1
  ref = K_element
FEATURE [App::DocumentObjectGroupPython] I_element006  label="I_element : 003"  # scripted group (container) (typed FeaturePython)
  n = 1
  ref = I_element
FEATURE [App::DocumentObjectGroupPython] G4_POTASSIUM_IODIDE  # scripted group (container) (typed FeaturePython)
  Dunit = g/cm3
  Dvalue = 3.13
  Group = -> [K_element008,I_element006]
  conduct = 2
  density = 1
  expand = 3
  formula = G4_POTASSIUM_IODIDE
  name = G4_POTASSIUM_IODIDE
  specific = 4
FEATURE [App::DocumentObjectGroupPython] K_element009  label="K_element : 2"  # scripted group (container) (typed FeaturePython)
  n = 2
  ref = K_element
FEATURE [App::DocumentObjectGroupPython] O_element085  label="O_element : 046"  # scripted group (container) (typed FeaturePython)
  n = 1
  ref = O_element
FEATURE [App::DocumentObjectGroupPython] G4_POTASSIUM_OXIDE  # scripted group (container) (typed FeaturePython)
  Dunit = g/cm3
  Dvalue = 2.32
  Group = -> [K_element009,O_element085]
  conduct = 2
  density = 1
  expand = 3
  formula = G4_POTASSIUM_OXIDE
  name = G4_POTASSIUM_OXIDE
  specific = 4
FEATURE [App::DocumentObjectGroupPython] C_element096  label="C_element : 054"  # scripted group (container) (typed FeaturePython)
  n = 3
  ref = C_element
FEATURE [App::DocumentObjectGroupPython] H_element088  label="H_element : 049"  # scripted group (container) (typed FeaturePython)
  n = 8
  ref = H_element
FEATURE [App::DocumentObjectGroupPython] G4_PROPANE  # scripted group (container) (typed FeaturePython)
  Dunit = g/cm3
  Dvalue = 0.00187939
  Group = -> [C_element096,H_element088]
  conduct = 2
  density = 1
  expand = 3
  formula = G4_PROPANE
  name = G4_PROPANE
  specific = 4
FEATURE [App::DocumentObjectGroupPython] C_element097  label="C_element : 055"  # scripted group (container) (typed FeaturePython)
  n = 3
  ref = C_element
FEATURE [App::DocumentObjectGroupPython] H_element089  label="H_element : 050"  # scripted group (container) (typed FeaturePython)
  n = 8
  ref = H_element
FEATURE [App::DocumentObjectGroupPython] G4_lPROPANE  # scripted group (container) (typed FeaturePython)
  Dunit = g/cm3
  Dvalue = 0.43
  Group = -> [C_element097,H_element089]
  conduct = 2
  density = 1
  expand = 3
  formula = G4_lPROPANE
  name = G4_lPROPANE
  specific = 4
FEATURE [App::DocumentObjectGroupPython] C_element098  label="C_element : 056"  # scripted group (container) (typed FeaturePython)
  n = 3
  ref = C_element
FEATURE [App::DocumentObjectGroupPython] H_element090  label="H_element : 051"  # scripted group (container) (typed FeaturePython)
  n = 8
  ref = H_element
FEATURE [App::DocumentObjectGroupPython] O_element086  label="O_element : 047"  # scripted group (container) (typed FeaturePython)
  n = 1
  ref = O_element
FEATURE [App::DocumentObjectGroupPython] G4_N_PROPYL_ALCOHOL  label="G4_N-PROPYL_ALCOHOL"  # scripted group (container) (typed FeaturePython)
  Dunit = g/cm3
  Dvalue = 0.8035
  Group = -> [C_element098,H_element090,O_element086]
  conduct = 2
  density = 1
  expand = 3
  formula = G4_N-PROPYL_ALCOHOL
  name = G4_N-PROPYL_ALCOHOL
  specific = 4
FEATURE [App::DocumentObjectGroupPython] C_element099  label="C_element : 057"  # scripted group (container) (typed FeaturePython)
  n = 5
  ref = C_element
FEATURE [App::DocumentObjectGroupPython] H_element091  label="H_element : 052"  # scripted group (container) (typed FeaturePython)
  n = 5
  ref = H_element
FEATURE [App::DocumentObjectGroupPython] N_element038  label="N_element : 017"  # scripted group (container) (typed FeaturePython)
  n = 1
  ref = N_element
FEATURE [App::DocumentObjectGroupPython] G4_PYRIDINE  # scripted group (container) (typed FeaturePython)
  Dunit = g/cm3
  Dvalue = 0.9819
  Group = -> [C_element099,H_element091,N_element038]
  conduct = 2
  density = 1
  expand = 3
  formula = G4_PYRIDINE
  name = G4_PYRIDINE
  specific = 4
FEATURE [App::DocumentObjectGroupPython] H_element092  label="H_element : 0.144"  # scripted group (container) (typed FeaturePython)
  n = 0.143711
FEATURE [App::DocumentObjectGroupPython] C_element100  label="C_element : 0.856"  # scripted group (container) (typed FeaturePython)
  n = 0.856289
FEATURE [App::DocumentObjectGroupPython] G4_RUBBER_BUTYL  # scripted group (container) (typed FeaturePython)
  Dunit = g/cm3
  Dvalue = 0.92
  Group = -> [H_element092,C_element100]
  conduct = 2
  density = 1
  expand = 3
  formula = G4_RUBBER_BUTYL
  name = G4_RUBBER_BUTYL
  specific = 4
FEATURE [App::DocumentObjectGroupPython] H_element093  label="H_element : 0.118"  # scripted group (container) (typed FeaturePython)
  n = 0.118371
FEATURE [App::DocumentObjectGroupPython] C_element101  label="C_element : 0.882"  # scripted group (container) (typed FeaturePython)
  n = 0.881629
FEATURE [App::DocumentObjectGroupPython] G4_RUBBER_NATURAL  # scripted group (container) (typed FeaturePython)
  Dunit = g/cm3
  Dvalue = 0.92
  Group = -> [H_element093,C_element101]
  conduct = 2
  density = 1
  expand = 3
  formula = G4_RUBBER_NATURAL
  name = G4_RUBBER_NATURAL
  specific = 4
FEATURE [App::DocumentObjectGroupPython] H_element094  label="H_element : 0.145"  # scripted group (container) (typed FeaturePython)
  n = 0.05692
FEATURE [App::DocumentObjectGroupPython] C_element102  label="C_element : 0.543"  # scripted group (container) (typed FeaturePython)
  n = 0.542646
FEATURE [App::DocumentObjectGroupPython] Cl_element021  label="Cl_element : 0.400"  # scripted group (container) (typed FeaturePython)
  n = 0.400434
FEATURE [App::DocumentObjectGroupPython] G4_RUBBER_NEOPRENE  # scripted group (container) (typed FeaturePython)
  Dunit = g/cm3
  Dvalue = 1.23
  Group = -> [H_element094,C_element102,Cl_element021]
  conduct = 2
  density = 1
  expand = 3
  formula = G4_RUBBER_NEOPRENE
  name = G4_RUBBER_NEOPRENE
  specific = 4
FEATURE [App::DocumentObjectGroupPython] Si_element006  label="Si_element : 1"  # scripted group (container) (typed FeaturePython)
  n = 1
  ref = Si_element
FEATURE [App::DocumentObjectGroupPython] O_element087  label="O_element : 048"  # scripted group (container) (typed FeaturePython)
  n = 2
  ref = O_element
FEATURE [App::DocumentObjectGroupPython] G4_SILICON_DIOXIDE  # scripted group (container) (typed FeaturePython)
  Dunit = g/cm3
  Dvalue = 2.32
  Group = -> [Si_element006,O_element087]
  conduct = 2
  density = 1
  expand = 3
  formula = G4_SILICON_DIOXIDE
  name = G4_SILICON_DIOXIDE
  specific = 4
FEATURE [App::DocumentObjectGroupPython] Ag_element002  label="Ag_element : 1"  # scripted group (container) (typed FeaturePython)
  n = 1
  ref = Ag_element
FEATURE [App::DocumentObjectGroupPython] Br_element005  label="Br_element : 003"  # scripted group (container) (typed FeaturePython)
  n = 1
  ref = Br_element
FEATURE [App::DocumentObjectGroupPython] G4_SILVER_BROMIDE  # scripted group (container) (typed FeaturePython)
  Dunit = g/cm3
  Dvalue = 6.473
  Group = -> [Ag_element002,Br_element005]
  conduct = 2
  density = 1
  expand = 3
  formula = G4_SILVER_BROMIDE
  name = G4_SILVER_BROMIDE
  specific = 4
FEATURE [App::DocumentObjectGroupPython] Ag_element003  label="Ag_element : 002"  # scripted group (container) (typed FeaturePython)
  n = 1
  ref = Ag_element
FEATURE [App::DocumentObjectGroupPython] Cl_element022  label="Cl_element : 011"  # scripted group (container) (typed FeaturePython)
  n = 1
  ref = Cl_element
FEATURE [App::DocumentObjectGroupPython] G4_SILVER_CHLORIDE  # scripted group (container) (typed FeaturePython)
  Dunit = g/cm3
  Dvalue = 5.56
  Group = -> [Ag_element003,Cl_element022]
  conduct = 2
  density = 1
  expand = 3
  formula = G4_SILVER_CHLORIDE
  name = G4_SILVER_CHLORIDE
  specific = 4
FEATURE [App::DocumentObjectGroupPython] Br_element006  label="Br_element : 0.423"  # scripted group (container) (typed FeaturePython)
  n = 0.422895
FEATURE [App::DocumentObjectGroupPython] Ag_element004  label="Ag_element : 0.574"  # scripted group (container) (typed FeaturePython)
  n = 0.573748
FEATURE [App::DocumentObjectGroupPython] I_element007  label="I_element : 0.649"  # scripted group (container) (typed FeaturePython)
  n = 0.003357
FEATURE [App::DocumentObjectGroupPython] G4_SILVER_HALIDES  # scripted group (container) (typed FeaturePython)
  Dunit = g/cm3
  Dvalue = 6.47
  Group = -> [Br_element006,Ag_element004,I_element007]
  conduct = 2
  density = 1
  expand = 3
  formula = G4_SILVER_HALIDES
  name = G4_SILVER_HALIDES
  specific = 4
FEATURE [App::DocumentObjectGroupPython] Ag_element005  label="Ag_element : 003"  # scripted group (container) (typed FeaturePython)
  n = 1
  ref = Ag_element
FEATURE [App::DocumentObjectGroupPython] I_element008  label="I_element : 004"  # scripted group (container) (typed FeaturePython)
  n = 1
  ref = I_element
FEATURE [App::DocumentObjectGroupPython] G4_SILVER_IODIDE  # scripted group (container) (typed FeaturePython)
  Dunit = g/cm3
  Dvalue = 6.01
  Group = -> [Ag_element005,I_element008]
  conduct = 2
  density = 1
  expand = 3
  formula = G4_SILVER_IODIDE
  name = G4_SILVER_IODIDE
  specific = 4
FEATURE [App::DocumentObjectGroupPython] H_element095  label="H_element : 0.100"  # scripted group (container) (typed FeaturePython)
  n = 0.1
FEATURE [App::DocumentObjectGroupPython] C_element103  label="C_element : 0.204"  # scripted group (container) (typed FeaturePython)
  n = 0.204
FEATURE [App::DocumentObjectGroupPython] N_element039  label="N_element : 0.759"  # scripted group (container) (typed FeaturePython)
  n = 0.042
FEATURE [App::DocumentObjectGroupPython] O_element088  label="O_element : 0.645"  # scripted group (container) (typed FeaturePython)
  n = 0.645
FEATURE [App::DocumentObjectGroupPython] Na_element013  label="Na_element : 0.100"  # scripted group (container) (typed FeaturePython)
  n = 0.002
FEATURE [App::DocumentObjectGroupPython] P_element009  label="P_element : 0.107"  # scripted group (container) (typed FeaturePython)
  n = 0.001
FEATURE [App::DocumentObjectGroupPython] S_element020  label="S_element : 0.021"  # scripted group (container) (typed FeaturePython)
  n = 0.002
FEATURE [App::DocumentObjectGroupPython] Cl_element023  label="Cl_element : 0.590"  # scripted group (container) (typed FeaturePython)
  n = 0.003
FEATURE [App::DocumentObjectGroupPython] K_element010  label="K_element : 0.001"  # scripted group (container) (typed FeaturePython)
  n = 0.001
FEATURE [App::DocumentObjectGroupPython] G4_SKIN_ICRP  # scripted group (container) (typed FeaturePython)
  Dunit = g/cm3
  Dvalue = 1.09
  Group = -> [H_element095,C_element103,N_element039,O_element088,Na_element013,P_element009,S_element020,Cl_element023,K_element010]
  conduct = 2
  density = 1
  expand = 3
  formula = G4_SKIN_ICRP
  name = G4_SKIN_ICRP
  specific = 4
FEATURE [App::DocumentObjectGroupPython] Na_element014  label="Na_element : 2"  # scripted group (container) (typed FeaturePython)
  n = 2
  ref = Na_element
FEATURE [App::DocumentObjectGroupPython] C_element104  label="C_element : 058"  # scripted group (container) (typed FeaturePython)
  n = 1
  ref = C_element
FEATURE [App::DocumentObjectGroupPython] O_element089  label="O_element : 049"  # scripted group (container) (typed FeaturePython)
  n = 3
  ref = O_element
FEATURE [App::DocumentObjectGroupPython] G4_SODIUM_CARBONATE  # scripted group (container) (typed FeaturePython)
  Dunit = g/cm3
  Dvalue = 2.532
  Group = -> [Na_element014,C_element104,O_element089]
  conduct = 2
  density = 1
  expand = 3
  formula = G4_SODIUM_CARBONATE
  name = G4_SODIUM_CARBONATE
  specific = 4
FEATURE [App::DocumentObjectGroupPython] Na_element015  label="Na_element : 1"  # scripted group (container) (typed FeaturePython)
  n = 1
  ref = Na_element
FEATURE [App::DocumentObjectGroupPython] I_element009  label="I_element : 005"  # scripted group (container) (typed FeaturePython)
  n = 1
  ref = I_element
FEATURE [App::DocumentObjectGroupPython] G4_SODIUM_IODIDE  # scripted group (container) (typed FeaturePython)
  Dunit = g/cm3
  Dvalue = 3.667
  Group = -> [Na_element015,I_element009]
  conduct = 2
  density = 1
  expand = 3
  formula = G4_SODIUM_IODIDE
  name = G4_SODIUM_IODIDE
  specific = 4
FEATURE [App::DocumentObjectGroupPython] Na_element016  label="Na_element : 003"  # scripted group (container) (typed FeaturePython)
  n = 2
  ref = Na_element
FEATURE [App::DocumentObjectGroupPython] O_element090  label="O_element : 050"  # scripted group (container) (typed FeaturePython)
  n = 1
  ref = O_element
FEATURE [App::DocumentObjectGroupPython] G4_SODIUM_MONOXIDE  # scripted group (container) (typed FeaturePython)
  Dunit = g/cm3
  Dvalue = 2.27
  Group = -> [Na_element016,O_element090]
  conduct = 2
  density = 1
  expand = 3
  formula = G4_SODIUM_MONOXIDE
  name = G4_SODIUM_MONOXIDE
  specific = 4
FEATURE [App::DocumentObjectGroupPython] Na_element017  label="Na_element : 004"  # scripted group (container) (typed FeaturePython)
  n = 1
  ref = Na_element
FEATURE [App::DocumentObjectGroupPython] N_element040  label="N_element : 018"  # scripted group (container) (typed FeaturePython)
  n = 1
  ref = N_element
FEATURE [App::DocumentObjectGroupPython] O_element091  label="O_element : 051"  # scripted group (container) (typed FeaturePython)
  n = 3
  ref = O_element
FEATURE [App::DocumentObjectGroupPython] G4_SODIUM_NITRATE  # scripted group (container) (typed FeaturePython)
  Dunit = g/cm3
  Dvalue = 2.261
  Group = -> [Na_element017,N_element040,O_element091]
  conduct = 2
  density = 1
  expand = 3
  formula = G4_SODIUM_NITRATE
  name = G4_SODIUM_NITRATE
  specific = 4
FEATURE [App::DocumentObjectGroupPython] C_element105  label="C_element : 059"  # scripted group (container) (typed FeaturePython)
  n = 14
  ref = C_element
FEATURE [App::DocumentObjectGroupPython] H_element096  label="H_element : 053"  # scripted group (container) (typed FeaturePython)
  n = 12
  ref = H_element
FEATURE [App::DocumentObjectGroupPython] G4_STILBENE  # scripted group (container) (typed FeaturePython)
  Dunit = g/cm3
  Dvalue = 0.9707
  Group = -> [C_element105,H_element096]
  conduct = 2
  density = 1
  expand = 3
  formula = G4_STILBENE
  name = G4_STILBENE
  specific = 4
FEATURE [App::DocumentObjectGroupPython] C_element106  label="C_element : 12"  # scripted group (container) (typed FeaturePython)
  n = 12
  ref = C_element
FEATURE [App::DocumentObjectGroupPython] H_element097  label="H_element : 22"  # scripted group (container) (typed FeaturePython)
  n = 22
  ref = H_element
FEATURE [App::DocumentObjectGroupPython] O_element092  label="O_element : 11"  # scripted group (container) (typed FeaturePython)
  n = 11
  ref = O_element
FEATURE [App::DocumentObjectGroupPython] G4_SUCROSE  # scripted group (container) (typed FeaturePython)
  Dunit = g/cm3
  Dvalue = 1.5805
  Group = -> [C_element106,H_element097,O_element092]
  conduct = 2
  density = 1
  expand = 3
  formula = G4_SUCROSE
  name = G4_SUCROSE
  specific = 4
FEATURE [App::DocumentObjectGroupPython] C_element107  label="C_element : 18"  # scripted group (container) (typed FeaturePython)
  n = 18
  ref = C_element
FEATURE [App::DocumentObjectGroupPython] H_element098  label="H_element : 054"  # scripted group (container) (typed FeaturePython)
  n = 14
  ref = H_element
FEATURE [App::DocumentObjectGroupPython] G4_TERPHENYL  # scripted group (container) (typed FeaturePython)
  Dunit = g/cm3
  Dvalue = 1.24
  Group = -> [C_element107,H_element098]
  conduct = 2
  density = 1
  expand = 3
  formula = G4_TERPHENYL
  name = G4_TERPHENYL
  specific = 4
FEATURE [App::DocumentObjectGroupPython] H_element099  label="H_element : 0.146"  # scripted group (container) (typed FeaturePython)
  n = 0.106
FEATURE [App::DocumentObjectGroupPython] C_element108  label="C_element : 0.883"  # scripted group (container) (typed FeaturePython)
  n = 0.099
FEATURE [App::DocumentObjectGroupPython] N_element041  label="N_element : 0.020"  # scripted group (container) (typed FeaturePython)
  n = 0.02
FEATURE [App::DocumentObjectGroupPython] O_element093  label="O_element : 0.766"  # scripted group (container) (typed FeaturePython)
  n = 0.766
FEATURE [App::DocumentObjectGroupPython] Na_element018  label="Na_element : 0.101"  # scripted group (container) (typed FeaturePython)
  n = 0.002
FEATURE [App::DocumentObjectGroupPython] P_element010  label="P_element : 0.108"  # scripted group (container) (typed FeaturePython)
  n = 0.001
FEATURE [App::DocumentObjectGroupPython] S_element021  label="S_element : 0.022"  # scripted group (container) (typed FeaturePython)
  n = 0.002
FEATURE [App::DocumentObjectGroupPython] Cl_element024  label="Cl_element : 0.002"  # scripted group (container) (typed FeaturePython)
  n = 0.002
FEATURE [App::DocumentObjectGroupPython] K_element011  label="K_element : 0.017"  # scripted group (container) (typed FeaturePython)
  n = 0.002
FEATURE [App::DocumentObjectGroupPython] G4_TESTIS_ICRP  # scripted group (container) (typed FeaturePython)
  Dunit = g/cm3
  Dvalue = 1.04
  Group = -> [H_element099,C_element108,N_element041,O_element093,Na_element018,P_element010,S_element021,Cl_element024,K_element011]
  conduct = 2
  density = 1
  expand = 3
  formula = G4_TESTIS_ICRP
  name = G4_TESTIS_ICRP
  specific = 4
FEATURE [App::DocumentObjectGroupPython] C_element109  label="C_element : 060"  # scripted group (container) (typed FeaturePython)
  n = 2
  ref = C_element
FEATURE [App::DocumentObjectGroupPython] Cl_element025  label="Cl_element : 012"  # scripted group (container) (typed FeaturePython)
  n = 4
  ref = Cl_element
FEATURE [App::DocumentObjectGroupPython] G4_TETRACHLOROETHYLENE  # scripted group (container) (typed FeaturePython)
  Dunit = g/cm3
  Dvalue = 1.625
  Group = -> [C_element109,Cl_element025]
  conduct = 2
  density = 1
  expand = 3
  formula = G4_TETRACHLOROETHYLENE
  name = G4_TETRACHLOROETHYLENE
  specific = 4
FEATURE [App::DocumentObjectGroupPython] Tl_element001  label="Tl_element : 1"  # scripted group (container) (typed FeaturePython)
  n = 1
  ref = Tl_element
FEATURE [App::DocumentObjectGroupPython] Cl_element026  label="Cl_element : 013"  # scripted group (container) (typed FeaturePython)
  n = 1
  ref = Cl_element
FEATURE [App::DocumentObjectGroupPython] G4_THALLIUM_CHLORIDE  # scripted group (container) (typed FeaturePython)
  Dunit = g/cm3
  Dvalue = 7.004
  Group = -> [Tl_element001,Cl_element026]
  conduct = 2
  density = 1
  expand = 3
  formula = G4_THALLIUM_CHLORIDE
  name = G4_THALLIUM_CHLORIDE
  specific = 4
FEATURE [App::DocumentObjectGroupPython] H_element100  label="H_element : 0.147"  # scripted group (container) (typed FeaturePython)
  n = 0.105
FEATURE [App::DocumentObjectGroupPython] C_element110  label="C_element : 0.256"  # scripted group (container) (typed FeaturePython)
  n = 0.256
FEATURE [App::DocumentObjectGroupPython] N_element042  label="N_element : 0.760"  # scripted group (container) (typed FeaturePython)
  n = 0.027
FEATURE [App::DocumentObjectGroupPython] O_element094  label="O_element : 0.602"  # scripted group (container) (typed FeaturePython)
  n = 0.602
FEATURE [App::DocumentObjectGroupPython] Na_element019  label="Na_element : 0.102"  # scripted group (container) (typed FeaturePython)
  n = 0.001
FEATURE [App::DocumentObjectGroupPython] P_element011  label="P_element : 0.109"  # scripted group (container) (typed FeaturePython)
  n = 0.002
FEATURE [App::DocumentObjectGroupPython] S_element022  label="S_element : 0.023"  # scripted group (container) (typed FeaturePython)
  n = 0.003
FEATURE [App::DocumentObjectGroupPython] Cl_element027  label="Cl_element : 0.591"  # scripted group (container) (typed FeaturePython)
  n = 0.002
FEATURE [App::DocumentObjectGroupPython] K_element012  label="K_element : 0.018"  # scripted group (container) (typed FeaturePython)
  n = 0.002
FEATURE [App::DocumentObjectGroupPython] G4_TISSUE_SOFT_ICRP  # scripted group (container) (typed FeaturePython)
  Dunit = g/cm3
  Dvalue = 1.03
  Group = -> [H_element100,C_element110,N_element042,O_element094,Na_element019,P_element011,S_element022,Cl_element027,K_element012]
  conduct = 2
  density = 1
  expand = 3
  formula = G4_TISSUE_SOFT_ICRP
  name = G4_TISSUE_SOFT_ICRP
  specific = 4
FEATURE [App::DocumentObjectGroupPython] H_element101  label="H_element : 0.148"  # scripted group (container) (typed FeaturePython)
  n = 0.101
FEATURE [App::DocumentObjectGroupPython] C_element111  label="C_element : 0.111"  # scripted group (container) (typed FeaturePython)
  n = 0.111
FEATURE [App::DocumentObjectGroupPython] N_element043  label="N_element : 0.026"  # scripted group (container) (typed FeaturePython)
  n = 0.026
FEATURE [App::DocumentObjectGroupPython] O_element095  label="O_element : 0.762"  # scripted group (container) (typed FeaturePython)
  n = 0.762
FEATURE [App::DocumentObjectGroupPython] G4_TISSUE_SOFT_ICRU_4  label="G4_TISSUE_SOFT_ICRU-4"  # scripted group (container) (typed FeaturePython)
  Dunit = g/cm3
  Dvalue = 1
  Group = -> [H_element101,C_element111,N_element043,O_element095]
  conduct = 2
  density = 1
  expand = 3
  formula = G4_TISSUE_SOFT_ICRU-4
  name = G4_TISSUE_SOFT_ICRU-4
  specific = 4
FEATURE [App::DocumentObjectGroupPython] H_element102  label="H_element : 0.149"  # scripted group (container) (typed FeaturePython)
  n = 0.101869
FEATURE [App::DocumentObjectGroupPython] C_element112  label="C_element : 0.456"  # scripted group (container) (typed FeaturePython)
  n = 0.456179
FEATURE [App::DocumentObjectGroupPython] N_element044  label="N_element : 0.761"  # scripted group (container) (typed FeaturePython)
  n = 0.035172
FEATURE [App::DocumentObjectGroupPython] O_element096  label="O_element : 0.407"  # scripted group (container) (typed FeaturePython)
  n = 0.40678
FEATURE [App::DocumentObjectGroupPython] G4_TISSUE_METHANE  label="G4_TISSUE-METHANE"  # scripted group (container) (typed FeaturePython)
  Dunit = g/cm3
  Dvalue = 0.00106409
  Group = -> [H_element102,C_element112,N_element044,O_element096]
  conduct = 2
  density = 1
  expand = 3
  formula = G4_TISSUE-METHANE
  name = G4_TISSUE-METHANE
  specific = 4
FEATURE [App::DocumentObjectGroupPython] H_element103  label="H_element : 0.103"  # scripted group (container) (typed FeaturePython)
  n = 0.102672
FEATURE [App::DocumentObjectGroupPython] C_element113  label="C_element : 0.569"  # scripted group (container) (typed FeaturePython)
  n = 0.56894
FEATURE [App::DocumentObjectGroupPython] N_element045  label="N_element : 0.762"  # scripted group (container) (typed FeaturePython)
  n = 0.035022
FEATURE [App::DocumentObjectGroupPython] O_element097  label="O_element : 0.293"  # scripted group (container) (typed FeaturePython)
  n = 0.293366
FEATURE [App::DocumentObjectGroupPython] G4_TISSUE_PROPANE  label="G4_TISSUE-PROPANE"  # scripted group (container) (typed FeaturePython)
  Dunit = g/cm3
  Dvalue = 0.00182628
  Group = -> [H_element103,C_element113,N_element045,O_element097]
  conduct = 2
  density = 1
  expand = 3
  formula = G4_TISSUE-PROPANE
  name = G4_TISSUE-PROPANE
  specific = 4
FEATURE [App::DocumentObjectGroupPython] Ti_element003  label="Ti_element : 1"  # scripted group (container) (typed FeaturePython)
  n = 1
  ref = Ti_element
FEATURE [App::DocumentObjectGroupPython] O_element098  label="O_element : 052"  # scripted group (container) (typed FeaturePython)
  n = 2
  ref = O_element
FEATURE [App::DocumentObjectGroupPython] G4_TITANIUM_DIOXIDE  # scripted group (container) (typed FeaturePython)
  Dunit = g/cm3
  Dvalue = 4.26
  Group = -> [Ti_element003,O_element098]
  conduct = 2
  density = 1
  expand = 3
  formula = G4_TITANIUM_DIOXIDE
  name = G4_TITANIUM_DIOXIDE
  specific = 4
FEATURE [App::DocumentObjectGroupPython] C_element114  label="C_element : 061"  # scripted group (container) (typed FeaturePython)
  n = 7
  ref = C_element
FEATURE [App::DocumentObjectGroupPython] H_element104  label="H_element : 055"  # scripted group (container) (typed FeaturePython)
  n = 8
  ref = H_element
FEATURE [App::DocumentObjectGroupPython] G4_TOLUENE  # scripted group (container) (typed FeaturePython)
  Dunit = g/cm3
  Dvalue = 0.8669
  Group = -> [C_element114,H_element104]
  conduct = 2
  density = 1
  expand = 3
  formula = G4_TOLUENE
  name = G4_TOLUENE
  specific = 4
FEATURE [App::DocumentObjectGroupPython] C_element115  label="C_element : 062"  # scripted group (container) (typed FeaturePython)
  n = 2
  ref = C_element
FEATURE [App::DocumentObjectGroupPython] H_element105  label="H_element : 056"  # scripted group (container) (typed FeaturePython)
  n = 1
  ref = H_element
FEATURE [App::DocumentObjectGroupPython] Cl_element028  label="Cl_element : 014"  # scripted group (container) (typed FeaturePython)
  n = 3
  ref = Cl_element
FEATURE [App::DocumentObjectGroupPython] G4_TRICHLOROETHYLENE  # scripted group (container) (typed FeaturePython)
  Dunit = g/cm3
  Dvalue = 1.46
  Group = -> [C_element115,H_element105,Cl_element028]
  conduct = 2
  density = 1
  expand = 3
  formula = G4_TRICHLOROETHYLENE
  name = G4_TRICHLOROETHYLENE
  specific = 4
FEATURE [App::DocumentObjectGroupPython] C_element116  label="C_element : 063"  # scripted group (container) (typed FeaturePython)
  n = 6
  ref = C_element
FEATURE [App::DocumentObjectGroupPython] H_element106  label="H_element : 15"  # scripted group (container) (typed FeaturePython)
  n = 15
  ref = H_element
FEATURE [App::DocumentObjectGroupPython] O_element099  label="O_element : 053"  # scripted group (container) (typed FeaturePython)
  n = 4
  ref = O_element
FEATURE [App::DocumentObjectGroupPython] P_element012  label="P_element : 1"  # scripted group (container) (typed FeaturePython)
  n = 1
  ref = P_element
FEATURE [App::DocumentObjectGroupPython] G4_TRIETHYL_PHOSPHATE  # scripted group (container) (typed FeaturePython)
  Dunit = g/cm3
  Dvalue = 1.07
  Group = -> [C_element116,H_element106,O_element099,P_element012]
  conduct = 2
  density = 1
  expand = 3
  formula = G4_TRIETHYL_PHOSPHATE
  name = G4_TRIETHYL_PHOSPHATE
  specific = 4
FEATURE [App::DocumentObjectGroupPython] W_element003  label="W_element : 003"  # scripted group (container) (typed FeaturePython)
  n = 1
  ref = W_element
FEATURE [App::DocumentObjectGroupPython] F_element017  label="F_element : 6"  # scripted group (container) (typed FeaturePython)
  n = 6
  ref = F_element
FEATURE [App::DocumentObjectGroupPython] G4_TUNGSTEN_HEXAFLUORIDE  # scripted group (container) (typed FeaturePython)
  Dunit = g/cm3
  Dvalue = 2.4
  Group = -> [W_element003,F_element017]
  conduct = 2
  density = 1
  expand = 3
  formula = G4_TUNGSTEN_HEXAFLUORIDE
  name = G4_TUNGSTEN_HEXAFLUORIDE
  specific = 4
FEATURE [App::DocumentObjectGroupPython] U_element001  label="U_element : 1"  # scripted group (container) (typed FeaturePython)
  n = 1
  ref = U_element
FEATURE [App::DocumentObjectGroupPython] C_element117  label="C_element : 064"  # scripted group (container) (typed FeaturePython)
  n = 2
  ref = C_element
FEATURE [App::DocumentObjectGroupPython] G4_URANIUM_DICARBIDE  # scripted group (container) (typed FeaturePython)
  Dunit = g/cm3
  Dvalue = 11.28
  Group = -> [U_element001,C_element117]
  conduct = 2
  density = 1
  expand = 3
  formula = G4_URANIUM_DICARBIDE
  name = G4_URANIUM_DICARBIDE
  specific = 4
FEATURE [App::DocumentObjectGroupPython] U_element002  label="U_element : 002"  # scripted group (container) (typed FeaturePython)
  n = 1
  ref = U_element
FEATURE [App::DocumentObjectGroupPython] C_element118  label="C_element : 065"  # scripted group (container) (typed FeaturePython)
  n = 1
  ref = C_element
FEATURE [App::DocumentObjectGroupPython] G4_URANIUM_MONOCARBIDE  # scripted group (container) (typed FeaturePython)
  Dunit = g/cm3
  Dvalue = 13.63
  Group = -> [U_element002,C_element118]
  conduct = 2
  density = 1
  expand = 3
  formula = G4_URANIUM_MONOCARBIDE
  name = G4_URANIUM_MONOCARBIDE
  specific = 4
FEATURE [App::DocumentObjectGroupPython] U_element003  label="U_element : 003"  # scripted group (container) (typed FeaturePython)
  n = 1
  ref = U_element
FEATURE [App::DocumentObjectGroupPython] O_element100  label="O_element : 054"  # scripted group (container) (typed FeaturePython)
  n = 2
  ref = O_element
FEATURE [App::DocumentObjectGroupPython] G4_URANIUM_OXIDE  # scripted group (container) (typed FeaturePython)
  Dunit = g/cm3
  Dvalue = 10.96
  Group = -> [U_element003,O_element100]
  conduct = 2
  density = 1
  expand = 3
  formula = G4_URANIUM_OXIDE
  name = G4_URANIUM_OXIDE
  specific = 4
FEATURE [App::DocumentObjectGroupPython] C_element119  label="C_element : 066"  # scripted group (container) (typed FeaturePython)
  n = 1
  ref = C_element
FEATURE [App::DocumentObjectGroupPython] H_element107  label="H_element : 057"  # scripted group (container) (typed FeaturePython)
  n = 4
  ref = H_element
FEATURE [App::DocumentObjectGroupPython] N_element046  label="N_element : 019"  # scripted group (container) (typed FeaturePython)
  n = 2
  ref = N_element
FEATURE [App::DocumentObjectGroupPython] O_element101  label="O_element : 055"  # scripted group (container) (typed FeaturePython)
  n = 1
  ref = O_element
FEATURE [App::DocumentObjectGroupPython] G4_UREA  # scripted group (container) (typed FeaturePython)
  Dunit = g/cm3
  Dvalue = 1.323
  Group = -> [C_element119,H_element107,N_element046,O_element101]
  conduct = 2
  density = 1
  expand = 3
  formula = G4_UREA
  name = G4_UREA
  specific = 4
FEATURE [App::DocumentObjectGroupPython] C_element120  label="C_element : 067"  # scripted group (container) (typed FeaturePython)
  n = 5
  ref = C_element
FEATURE [App::DocumentObjectGroupPython] H_element108  label="H_element : 058"  # scripted group (container) (typed FeaturePython)
  n = 11
  ref = H_element
FEATURE [App::DocumentObjectGroupPython] N_element047  label="N_element : 020"  # scripted group (container) (typed FeaturePython)
  n = 1
  ref = N_element
FEATURE [App::DocumentObjectGroupPython] O_element102  label="O_element : 056"  # scripted group (container) (typed FeaturePython)
  n = 2
  ref = O_element
FEATURE [App::DocumentObjectGroupPython] G4_VALINE  # scripted group (container) (typed FeaturePython)
  Dunit = g/cm3
  Dvalue = 1.23
  Group = -> [C_element120,H_element108,N_element047,O_element102]
  conduct = 2
  density = 1
  expand = 3
  formula = G4_VALINE
  name = G4_VALINE
  specific = 4
FEATURE [App::DocumentObjectGroupPython] H_element109  label="H_element : 0.009"  # scripted group (container) (typed FeaturePython)
  n = 0.009417
FEATURE [App::DocumentObjectGroupPython] C_element121  label="C_element : 0.281"  # scripted group (container) (typed FeaturePython)
  n = 0.280555
FEATURE [App::DocumentObjectGroupPython] F_element018  label="F_element : 0.710"  # scripted group (container) (typed FeaturePython)
  n = 0.710028
FEATURE [App::DocumentObjectGroupPython] G4_VITON  # scripted group (container) (typed FeaturePython)
  Dunit = g/cm3
  Dvalue = 1.8
  Group = -> [H_element109,C_element121,F_element018]
  conduct = 2
  density = 1
  expand = 3
  formula = G4_VITON
  name = G4_VITON
  specific = 4
FEATURE [App::DocumentObjectGroupPython] H_element110  label="H_element : 059"  # scripted group (container) (typed FeaturePython)
  n = 2
  ref = H_element
FEATURE [App::DocumentObjectGroupPython] O_element103  label="O_element : 057"  # scripted group (container) (typed FeaturePython)
  n = 1
  ref = O_element
FEATURE [App::DocumentObjectGroupPython] G4_WATER  # scripted group (container) (typed FeaturePython)
  Dunit = g/cm3
  Dvalue = 1
  Group = -> [H_element110,O_element103]
  conduct = 2
  density = 1
  expand = 3
  formula = G4_WATER
  name = G4_WATER
  specific = 4
FEATURE [App::DocumentObjectGroupPython] H_element111  label="H_element : 060"  # scripted group (container) (typed FeaturePython)
  n = 2
  ref = H_element
FEATURE [App::DocumentObjectGroupPython] O_element104  label="O_element : 058"  # scripted group (container) (typed FeaturePython)
  n = 1
  ref = O_element
FEATURE [App::DocumentObjectGroupPython] G4_WATER_VAPOR  # scripted group (container) (typed FeaturePython)
  Dunit = g/cm3
  Dvalue = 0.000756182
  Group = -> [H_element111,O_element104]
  conduct = 2
  density = 1
  expand = 3
  formula = G4_WATER_VAPOR
  name = G4_WATER_VAPOR
  specific = 4
FEATURE [App::DocumentObjectGroupPython] C_element122  label="C_element : 068"  # scripted group (container) (typed FeaturePython)
  n = 8
  ref = C_element
FEATURE [App::DocumentObjectGroupPython] H_element112  label="H_element : 061"  # scripted group (container) (typed FeaturePython)
  n = 10
  ref = H_element
FEATURE [App::DocumentObjectGroupPython] G4_XYLENE  # scripted group (container) (typed FeaturePython)
  Dunit = g/cm3
  Dvalue = 0.87
  Group = -> [C_element122,H_element112]
  conduct = 2
  density = 1
  expand = 3
  formula = G4_XYLENE
  name = G4_XYLENE
  specific = 4
FEATURE [App::DocumentObjectGroupPython] C_element123  label="C_element : 069"  # scripted group (container) (typed FeaturePython)
  n = 1
  ref = C_element
FEATURE [App::DocumentObjectGroupPython] G4_GRAPHITE  # scripted group (container) (typed FeaturePython)
  Dunit = g/cm3
  Dvalue = 2.21
  Group = -> [C_element123]
  conduct = 2
  density = 1
  expand = 3
  formula = G4_GRAPHITE
  name = G4_GRAPHITE
  specific = 4
FEATURE [App::DocumentObjectGroupPython] NIST  # scripted group (container) (typed FeaturePython)
  Group = -> [G4_A_150_TISSUE,G4_ACETONE,G4_ACETYLENE,G4_ADENINE,G4_ADIPOSE_TISSUE_ICRP,G4_AIR,G4_ALANINE,G4_ALUMINUM_OXIDE,G4_AMBER,G4_AMMONIA,G4_ANILINE,G4_ANTHRACENE,G4_B_100_BONE,G4_BAKELITE,G4_BARIUM_FLUORIDE,G4_BARIUM_SULFATE,G4_BENZENE,G4_BERYLLIUM_OXIDE,G4_BGO,G4_BLOOD_ICRP,G4_BONE_COMPACT_ICRU,G4_BONE_CORTICAL_ICRP,G4_BORON_CARBIDE,G4_BORON_OXIDE,G4_BRAIN_ICRP,G4_BUTANE,G4_N_BUTYL_ALCOHOL,G4_C_552,+152 more]
FEATURE [App::DocumentObjectGroupPython] H_element113  label="H_element : 062"  # scripted group (container) (typed FeaturePython)
  n = 1
  ref = H_element
FEATURE [App::DocumentObjectGroupPython] G4_H  # scripted group (container) (typed FeaturePython)
  Dunit = g/cm3
  Dvalue = 8.3748e-05
  Group = -> [H_element113]
  conduct = 2
  density = 1
  expand = 3
  formula = H
  name = G4_H
  specific = 4
FEATURE [App::DocumentObjectGroupPython] He_element001  label="He_element : 1"  # scripted group (container) (typed FeaturePython)
  n = 1
  ref = He_element
FEATURE [App::DocumentObjectGroupPython] G4_He  # scripted group (container) (typed FeaturePython)
  Dunit = g/cm3
  Dvalue = 0.000166322
  Group = -> [He_element001]
  conduct = 2
  density = 1
  expand = 3
  formula = He
  name = G4_He
  specific = 4
FEATURE [App::DocumentObjectGroupPython] Li_element008  label="Li_element : 008"  # scripted group (container) (typed FeaturePython)
  n = 1
  ref = Li_element
FEATURE [App::DocumentObjectGroupPython] G4_Li  # scripted group (container) (typed FeaturePython)
  Dunit = g/cm3
  Dvalue = 0.534
  Group = -> [Li_element008]
  conduct = 2
  density = 1
  expand = 3
  formula = Li
  name = G4_Li
  specific = 4
FEATURE [App::DocumentObjectGroupPython] Be_element002  label="Be_element : 002"  # scripted group (container) (typed FeaturePython)
  n = 1
  ref = Be_element
FEATURE [App::DocumentObjectGroupPython] G4_Be  # scripted group (container) (typed FeaturePython)
  Dunit = g/cm3
  Dvalue = 1.848
  Group = -> [Be_element002]
  conduct = 2
  density = 1
  expand = 3
  formula = Be
  name = G4_Be
  specific = 4
FEATURE [App::DocumentObjectGroupPython] B_element007  label="B_element : 007"  # scripted group (container) (typed FeaturePython)
  n = 1
  ref = B_element
FEATURE [App::DocumentObjectGroupPython] G4_B  # scripted group (container) (typed FeaturePython)
  Dunit = g/cm3
  Dvalue = 2.37
  Group = -> [B_element007]
  conduct = 2
  density = 1
  expand = 3
  formula = B
  name = G4_B
  specific = 4
FEATURE [App::DocumentObjectGroupPython] C_element124  label="C_element : 070"  # scripted group (container) (typed FeaturePython)
  n = 1
  ref = C_element
FEATURE [App::DocumentObjectGroupPython] G4_C  # scripted group (container) (typed FeaturePython)
  Dunit = g/cm3
  Dvalue = 2
  Group = -> [C_element124]
  conduct = 2
  density = 1
  expand = 3
  formula = C
  name = G4_C
  specific = 4
FEATURE [App::DocumentObjectGroupPython] N_element048  label="N_element : 021"  # scripted group (container) (typed FeaturePython)
  n = 1
  ref = N_element
FEATURE [App::DocumentObjectGroupPython] G4_N  # scripted group (container) (typed FeaturePython)
  Dunit = g/cm3
  Dvalue = 0.0011652
  Group = -> [N_element048]
  conduct = 2
  density = 1
  expand = 3
  formula = N
  name = G4_N
  specific = 4
FEATURE [App::DocumentObjectGroupPython] O_element105  label="O_element : 059"  # scripted group (container) (typed FeaturePython)
  n = 1
  ref = O_element
FEATURE [App::DocumentObjectGroupPython] G4_O  # scripted group (container) (typed FeaturePython)
  Dunit = g/cm3
  Dvalue = 0.00133151
  Group = -> [O_element105]
  conduct = 2
  density = 1
  expand = 3
  formula = O
  name = G4_O
  specific = 4
FEATURE [App::DocumentObjectGroupPython] F_element019  label="F_element : 008"  # scripted group (container) (typed FeaturePython)
  n = 1
  ref = F_element
FEATURE [App::DocumentObjectGroupPython] G4_F  # scripted group (container) (typed FeaturePython)
  Dunit = g/cm3
  Dvalue = 0.00158029
  Group = -> [F_element019]
  conduct = 2
  density = 1
  expand = 3
  formula = F
  name = G4_F
  specific = 4
FEATURE [App::DocumentObjectGroupPython] Ne_element001  label="Ne_element : 1"  # scripted group (container) (typed FeaturePython)
  n = 1
  ref = Ne_element
FEATURE [App::DocumentObjectGroupPython] G4_Ne  # scripted group (container) (typed FeaturePython)
  Dunit = g/cm3
  Dvalue = 0.000838505
  Group = -> [Ne_element001]
  conduct = 2
  density = 1
  expand = 3
  formula = Ne
  name = G4_Ne
  specific = 4
FEATURE [App::DocumentObjectGroupPython] Na_element020  label="Na_element : 005"  # scripted group (container) (typed FeaturePython)
  n = 1
  ref = Na_element
FEATURE [App::DocumentObjectGroupPython] G4_Na  # scripted group (container) (typed FeaturePython)
  Dunit = g/cm3
  Dvalue = 0.971
  Group = -> [Na_element020]
  conduct = 2
  density = 1
  expand = 3
  formula = Na
  name = G4_Na
  specific = 4
FEATURE [App::DocumentObjectGroupPython] Mg_element011  label="Mg_element : 005"  # scripted group (container) (typed FeaturePython)
  n = 1
  ref = Mg_element
FEATURE [App::DocumentObjectGroupPython] G4_Mg  # scripted group (container) (typed FeaturePython)
  Dunit = g/cm3
  Dvalue = 1.74
  Group = -> [Mg_element011]
  conduct = 2
  density = 1
  expand = 3
  formula = Mg
  name = G4_Mg
  specific = 4
FEATURE [App::DocumentObjectGroupPython] Al_element004  label="Al_element : 1"  # scripted group (container) (typed FeaturePython)
  n = 1
  ref = Al_element
FEATURE [App::DocumentObjectGroupPython] G4_Al  # scripted group (container) (typed FeaturePython)
  Dunit = g/cm3
  Dvalue = 2.699
  Group = -> [Al_element004]
  conduct = 2
  density = 1
  expand = 3
  formula = Al
  name = G4_Al
  specific = 4
FEATURE [App::DocumentObjectGroupPython] Si_element007  label="Si_element : 002"  # scripted group (container) (typed FeaturePython)
  n = 1
  ref = Si_element
FEATURE [App::DocumentObjectGroupPython] G4_Si  # scripted group (container) (typed FeaturePython)
  Dunit = g/cm3
  Dvalue = 2.33
  Group = -> [Si_element007]
  conduct = 2
  density = 1
  expand = 3
  formula = Si
  name = G4_Si
  specific = 4
FEATURE [App::DocumentObjectGroupPython] P_element013  label="P_element : 002"  # scripted group (container) (typed FeaturePython)
  n = 1
  ref = P_element
FEATURE [App::DocumentObjectGroupPython] G4_P  # scripted group (container) (typed FeaturePython)
  Dunit = g/cm3
  Dvalue = 2.2
  Group = -> [P_element013]
  conduct = 2
  density = 1
  expand = 3
  formula = P
  name = G4_P
  specific = 4
FEATURE [App::DocumentObjectGroupPython] S_element023  label="S_element : 007"  # scripted group (container) (typed FeaturePython)
  n = 1
  ref = S_element
FEATURE [App::DocumentObjectGroupPython] G4_S  # scripted group (container) (typed FeaturePython)
  Dunit = g/cm3
  Dvalue = 2
  Group = -> [S_element023]
  conduct = 2
  density = 1
  expand = 3
  formula = S
  name = G4_S
  specific = 4
FEATURE [App::DocumentObjectGroupPython] Cl_element029  label="Cl_element : 015"  # scripted group (container) (typed FeaturePython)
  n = 1
  ref = Cl_element
FEATURE [App::DocumentObjectGroupPython] G4_Cl  # scripted group (container) (typed FeaturePython)
  Dunit = g/cm3
  Dvalue = 0.00299473
  Group = -> [Cl_element029]
  conduct = 2
  density = 1
  expand = 3
  formula = Cl
  name = G4_Cl
  specific = 4
FEATURE [App::DocumentObjectGroupPython] Ar_element002  label="Ar_element : 1"  # scripted group (container) (typed FeaturePython)
  n = 1
  ref = Ar_element
FEATURE [App::DocumentObjectGroupPython] G4_Ar  # scripted group (container) (typed FeaturePython)
  Dunit = g/cm3
  Dvalue = 0.00166201
  Group = -> [Ar_element002]
  conduct = 2
  density = 1
  expand = 3
  formula = Ar
  name = G4_Ar
  specific = 4
FEATURE [App::DocumentObjectGroupPython] K_element013  label="K_element : 003"  # scripted group (container) (typed FeaturePython)
  n = 1
  ref = K_element
FEATURE [App::DocumentObjectGroupPython] G4_K  # scripted group (container) (typed FeaturePython)
  Dunit = g/cm3
  Dvalue = 0.862
  Group = -> [K_element013]
  conduct = 2
  density = 1
  expand = 3
  formula = K
  name = G4_K
  specific = 4
FEATURE [App::DocumentObjectGroupPython] Ca_element014  label="Ca_element : 007"  # scripted group (container) (typed FeaturePython)
  n = 1
  ref = Ca_element
FEATURE [App::DocumentObjectGroupPython] G4_Ca  # scripted group (container) (typed FeaturePython)
  Dunit = g/cm3
  Dvalue = 1.55
  Group = -> [Ca_element014]
  conduct = 2
  density = 1
  expand = 3
  formula = Ca
  name = G4_Ca
  specific = 4
FEATURE [App::DocumentObjectGroupPython] Sc_element001  label="Sc_element : 1"  # scripted group (container) (typed FeaturePython)
  n = 1
  ref = Sc_element
FEATURE [App::DocumentObjectGroupPython] G4_Sc  # scripted group (container) (typed FeaturePython)
  Dunit = g/cm3
  Dvalue = 2.989
  Group = -> [Sc_element001]
  conduct = 2
  density = 1
  expand = 3
  formula = Sc
  name = G4_Sc
  specific = 4
FEATURE [App::DocumentObjectGroupPython] Ti_element004  label="Ti_element : 002"  # scripted group (container) (typed FeaturePython)
  n = 1
  ref = Ti_element
FEATURE [App::DocumentObjectGroupPython] G4_Ti  # scripted group (container) (typed FeaturePython)
  Dunit = g/cm3
  Dvalue = 4.54
  Group = -> [Ti_element004]
  conduct = 2
  density = 1
  expand = 3
  formula = Ti
  name = G4_Ti
  specific = 4
FEATURE [App::DocumentObjectGroupPython] V_element001  label="V_element : 1"  # scripted group (container) (typed FeaturePython)
  n = 1
  ref = V_element
FEATURE [App::DocumentObjectGroupPython] G4_V  # scripted group (container) (typed FeaturePython)
  Dunit = g/cm3
  Dvalue = 6.11
  Group = -> [V_element001]
  conduct = 2
  density = 1
  expand = 3
  formula = V
  name = G4_V
  specific = 4
FEATURE [App::DocumentObjectGroupPython] Cr_element001  label="Cr_element : 1"  # scripted group (container) (typed FeaturePython)
  n = 1
  ref = Cr_element
FEATURE [App::DocumentObjectGroupPython] G4_Cr  # scripted group (container) (typed FeaturePython)
  Dunit = g/cm3
  Dvalue = 7.18
  Group = -> [Cr_element001]
  conduct = 2
  density = 1
  expand = 3
  formula = Cr
  name = G4_Cr
  specific = 4
FEATURE [App::DocumentObjectGroupPython] Mn_element001  label="Mn_element : 1"  # scripted group (container) (typed FeaturePython)
  n = 1
  ref = Mn_element
FEATURE [App::DocumentObjectGroupPython] G4_Mn  # scripted group (container) (typed FeaturePython)
  Dunit = g/cm3
  Dvalue = 7.44
  Group = -> [Mn_element001]
  conduct = 2
  density = 1
  expand = 3
  formula = Mn
  name = G4_Mn
  specific = 4
FEATURE [App::DocumentObjectGroupPython] Fe_element007  label="Fe_element : 004"  # scripted group (container) (typed FeaturePython)
  n = 1
  ref = Fe_element
FEATURE [App::DocumentObjectGroupPython] G4_Fe  # scripted group (container) (typed FeaturePython)
  Dunit = g/cm3
  Dvalue = 7.874
  Group = -> [Fe_element007]
  conduct = 2
  density = 1
  expand = 3
  formula = Fe
  name = G4_Fe
  specific = 4
FEATURE [App::DocumentObjectGroupPython] Co_element001  label="Co_element : 1"  # scripted group (container) (typed FeaturePython)
  n = 1
  ref = Co_element
FEATURE [App::DocumentObjectGroupPython] G4_Co  # scripted group (container) (typed FeaturePython)
  Dunit = g/cm3
  Dvalue = 8.9
  Group = -> [Co_element001]
  conduct = 2
  density = 1
  expand = 3
  formula = Co
  name = G4_Co
  specific = 4
FEATURE [App::DocumentObjectGroupPython] Ni_element001  label="Ni_element : 1"  # scripted group (container) (typed FeaturePython)
  n = 1
  ref = Ni_element
FEATURE [App::DocumentObjectGroupPython] G4_Ni  # scripted group (container) (typed FeaturePython)
  Dunit = g/cm3
  Dvalue = 8.902
  Group = -> [Ni_element001]
  conduct = 2
  density = 1
  expand = 3
  formula = Ni
  name = G4_Ni
  specific = 4
FEATURE [App::DocumentObjectGroupPython] Cu_element001  label="Cu_element : 1"  # scripted group (container) (typed FeaturePython)
  n = 1
  ref = Cu_element
FEATURE [App::DocumentObjectGroupPython] G4_Cu  # scripted group (container) (typed FeaturePython)
  Dunit = g/cm3
  Dvalue = 8.96
  Group = -> [Cu_element001]
  conduct = 2
  density = 1
  expand = 3
  formula = Cu
  name = G4_Cu
  specific = 4
FEATURE [App::DocumentObjectGroupPython] Zn_element001  label="Zn_element : 1"  # scripted group (container) (typed FeaturePython)
  n = 1
  ref = Zn_element
FEATURE [App::DocumentObjectGroupPython] G4_Zn  # scripted group (container) (typed FeaturePython)
  Dunit = g/cm3
  Dvalue = 7.133
  Group = -> [Zn_element001]
  conduct = 2
  density = 1
  expand = 3
  formula = Zn
  name = G4_Zn
  specific = 4
FEATURE [App::DocumentObjectGroupPython] Ga_element002  label="Ga_element : 002"  # scripted group (container) (typed FeaturePython)
  n = 1
  ref = Ga_element
FEATURE [App::DocumentObjectGroupPython] G4_Ga  # scripted group (container) (typed FeaturePython)
  Dunit = g/cm3
  Dvalue = 5.904
  Group = -> [Ga_element002]
  conduct = 2
  density = 1
  expand = 3
  formula = Ga
  name = G4_Ga
  specific = 4
FEATURE [App::DocumentObjectGroupPython] Ge_element002  label="Ge_element : 1"  # scripted group (container) (typed FeaturePython)
  n = 1
  ref = Ge_element
FEATURE [App::DocumentObjectGroupPython] G4_Ge  # scripted group (container) (typed FeaturePython)
  Dunit = g/cm3
  Dvalue = 5.323
  Group = -> [Ge_element002]
  conduct = 2
  density = 1
  expand = 3
  formula = Ge
  name = G4_Ge
  specific = 4
FEATURE [App::DocumentObjectGroupPython] As_element003  label="As_element : 002"  # scripted group (container) (typed FeaturePython)
  n = 1
  ref = As_element
FEATURE [App::DocumentObjectGroupPython] G4_As  # scripted group (container) (typed FeaturePython)
  Dunit = g/cm3
  Dvalue = 5.73
  Group = -> [As_element003]
  conduct = 2
  density = 1
  expand = 3
  formula = As
  name = G4_As
  specific = 4
FEATURE [App::DocumentObjectGroupPython] Se_element001  label="Se_element : 1"  # scripted group (container) (typed FeaturePython)
  n = 1
  ref = Se_element
FEATURE [App::DocumentObjectGroupPython] G4_Se  # scripted group (container) (typed FeaturePython)
  Dunit = g/cm3
  Dvalue = 4.5
  Group = -> [Se_element001]
  conduct = 2
  density = 1
  expand = 3
  formula = Se
  name = G4_Se
  specific = 4
FEATURE [App::DocumentObjectGroupPython] Br_element007  label="Br_element : 004"  # scripted group (container) (typed FeaturePython)
  n = 1
  ref = Br_element
FEATURE [App::DocumentObjectGroupPython] G4_Br  # scripted group (container) (typed FeaturePython)
  Dunit = g/cm3
  Dvalue = 0.0070721
  Group = -> [Br_element007]
  conduct = 2
  density = 1
  expand = 3
  formula = Br
  name = G4_Br
  specific = 4
FEATURE [App::DocumentObjectGroupPython] Kr_element001  label="Kr_element : 1"  # scripted group (container) (typed FeaturePython)
  n = 1
  ref = Kr_element
FEATURE [App::DocumentObjectGroupPython] G4_Kr  # scripted group (container) (typed FeaturePython)
  Dunit = g/cm3
  Dvalue = 0.00347832
  Group = -> [Kr_element001]
  conduct = 2
  density = 1
  expand = 3
  formula = Kr
  name = G4_Kr
  specific = 4
FEATURE [App::DocumentObjectGroupPython] Rb_element001  label="Rb_element : 1"  # scripted group (container) (typed FeaturePython)
  n = 1
  ref = Rb_element
FEATURE [App::DocumentObjectGroupPython] G4_Rb  # scripted group (container) (typed FeaturePython)
  Dunit = g/cm3
  Dvalue = 1.532
  Group = -> [Rb_element001]
  conduct = 2
  density = 1
  expand = 3
  formula = Rb
  name = G4_Rb
  specific = 4
FEATURE [App::DocumentObjectGroupPython] Sr_element001  label="Sr_element : 1"  # scripted group (container) (typed FeaturePython)
  n = 1
  ref = Sr_element
FEATURE [App::DocumentObjectGroupPython] G4_Sr  # scripted group (container) (typed FeaturePython)
  Dunit = g/cm3
  Dvalue = 2.54
  Group = -> [Sr_element001]
  conduct = 2
  density = 1
  expand = 3
  formula = Sr
  name = G4_Sr
  specific = 4
FEATURE [App::DocumentObjectGroupPython] Y_element001  label="Y_element : 1"  # scripted group (container) (typed FeaturePython)
  n = 1
  ref = Y_element
FEATURE [App::DocumentObjectGroupPython] G4_Y  # scripted group (container) (typed FeaturePython)
  Dunit = g/cm3
  Dvalue = 4.469
  Group = -> [Y_element001]
  conduct = 2
  density = 1
  expand = 3
  formula = Y
  name = G4_Y
  specific = 4
FEATURE [App::DocumentObjectGroupPython] Zr_element001  label="Zr_element : 1"  # scripted group (container) (typed FeaturePython)
  n = 1
  ref = Zr_element
FEATURE [App::DocumentObjectGroupPython] G4_Zr  # scripted group (container) (typed FeaturePython)
  Dunit = g/cm3
  Dvalue = 6.506
  Group = -> [Zr_element001]
  conduct = 2
  density = 1
  expand = 3
  formula = Zr
  name = G4_Zr
  specific = 4
FEATURE [App::DocumentObjectGroupPython] Nb_element001  label="Nb_element : 1"  # scripted group (container) (typed FeaturePython)
  n = 1
  ref = Nb_element
FEATURE [App::DocumentObjectGroupPython] G4_Nb  # scripted group (container) (typed FeaturePython)
  Dunit = g/cm3
  Dvalue = 8.57
  Group = -> [Nb_element001]
  conduct = 2
  density = 1
  expand = 3
  formula = Nb
  name = G4_Nb
  specific = 4
FEATURE [App::DocumentObjectGroupPython] Mo_element001  label="Mo_element : 1"  # scripted group (container) (typed FeaturePython)
  n = 1
  ref = Mo_element
FEATURE [App::DocumentObjectGroupPython] G4_Mo  # scripted group (container) (typed FeaturePython)
  Dunit = g/cm3
  Dvalue = 10.22
  Group = -> [Mo_element001]
  conduct = 2
  density = 1
  expand = 3
  formula = Mo
  name = G4_Mo
  specific = 4
FEATURE [App::DocumentObjectGroupPython] Tc_element001  label="Tc_element : 1"  # scripted group (container) (typed FeaturePython)
  n = 1
  ref = Tc_element
FEATURE [App::DocumentObjectGroupPython] G4_Tc  # scripted group (container) (typed FeaturePython)
  Dunit = g/cm3
  Dvalue = 11.5
  Group = -> [Tc_element001]
  conduct = 2
  density = 1
  expand = 3
  formula = Tc
  name = G4_Tc
  specific = 4
FEATURE [App::DocumentObjectGroupPython] Ru_element001  label="Ru_element : 1"  # scripted group (container) (typed FeaturePython)
  n = 1
  ref = Ru_element
FEATURE [App::DocumentObjectGroupPython] G4_Ru  # scripted group (container) (typed FeaturePython)
  Dunit = g/cm3
  Dvalue = 12.41
  Group = -> [Ru_element001]
  conduct = 2
  density = 1
  expand = 3
  formula = Ru
  name = G4_Ru
  specific = 4
FEATURE [App::DocumentObjectGroupPython] Rh_element001  label="Rh_element : 1"  # scripted group (container) (typed FeaturePython)
  n = 1
  ref = Rh_element
FEATURE [App::DocumentObjectGroupPython] G4_Rh  # scripted group (container) (typed FeaturePython)
  Dunit = g/cm3
  Dvalue = 12.41
  Group = -> [Rh_element001]
  conduct = 2
  density = 1
  expand = 3
  formula = Rh
  name = G4_Rh
  specific = 4
FEATURE [App::DocumentObjectGroupPython] Pd_element001  label="Pd_element : 1"  # scripted group (container) (typed FeaturePython)
  n = 1
  ref = Pd_element
FEATURE [App::DocumentObjectGroupPython] G4_Pd  # scripted group (container) (typed FeaturePython)
  Dunit = g/cm3
  Dvalue = 12.02
  Group = -> [Pd_element001]
  conduct = 2
  density = 1
  expand = 3
  formula = Pd
  name = G4_Pd
  specific = 4
FEATURE [App::DocumentObjectGroupPython] Ag_element006  label="Ag_element : 004"  # scripted group (container) (typed FeaturePython)
  n = 1
  ref = Ag_element
FEATURE [App::DocumentObjectGroupPython] G4_Ag  # scripted group (container) (typed FeaturePython)
  Dunit = g/cm3
  Dvalue = 10.5
  Group = -> [Ag_element006]
  conduct = 2
  density = 1
  expand = 3
  formula = Ag
  name = G4_Ag
  specific = 4
FEATURE [App::DocumentObjectGroupPython] Cd_element003  label="Cd_element : 003"  # scripted group (container) (typed FeaturePython)
  n = 1
  ref = Cd_element
FEATURE [App::DocumentObjectGroupPython] G4_Cd  # scripted group (container) (typed FeaturePython)
  Dunit = g/cm3
  Dvalue = 8.65
  Group = -> [Cd_element003]
  conduct = 2
  density = 1
  expand = 3
  formula = Cd
  name = G4_Cd
  specific = 4
FEATURE [App::DocumentObjectGroupPython] In_element001  label="In_element : 1"  # scripted group (container) (typed FeaturePython)
  n = 1
  ref = In_element
FEATURE [App::DocumentObjectGroupPython] G4_In  # scripted group (container) (typed FeaturePython)
  Dunit = g/cm3
  Dvalue = 7.31
  Group = -> [In_element001]
  conduct = 2
  density = 1
  expand = 3
  formula = In
  name = G4_In
  specific = 4
FEATURE [App::DocumentObjectGroupPython] Sn_element001  label="Sn_element : 1"  # scripted group (container) (typed FeaturePython)
  n = 1
  ref = Sn_element
FEATURE [App::DocumentObjectGroupPython] G4_Sn  # scripted group (container) (typed FeaturePython)
  Dunit = g/cm3
  Dvalue = 7.31
  Group = -> [Sn_element001]
  conduct = 2
  density = 1
  expand = 3
  formula = Sn
  name = G4_Sn
  specific = 4
FEATURE [App::DocumentObjectGroupPython] Sb_element001  label="Sb_element : 1"  # scripted group (container) (typed FeaturePython)
  n = 1
  ref = Sb_element
FEATURE [App::DocumentObjectGroupPython] G4_Sb  # scripted group (container) (typed FeaturePython)
  Dunit = g/cm3
  Dvalue = 6.691
  Group = -> [Sb_element001]
  conduct = 2
  density = 1
  expand = 3
  formula = Sb
  name = G4_Sb
  specific = 4
FEATURE [App::DocumentObjectGroupPython] Te_element002  label="Te_element : 002"  # scripted group (container) (typed FeaturePython)
  n = 1
  ref = Te_element
FEATURE [App::DocumentObjectGroupPython] G4_Te  # scripted group (container) (typed FeaturePython)
  Dunit = g/cm3
  Dvalue = 6.24
  Group = -> [Te_element002]
  conduct = 2
  density = 1
  expand = 3
  formula = Te
  name = G4_Te
  specific = 4
FEATURE [App::DocumentObjectGroupPython] I_element010  label="I_element : 006"  # scripted group (container) (typed FeaturePython)
  n = 1
  ref = I_element
FEATURE [App::DocumentObjectGroupPython] G4_I  # scripted group (container) (typed FeaturePython)
  Dunit = g/cm3
  Dvalue = 4.93
  Group = -> [I_element010]
  conduct = 2
  density = 1
  expand = 3
  formula = I
  name = G4_I
  specific = 4
FEATURE [App::DocumentObjectGroupPython] Xe_element001  label="Xe_element : 1"  # scripted group (container) (typed FeaturePython)
  n = 1
  ref = Xe_element
FEATURE [App::DocumentObjectGroupPython] G4_Xe  # scripted group (container) (typed FeaturePython)
  Dunit = g/cm3
  Dvalue = 0.00548536
  Group = -> [Xe_element001]
  conduct = 2
  density = 1
  expand = 3
  formula = Xe
  name = G4_Xe
  specific = 4
FEATURE [App::DocumentObjectGroupPython] Cs_element003  label="Cs_element : 003"  # scripted group (container) (typed FeaturePython)
  n = 1
  ref = Cs_element
FEATURE [App::DocumentObjectGroupPython] G4_Cs  # scripted group (container) (typed FeaturePython)
  Dunit = g/cm3
  Dvalue = 1.873
  Group = -> [Cs_element003]
  conduct = 2
  density = 1
  expand = 3
  formula = Cs
  name = G4_Cs
  specific = 4
FEATURE [App::DocumentObjectGroupPython] Ba_element003  label="Ba_element : 003"  # scripted group (container) (typed FeaturePython)
  n = 1
  ref = Ba_element
FEATURE [App::DocumentObjectGroupPython] G4_Ba  # scripted group (container) (typed FeaturePython)
  Dunit = g/cm3
  Dvalue = 3.5
  Group = -> [Ba_element003]
  conduct = 2
  density = 1
  expand = 3
  formula = Ba
  name = G4_Ba
  specific = 4
FEATURE [App::DocumentObjectGroupPython] La_element003  label="La_element : 003"  # scripted group (container) (typed FeaturePython)
  n = 1
  ref = La_element
FEATURE [App::DocumentObjectGroupPython] G4_La  # scripted group (container) (typed FeaturePython)
  Dunit = g/cm3
  Dvalue = 6.154
  Group = -> [La_element003]
  conduct = 2
  density = 1
  expand = 3
  formula = La
  name = G4_La
  specific = 4
FEATURE [App::DocumentObjectGroupPython] Ce_element002  label="Ce_element : 1"  # scripted group (container) (typed FeaturePython)
  n = 1
  ref = Ce_element
FEATURE [App::DocumentObjectGroupPython] G4_Ce  # scripted group (container) (typed FeaturePython)
  Dunit = g/cm3
  Dvalue = 6.657
  Group = -> [Ce_element002]
  conduct = 2
  density = 1
  expand = 3
  formula = Ce
  name = G4_Ce
  specific = 4
FEATURE [App::DocumentObjectGroupPython] Pr_element001  label="Pr_element : 1"  # scripted group (container) (typed FeaturePython)
  n = 1
  ref = Pr_element
FEATURE [App::DocumentObjectGroupPython] G4_Pr  # scripted group (container) (typed FeaturePython)
  Dunit = g/cm3
  Dvalue = 6.71
  Group = -> [Pr_element001]
  conduct = 2
  density = 1
  expand = 3
  formula = Pr
  name = G4_Pr
  specific = 4
FEATURE [App::DocumentObjectGroupPython] Nd_element001  label="Nd_element : 1"  # scripted group (container) (typed FeaturePython)
  n = 1
  ref = Nd_element
FEATURE [App::DocumentObjectGroupPython] G4_Nd  # scripted group (container) (typed FeaturePython)
  Dunit = g/cm3
  Dvalue = 6.9
  Group = -> [Nd_element001]
  conduct = 2
  density = 1
  expand = 3
  formula = Nd
  name = G4_Nd
  specific = 4
FEATURE [App::DocumentObjectGroupPython] Pm_element001  label="Pm_element : 1"  # scripted group (container) (typed FeaturePython)
  n = 1
  ref = Pm_element
FEATURE [App::DocumentObjectGroupPython] G4_Pm  # scripted group (container) (typed FeaturePython)
  Dunit = g/cm3
  Dvalue = 7.22
  Group = -> [Pm_element001]
  conduct = 2
  density = 1
  expand = 3
  formula = Pm
  name = G4_Pm
  specific = 4
FEATURE [App::DocumentObjectGroupPython] Sm_element001  label="Sm_element : 1"  # scripted group (container) (typed FeaturePython)
  n = 1
  ref = Sm_element
FEATURE [App::DocumentObjectGroupPython] G4_Sm  # scripted group (container) (typed FeaturePython)
  Dunit = g/cm3
  Dvalue = 7.46
  Group = -> [Sm_element001]
  conduct = 2
  density = 1
  expand = 3
  formula = Sm
  name = G4_Sm
  specific = 4
FEATURE [App::DocumentObjectGroupPython] Eu_element001  label="Eu_element : 1"  # scripted group (container) (typed FeaturePython)
  n = 1
  ref = Eu_element
FEATURE [App::DocumentObjectGroupPython] G4_Eu  # scripted group (container) (typed FeaturePython)
  Dunit = g/cm3
  Dvalue = 5.243
  Group = -> [Eu_element001]
  conduct = 2
  density = 1
  expand = 3
  formula = Eu
  name = G4_Eu
  specific = 4
FEATURE [App::DocumentObjectGroupPython] Gd_element002  label="Gd_element : 1"  # scripted group (container) (typed FeaturePython)
  n = 1
  ref = Gd_element
FEATURE [App::DocumentObjectGroupPython] G4_Gd  # scripted group (container) (typed FeaturePython)
  Dunit = g/cm3
  Dvalue = 7.9004
  Group = -> [Gd_element002]
  conduct = 2
  density = 1
  expand = 3
  formula = Gd
  name = G4_Gd
  specific = 4
FEATURE [App::DocumentObjectGroupPython] Tb_element001  label="Tb_element : 1"  # scripted group (container) (typed FeaturePython)
  n = 1
  ref = Tb_element
FEATURE [App::DocumentObjectGroupPython] G4_Tb  # scripted group (container) (typed FeaturePython)
  Dunit = g/cm3
  Dvalue = 8.229
  Group = -> [Tb_element001]
  conduct = 2
  density = 1
  expand = 3
  formula = Tb
  name = G4_Tb
  specific = 4
FEATURE [App::DocumentObjectGroupPython] Dy_element001  label="Dy_element : 1"  # scripted group (container) (typed FeaturePython)
  n = 1
  ref = Dy_element
FEATURE [App::DocumentObjectGroupPython] G4_Dy  # scripted group (container) (typed FeaturePython)
  Dunit = g/cm3
  Dvalue = 8.55
  Group = -> [Dy_element001]
  conduct = 2
  density = 1
  expand = 3
  formula = Dy
  name = G4_Dy
  specific = 4
FEATURE [App::DocumentObjectGroupPython] Ho_element001  label="Ho_element : 1"  # scripted group (container) (typed FeaturePython)
  n = 1
  ref = Ho_element
FEATURE [App::DocumentObjectGroupPython] G4_Ho  # scripted group (container) (typed FeaturePython)
  Dunit = g/cm3
  Dvalue = 8.795
  Group = -> [Ho_element001]
  conduct = 2
  density = 1
  expand = 3
  formula = Ho
  name = G4_Ho
  specific = 4
FEATURE [App::DocumentObjectGroupPython] Er_element001  label="Er_element : 1"  # scripted group (container) (typed FeaturePython)
  n = 1
  ref = Er_element
FEATURE [App::DocumentObjectGroupPython] G4_Er  # scripted group (container) (typed FeaturePython)
  Dunit = g/cm3
  Dvalue = 9.066
  Group = -> [Er_element001]
  conduct = 2
  density = 1
  expand = 3
  formula = Er
  name = G4_Er
  specific = 4
FEATURE [App::DocumentObjectGroupPython] Tm_element001  label="Tm_element : 1"  # scripted group (container) (typed FeaturePython)
  n = 1
  ref = Tm_element
FEATURE [App::DocumentObjectGroupPython] G4_Tm  # scripted group (container) (typed FeaturePython)
  Dunit = g/cm3
  Dvalue = 9.321
  Group = -> [Tm_element001]
  conduct = 2
  density = 1
  expand = 3
  formula = Tm
  name = G4_Tm
  specific = 4
FEATURE [App::DocumentObjectGroupPython] Yb_element001  label="Yb_element : 1"  # scripted group (container) (typed FeaturePython)
  n = 1
  ref = Yb_element
FEATURE [App::DocumentObjectGroupPython] G4_Yb  # scripted group (container) (typed FeaturePython)
  Dunit = g/cm3
  Dvalue = 6.73
  Group = -> [Yb_element001]
  conduct = 2
  density = 1
  expand = 3
  formula = Yb
  name = G4_Yb
  specific = 4
FEATURE [App::DocumentObjectGroupPython] Lu_element001  label="Lu_element : 1"  # scripted group (container) (typed FeaturePython)
  n = 1
  ref = Lu_element
FEATURE [App::DocumentObjectGroupPython] G4_Lu  # scripted group (container) (typed FeaturePython)
  Dunit = g/cm3
  Dvalue = 9.84
  Group = -> [Lu_element001]
  conduct = 2
  density = 1
  expand = 3
  formula = Lu
  name = G4_Lu
  specific = 4
FEATURE [App::DocumentObjectGroupPython] Hf_element001  label="Hf_element : 1"  # scripted group (container) (typed FeaturePython)
  n = 1
  ref = Hf_element
FEATURE [App::DocumentObjectGroupPython] G4_Hf  # scripted group (container) (typed FeaturePython)
  Dunit = g/cm3
  Dvalue = 13.31
  Group = -> [Hf_element001]
  conduct = 2
  density = 1
  expand = 3
  formula = Hf
  name = G4_Hf
  specific = 4
FEATURE [App::DocumentObjectGroupPython] Ta_element001  label="Ta_element : 1"  # scripted group (container) (typed FeaturePython)
  n = 1
  ref = Ta_element
FEATURE [App::DocumentObjectGroupPython] G4_Ta  # scripted group (container) (typed FeaturePython)
  Dunit = g/cm3
  Dvalue = 16.654
  Group = -> [Ta_element001]
  conduct = 2
  density = 1
  expand = 3
  formula = Ta
  name = G4_Ta
  specific = 4
FEATURE [App::DocumentObjectGroupPython] W_element004  label="W_element : 004"  # scripted group (container) (typed FeaturePython)
  n = 1
  ref = W_element
FEATURE [App::DocumentObjectGroupPython] G4_W  # scripted group (container) (typed FeaturePython)
  Dunit = g/cm3
  Dvalue = 19.3
  Group = -> [W_element004]
  conduct = 2
  density = 1
  expand = 3
  formula = W
  name = G4_W
  specific = 4
FEATURE [App::DocumentObjectGroupPython] Re_element001  label="Re_element : 1"  # scripted group (container) (typed FeaturePython)
  n = 1
  ref = Re_element
FEATURE [App::DocumentObjectGroupPython] G4_Re  # scripted group (container) (typed FeaturePython)
  Dunit = g/cm3
  Dvalue = 21.02
  Group = -> [Re_element001]
  conduct = 2
  density = 1
  expand = 3
  formula = Re
  name = G4_Re
  specific = 4
FEATURE [App::DocumentObjectGroupPython] Os_element001  label="Os_element : 1"  # scripted group (container) (typed FeaturePython)
  n = 1
  ref = Os_element
FEATURE [App::DocumentObjectGroupPython] G4_Os  # scripted group (container) (typed FeaturePython)
  Dunit = g/cm3
  Dvalue = 22.57
  Group = -> [Os_element001]
  conduct = 2
  density = 1
  expand = 3
  formula = Os
  name = G4_Os
  specific = 4
FEATURE [App::DocumentObjectGroupPython] Ir_element001  label="Ir_element : 1"  # scripted group (container) (typed FeaturePython)
  n = 1
  ref = Ir_element
FEATURE [App::DocumentObjectGroupPython] G4_Ir  # scripted group (container) (typed FeaturePython)
  Dunit = g/cm3
  Dvalue = 22.42
  Group = -> [Ir_element001]
  conduct = 2
  density = 1
  expand = 3
  formula = Ir
  name = G4_Ir
  specific = 4
FEATURE [App::DocumentObjectGroupPython] Pt_element001  label="Pt_element : 1"  # scripted group (container) (typed FeaturePython)
  n = 1
  ref = Pt_element
FEATURE [App::DocumentObjectGroupPython] G4_Pt  # scripted group (container) (typed FeaturePython)
  Dunit = g/cm3
  Dvalue = 21.45
  Group = -> [Pt_element001]
  conduct = 2
  density = 1
  expand = 3
  formula = Pt
  name = G4_Pt
  specific = 4
FEATURE [App::DocumentObjectGroupPython] Au_element001  label="Au_element : 1"  # scripted group (container) (typed FeaturePython)
  n = 1
  ref = Au_element
FEATURE [App::DocumentObjectGroupPython] G4_Au  # scripted group (container) (typed FeaturePython)
  Dunit = g/cm3
  Dvalue = 19.32
  Group = -> [Au_element001]
  conduct = 2
  density = 1
  expand = 3
  formula = Au
  name = G4_Au
  specific = 4
FEATURE [App::DocumentObjectGroupPython] Hg_element002  label="Hg_element : 002"  # scripted group (container) (typed FeaturePython)
  n = 1
  ref = Hg_element
FEATURE [App::DocumentObjectGroupPython] G4_Hg  # scripted group (container) (typed FeaturePython)
  Dunit = g/cm3
  Dvalue = 13.546
  Group = -> [Hg_element002]
  conduct = 2
  density = 1
  expand = 3
  formula = Hg
  name = G4_Hg
  specific = 4
FEATURE [App::DocumentObjectGroupPython] Tl_element002  label="Tl_element : 002"  # scripted group (container) (typed FeaturePython)
  n = 1
  ref = Tl_element
FEATURE [App::DocumentObjectGroupPython] G4_Tl  # scripted group (container) (typed FeaturePython)
  Dunit = g/cm3
  Dvalue = 11.72
  Group = -> [Tl_element002]
  conduct = 2
  density = 1
  expand = 3
  formula = Tl
  name = G4_Tl
  specific = 4
FEATURE [App::DocumentObjectGroupPython] Pb_element003  label="Pb_element : 1"  # scripted group (container) (typed FeaturePython)
  n = 1
  ref = Pb_element
FEATURE [App::DocumentObjectGroupPython] G4_Pb  # scripted group (container) (typed FeaturePython)
  Dunit = g/cm3
  Dvalue = 11.35
  Group = -> [Pb_element003]
  conduct = 2
  density = 1
  expand = 3
  formula = Pb
  name = G4_Pb
  specific = 4
FEATURE [App::DocumentObjectGroupPython] Bi_element002  label="Bi_element : 1"  # scripted group (container) (typed FeaturePython)
  n = 1
  ref = Bi_element
FEATURE [App::DocumentObjectGroupPython] G4_Bi  # scripted group (container) (typed FeaturePython)
  Dunit = g/cm3
  Dvalue = 9.747
  Group = -> [Bi_element002]
  conduct = 2
  density = 1
  expand = 3
  formula = Bi
  name = G4_Bi
  specific = 4
FEATURE [App::DocumentObjectGroupPython] Po_element001  label="Po_element : 1"  # scripted group (container) (typed FeaturePython)
  n = 1
  ref = Po_element
FEATURE [App::DocumentObjectGroupPython] G4_Po  # scripted group (container) (typed FeaturePython)
  Dunit = g/cm3
  Dvalue = 9.32
  Group = -> [Po_element001]
  conduct = 2
  density = 1
  expand = 3
  formula = Po
  name = G4_Po
  specific = 4
FEATURE [App::DocumentObjectGroupPython] At_element001  label="At_element : 1"  # scripted group (container) (typed FeaturePython)
  n = 1
  ref = At_element
FEATURE [App::DocumentObjectGroupPython] G4_At  # scripted group (container) (typed FeaturePython)
  Dunit = g/cm3
  Dvalue = 9.32
  Group = -> [At_element001]
  conduct = 2
  density = 1
  expand = 3
  formula = At
  name = G4_At
  specific = 4
FEATURE [App::DocumentObjectGroupPython] Rn_element001  label="Rn_element : 1"  # scripted group (container) (typed FeaturePython)
  n = 1
  ref = Rn_element
FEATURE [App::DocumentObjectGroupPython] G4_Rn  # scripted group (container) (typed FeaturePython)
  Dunit = g/cm3
  Dvalue = 0.00900662
  Group = -> [Rn_element001]
  conduct = 2
  density = 1
  expand = 3
  formula = Rn
  name = G4_Rn
  specific = 4
FEATURE [App::DocumentObjectGroupPython] Fr_element001  label="Fr_element : 1"  # scripted group (container) (typed FeaturePython)
  n = 1
  ref = Fr_element
FEATURE [App::DocumentObjectGroupPython] G4_Fr  # scripted group (container) (typed FeaturePython)
  Dunit = g/cm3
  Dvalue = 1
  Group = -> [Fr_element001]
  conduct = 2
  density = 1
  expand = 3
  formula = Fr
  name = G4_Fr
  specific = 4
FEATURE [App::DocumentObjectGroupPython] Ra_element001  label="Ra_element : 1"  # scripted group (container) (typed FeaturePython)
  n = 1
  ref = Ra_element
FEATURE [App::DocumentObjectGroupPython] G4_Ra  # scripted group (container) (typed FeaturePython)
  Dunit = g/cm3
  Dvalue = 5
  Group = -> [Ra_element001]
  conduct = 2
  density = 1
  expand = 3
  formula = Ra
  name = G4_Ra
  specific = 4
FEATURE [App::DocumentObjectGroupPython] Ac_element001  label="Ac_element : 1"  # scripted group (container) (typed FeaturePython)
  n = 1
  ref = Ac_element
FEATURE [App::DocumentObjectGroupPython] G4_Ac  # scripted group (container) (typed FeaturePython)
  Dunit = g/cm3
  Dvalue = 10.07
  Group = -> [Ac_element001]
  conduct = 2
  density = 1
  expand = 3
  formula = Ac
  name = G4_Ac
  specific = 4
FEATURE [App::DocumentObjectGroupPython] Th_element001  label="Th_element : 1"  # scripted group (container) (typed FeaturePython)
  n = 1
  ref = Th_element
FEATURE [App::DocumentObjectGroupPython] G4_Th  # scripted group (container) (typed FeaturePython)
  Dunit = g/cm3
  Dvalue = 11.72
  Group = -> [Th_element001]
  conduct = 2
  density = 1
  expand = 3
  formula = Th
  name = G4_Th
  specific = 4
FEATURE [App::DocumentObjectGroupPython] Pa_element001  label="Pa_element : 1"  # scripted group (container) (typed FeaturePython)
  n = 1
  ref = Pa_element
FEATURE [App::DocumentObjectGroupPython] G4_Pa  # scripted group (container) (typed FeaturePython)
  Dunit = g/cm3
  Dvalue = 15.37
  Group = -> [Pa_element001]
  conduct = 2
  density = 1
  expand = 3
  formula = Pa
  name = G4_Pa
  specific = 4
FEATURE [App::DocumentObjectGroupPython] U_element004  label="U_element : 004"  # scripted group (container) (typed FeaturePython)
  n = 1
  ref = U_element
FEATURE [App::DocumentObjectGroupPython] G4_U  # scripted group (container) (typed FeaturePython)
  Dunit = g/cm3
  Dvalue = 18.95
  Group = -> [U_element004]
  conduct = 2
  density = 1
  expand = 3
  formula = U
  name = G4_U
  specific = 4
FEATURE [App::DocumentObjectGroupPython] Np_element001  label="Np_element : 1"  # scripted group (container) (typed FeaturePython)
  n = 1
  ref = Np_element
FEATURE [App::DocumentObjectGroupPython] G4_Np  # scripted group (container) (typed FeaturePython)
  Dunit = g/cm3
  Dvalue = 20.25
  Group = -> [Np_element001]
  conduct = 2
  density = 1
  expand = 3
  formula = Np
  name = G4_Np
  specific = 4
FEATURE [App::DocumentObjectGroupPython] Pu_element002  label="Pu_element : 002"  # scripted group (container) (typed FeaturePython)
  n = 1
  ref = Pu_element
FEATURE [App::DocumentObjectGroupPython] G4_Pu  # scripted group (container) (typed FeaturePython)
  Dunit = g/cm3
  Dvalue = 19.84
  Group = -> [Pu_element002]
  conduct = 2
  density = 1
  expand = 3
  formula = Pu
  name = G4_Pu
  specific = 4
FEATURE [App::DocumentObjectGroupPython] Am_element001  label="Am_element : 1"  # scripted group (container) (typed FeaturePython)
  n = 1
  ref = Am_element
FEATURE [App::DocumentObjectGroupPython] G4_Am  # scripted group (container) (typed FeaturePython)
  Dunit = g/cm3
  Dvalue = 13.67
  Group = -> [Am_element001]
  conduct = 2
  density = 1
  expand = 3
  formula = Am
  name = G4_Am
  specific = 4
FEATURE [App::DocumentObjectGroupPython] Cm_element001  label="Cm_element : 1"  # scripted group (container) (typed FeaturePython)
  n = 1
  ref = Cm_element
FEATURE [App::DocumentObjectGroupPython] G4_Cm  # scripted group (container) (typed FeaturePython)
  Dunit = g/cm3
  Dvalue = 13.51
  Group = -> [Cm_element001]
  conduct = 2
  density = 1
  expand = 3
  formula = Cm
  name = G4_Cm
  specific = 4
FEATURE [App::DocumentObjectGroupPython] Bk_element001  label="Bk_element : 1"  # scripted group (container) (typed FeaturePython)
  n = 1
  ref = Bk_element
FEATURE [App::DocumentObjectGroupPython] G4_Bk  # scripted group (container) (typed FeaturePython)
  Dunit = g/cm3
  Dvalue = 14
  Group = -> [Bk_element001]
  conduct = 2
  density = 1
  expand = 3
  formula = Bk
  name = G4_Bk
  specific = 4
FEATURE [App::DocumentObjectGroupPython] Cf_element001  label="Cf_element : 1"  # scripted group (container) (typed FeaturePython)
  n = 1
  ref = Cf_element
FEATURE [App::DocumentObjectGroupPython] G4_Cf  # scripted group (container) (typed FeaturePython)
  Dunit = g/cm3
  Dvalue = 10
  Group = -> [Cf_element001]
  conduct = 2
  density = 1
  expand = 3
  formula = Cf
  name = G4_Cf
  specific = 4
FEATURE [App::DocumentObjectGroupPython] Element  # scripted group (container) (typed FeaturePython)
  Group = -> [G4_H,G4_He,G4_Li,G4_Be,G4_B,G4_C,G4_N,G4_O,G4_F,G4_Ne,G4_Na,G4_Mg,G4_Al,G4_Si,G4_P,G4_S,G4_Cl,G4_Ar,G4_K,G4_Ca,G4_Sc,G4_Ti,G4_V,G4_Cr,G4_Mn,G4_Fe,G4_Co,G4_Ni,G4_Cu,G4_Zn,G4_Ga,G4_Ge,G4_As,G4_Se,G4_Br,G4_Kr,G4_Rb,G4_Sr,G4_Y,G4_Zr,G4_Nb,G4_Mo,G4_Tc,G4_Ru,G4_Rh,G4_Pd,G4_Ag,G4_Cd,G4_In,G4_Sn,G4_Sb,G4_Te,G4_I,G4_Xe,G4_Cs,G4_Ba,G4_La,G4_Ce,G4_Pr,G4_Nd,G4_Pm,G4_Sm,G4_Eu,G4_Gd,G4_Tb,G4_Dy,G4_Ho,G4_Er,+30 more]
FEATURE [App::DocumentObjectGroupPython] H_element114  label="H_element : 063"  # scripted group (container) (typed FeaturePython)
  n = 2
  ref = H_element
FEATURE [App::DocumentObjectGroupPython] G4_lH2  # scripted group (container) (typed FeaturePython)
  Dunit = g/cm3
  Dvalue = 0.0708
  Group = -> [H_element114]
  conduct = 2
  density = 1
  expand = 3
  formula = G4_lH2
  name = G4_lH2
  specific = 4
FEATURE [App::DocumentObjectGroupPython] N_element049  label="N_element : 022"  # scripted group (container) (typed FeaturePython)
  n = 2
  ref = N_element
FEATURE [App::DocumentObjectGroupPython] G4_lN2  # scripted group (container) (typed FeaturePython)
  Dunit = g/cm3
  Dvalue = 0.807
  Group = -> [N_element049]
  conduct = 2
  density = 1
  expand = 3
  formula = G4_lN2
  name = G4_lN2
  specific = 4
FEATURE [App::DocumentObjectGroupPython] O_element106  label="O_element : 060"  # scripted group (container) (typed FeaturePython)
  n = 2
  ref = O_element
FEATURE [App::DocumentObjectGroupPython] G4_lO2  # scripted group (container) (typed FeaturePython)
  Dunit = g/cm3
  Dvalue = 1.141
  Group = -> [O_element106]
  conduct = 2
  density = 1
  expand = 3
  formula = G4_lO2
  name = G4_lO2
  specific = 4
FEATURE [App::DocumentObjectGroupPython] Ar_element003  label="Ar_element : 002"  # scripted group (container) (typed FeaturePython)
  n = 1
  ref = Ar_element
FEATURE [App::DocumentObjectGroupPython] G4_lAr  # scripted group (container) (typed FeaturePython)
  Dunit = g/cm3
  Dvalue = 1.396
  Group = -> [Ar_element003]
  conduct = 2
  density = 1
  expand = 3
  formula = G4_lAr
  name = G4_lAr
  specific = 4
FEATURE [App::DocumentObjectGroupPython] Br_element008  label="Br_element : 005"  # scripted group (container) (typed FeaturePython)
  n = 1
  ref = Br_element
FEATURE [App::DocumentObjectGroupPython] G4_lBr  # scripted group (container) (typed FeaturePython)
  Dunit = g/cm3
  Dvalue = 3.1028
  Group = -> [Br_element008]
  conduct = 2
  density = 1
  expand = 3
  formula = G4_lBr
  name = G4_lBr
  specific = 4
FEATURE [App::DocumentObjectGroupPython] Kr_element002  label="Kr_element : 002"  # scripted group (container) (typed FeaturePython)
  n = 1
  ref = Kr_element
FEATURE [App::DocumentObjectGroupPython] G4_lKr  # scripted group (container) (typed FeaturePython)
  Dunit = g/cm3
  Dvalue = 2.418
  Group = -> [Kr_element002]
  conduct = 2
  density = 1
  expand = 3
  formula = G4_lKr
  name = G4_lKr
  specific = 4
FEATURE [App::DocumentObjectGroupPython] Xe_element002  label="Xe_element : 002"  # scripted group (container) (typed FeaturePython)
  n = 1
  ref = Xe_element
FEATURE [App::DocumentObjectGroupPython] G4_lXe  # scripted group (container) (typed FeaturePython)
  Dunit = g/cm3
  Dvalue = 2.953
  Group = -> [Xe_element002]
  conduct = 2
  density = 1
  expand = 3
  formula = G4_lXe
  name = G4_lXe
  specific = 4
FEATURE [App::DocumentObjectGroupPython] O_element107  label="O_element : 061"  # scripted group (container) (typed FeaturePython)
  n = 4
  ref = O_element
FEATURE [App::DocumentObjectGroupPython] Pb_element004  label="Pb_element : 002"  # scripted group (container) (typed FeaturePython)
  n = 1
  ref = Pb_element
FEATURE [App::DocumentObjectGroupPython] W_element005  label="W_element : 005"  # scripted group (container) (typed FeaturePython)
  n = 1
  ref = W_element
FEATURE [App::DocumentObjectGroupPython] G4_PbWO4  # scripted group (container) (typed FeaturePython)
  Dunit = g/cm3
  Dvalue = 8.28
  Group = -> [O_element107,Pb_element004,W_element005]
  conduct = 2
  density = 1
  expand = 3
  formula = G4_PbWO4
  name = G4_PbWO4
  specific = 4
FEATURE [App::DocumentObjectGroupPython] H_element115  label="H_element : 064"  # scripted group (container) (typed FeaturePython)
  n = 1
  ref = H_element
FEATURE [App::DocumentObjectGroupPython] G4_Galactic  # scripted group (container) (typed FeaturePython)
  Dunit = g/cm3
  Dvalue = 0
  Group = -> [H_element115]
  conduct = 2
  density = 1
  expand = 3
  formula = G4_Galactic
  name = G4_Galactic
  specific = 4
FEATURE [App::DocumentObjectGroupPython] C_element125  label="C_element : 071"  # scripted group (container) (typed FeaturePython)
  n = 1
  ref = C_element
FEATURE [App::DocumentObjectGroupPython] G4_GRAPHITE_POROUS  # scripted group (container) (typed FeaturePython)
  Dunit = g/cm3
  Dvalue = 1.7
  Group = -> [C_element125]
  conduct = 2
  density = 1
  expand = 3
  formula = G4_GRAPHITE_POROUS
  name = G4_GRAPHITE_POROUS
  specific = 4
FEATURE [App::DocumentObjectGroupPython] H_element116  label="H_element : 0.150"  # scripted group (container) (typed FeaturePython)
  n = 0.080538
FEATURE [App::DocumentObjectGroupPython] C_element126  label="C_element : 0.600"  # scripted group (container) (typed FeaturePython)
  n = 0.599848
FEATURE [App::DocumentObjectGroupPython] O_element108  label="O_element : 0.320"  # scripted group (container) (typed FeaturePython)
  n = 0.319614
FEATURE [App::DocumentObjectGroupPython] G4_LUCITE  # scripted group (container) (typed FeaturePython)
  Dunit = g/cm3
  Dvalue = 1.19
  Group = -> [H_element116,C_element126,O_element108]
  conduct = 2
  density = 1
  expand = 3
  formula = G4_LUCITE
  name = G4_LUCITE
  specific = 4
FEATURE [App::DocumentObjectGroupPython] Cu_element002  label="Cu_element : 62"  # scripted group (container) (typed FeaturePython)
  n = 62
  ref = Cu_element
FEATURE [App::DocumentObjectGroupPython] Zn_element002  label="Zn_element : 35"  # scripted group (container) (typed FeaturePython)
  n = 35
  ref = Zn_element
FEATURE [App::DocumentObjectGroupPython] Pb_element005  label="Pb_element : 3"  # scripted group (container) (typed FeaturePython)
  n = 3
  ref = Pb_element
FEATURE [App::DocumentObjectGroupPython] G4_BRASS  # scripted group (container) (typed FeaturePython)
  Dunit = g/cm3
  Dvalue = 8.52
  Group = -> [Cu_element002,Zn_element002,Pb_element005]
  conduct = 2
  density = 1
  expand = 3
  formula = G4_BRASS
  name = G4_BRASS
  specific = 4
FEATURE [App::DocumentObjectGroupPython] Cu_element003  label="Cu_element : 89"  # scripted group (container) (typed FeaturePython)
  n = 89
  ref = Cu_element
FEATURE [App::DocumentObjectGroupPython] Zn_element003  label="Zn_element : 9"  # scripted group (container) (typed FeaturePython)
  n = 9
  ref = Zn_element
FEATURE [App::DocumentObjectGroupPython] Pb_element006  label="Pb_element : 2"  # scripted group (container) (typed FeaturePython)
  n = 2
  ref = Pb_element
FEATURE [App::DocumentObjectGroupPython] G4_BRONZE  # scripted group (container) (typed FeaturePython)
  Dunit = g/cm3
  Dvalue = 8.82
  Group = -> [Cu_element003,Zn_element003,Pb_element006]
  conduct = 2
  density = 1
  expand = 3
  formula = G4_BRONZE
  name = G4_BRONZE
  specific = 4
FEATURE [App::DocumentObjectGroupPython] Fe_element008  label="Fe_element : 74"  # scripted group (container) (typed FeaturePython)
  n = 74
  ref = Fe_element
FEATURE [App::DocumentObjectGroupPython] Cr_element002  label="Cr_element : 18"  # scripted group (container) (typed FeaturePython)
  n = 18
  ref = Cr_element
FEATURE [App::DocumentObjectGroupPython] Ni_element002  label="Ni_element : 8"  # scripted group (container) (typed FeaturePython)
  n = 8
  ref = Ni_element
FEATURE [App::DocumentObjectGroupPython] G4_STAINLESS_STEEL  label="G4_STAINLESS-STEEL"  # scripted group (container) (typed FeaturePython)
  Dunit = g/cm3
  Dvalue = 8
  Group = -> [Fe_element008,Cr_element002,Ni_element002]
  conduct = 2
  density = 1
  expand = 3
  formula = G4_STAINLESS-STEEL
  name = G4_STAINLESS-STEEL
  specific = 4
FEATURE [App::DocumentObjectGroupPython] H_element117  label="H_element : 065"  # scripted group (container) (typed FeaturePython)
  n = 18
  ref = H_element
FEATURE [App::DocumentObjectGroupPython] C_element127  label="C_element : 072"  # scripted group (container) (typed FeaturePython)
  n = 12
  ref = C_element
FEATURE [App::DocumentObjectGroupPython] O_element109  label="O_element : 062"  # scripted group (container) (typed FeaturePython)
  n = 7
  ref = O_element
FEATURE [App::DocumentObjectGroupPython] G4_CR39  # scripted group (container) (typed FeaturePython)
  Dunit = g/cm3
  Dvalue = 1.32
  Group = -> [H_element117,C_element127,O_element109]
  conduct = 2
  density = 1
  expand = 3
  formula = G4_CR39
  name = G4_CR39
  specific = 4
FEATURE [App::DocumentObjectGroupPython] H_element118  label="H_element : 38"  # scripted group (container) (typed FeaturePython)
  n = 38
  ref = H_element
FEATURE [App::DocumentObjectGroupPython] C_element128  label="C_element : 073"  # scripted group (container) (typed FeaturePython)
  n = 18
  ref = C_element
FEATURE [App::DocumentObjectGroupPython] O_element110  label="O_element : 063"  # scripted group (container) (typed FeaturePython)
  n = 1
  ref = O_element
FEATURE [App::DocumentObjectGroupPython] G4_OCTADECANOL  # scripted group (container) (typed FeaturePython)
  Dunit = g/cm3
  Dvalue = 0.812
  Group = -> [H_element118,C_element128,O_element110]
  conduct = 2
  density = 1
  expand = 3
  formula = G4_OCTADECANOL
  name = G4_OCTADECANOL
  specific = 4
FEATURE [App::DocumentObjectGroupPython] HEP  # scripted group (container) (typed FeaturePython)
  Group = -> [G4_lH2,G4_lN2,G4_lO2,G4_lAr,G4_lBr,G4_lKr,G4_lXe,G4_PbWO4,G4_Galactic,G4_GRAPHITE_POROUS,G4_LUCITE,G4_BRASS,G4_BRONZE,G4_STAINLESS_STEEL,G4_CR39,G4_OCTADECANOL]
FEATURE [App::DocumentObjectGroupPython] C_element129  label="C_element : 074"  # scripted group (container) (typed FeaturePython)
  n = 14
  ref = C_element
FEATURE [App::DocumentObjectGroupPython] H_element119  label="H_element : 066"  # scripted group (container) (typed FeaturePython)
  n = 10
  ref = H_element
FEATURE [App::DocumentObjectGroupPython] O_element111  label="O_element : 064"  # scripted group (container) (typed FeaturePython)
  n = 2
  ref = O_element
FEATURE [App::DocumentObjectGroupPython] N_element050  label="N_element : 023"  # scripted group (container) (typed FeaturePython)
  n = 2
  ref = N_element
FEATURE [App::DocumentObjectGroupPython] G4_KEVLAR  # scripted group (container) (typed FeaturePython)
  Dunit = g/cm3
  Dvalue = 1.44
  Group = -> [C_element129,H_element119,O_element111,N_element050]
  conduct = 2
  density = 1
  expand = 3
  formula = G4_KEVLAR
  name = G4_KEVLAR
  specific = 4
FEATURE [App::DocumentObjectGroupPython] C_element130  label="C_element : 075"  # scripted group (container) (typed FeaturePython)
  n = 10
  ref = C_element
FEATURE [App::DocumentObjectGroupPython] H_element120  label="H_element : 067"  # scripted group (container) (typed FeaturePython)
  n = 8
  ref = H_element
FEATURE [App::DocumentObjectGroupPython] O_element112  label="O_element : 065"  # scripted group (container) (typed FeaturePython)
  n = 4
  ref = O_element
FEATURE [App::DocumentObjectGroupPython] G4_DACRON  # scripted group (container) (typed FeaturePython)
  Dunit = g/cm3
  Dvalue = 1.4
  Group = -> [C_element130,H_element120,O_element112]
  conduct = 2
  density = 1
  expand = 3
  formula = G4_DACRON
  name = G4_DACRON
  specific = 4
FEATURE [App::DocumentObjectGroupPython] C_element131  label="C_element : 076"  # scripted group (container) (typed FeaturePython)
  n = 4
  ref = C_element
FEATURE [App::DocumentObjectGroupPython] H_element121  label="H_element : 068"  # scripted group (container) (typed FeaturePython)
  n = 5
  ref = H_element
FEATURE [App::DocumentObjectGroupPython] Cl_element030  label="Cl_element : 016"  # scripted group (container) (typed FeaturePython)
  n = 1
  ref = Cl_element
FEATURE [App::DocumentObjectGroupPython] G4_NEOPRENE  # scripted group (container) (typed FeaturePython)
  Dunit = g/cm3
  Dvalue = 1.23
  Group = -> [C_element131,H_element121,Cl_element030]
  conduct = 2
  density = 1
  expand = 3
  formula = G4_NEOPRENE
  name = G4_NEOPRENE
  specific = 4
FEATURE [App::DocumentObjectGroupPython] Space  # scripted group (container) (typed FeaturePython)
  Group = -> [G4_KEVLAR,G4_DACRON,G4_NEOPRENE]
FEATURE [App::DocumentObjectGroupPython] H_element122  label="H_element : 069"  # scripted group (container) (typed FeaturePython)
  n = 5
  ref = H_element
FEATURE [App::DocumentObjectGroupPython] C_element132  label="C_element : 077"  # scripted group (container) (typed FeaturePython)
  n = 4
  ref = C_element
FEATURE [App::DocumentObjectGroupPython] N_element051  label="N_element : 3"  # scripted group (container) (typed FeaturePython)
  n = 3
  ref = N_element
FEATURE [App::DocumentObjectGroupPython] O_element113  label="O_element : 066"  # scripted group (container) (typed FeaturePython)
  n = 1
  ref = O_element
FEATURE [App::DocumentObjectGroupPython] G4_CYTOSINE  # scripted group (container) (typed FeaturePython)
  Dunit = g/cm3
  Dvalue = 1.55
  Group = -> [H_element122,C_element132,N_element051,O_element113]
  conduct = 2
  density = 1
  expand = 3
  formula = G4_CYTOSINE
  name = G4_CYTOSINE
  specific = 4
FEATURE [App::DocumentObjectGroupPython] H_element123  label="H_element : 070"  # scripted group (container) (typed FeaturePython)
  n = 6
  ref = H_element
FEATURE [App::DocumentObjectGroupPython] C_element133  label="C_element : 078"  # scripted group (container) (typed FeaturePython)
  n = 5
  ref = C_element
FEATURE [App::DocumentObjectGroupPython] N_element052  label="N_element : 024"  # scripted group (container) (typed FeaturePython)
  n = 2
  ref = N_element
FEATURE [App::DocumentObjectGroupPython] O_element114  label="O_element : 067"  # scripted group (container) (typed FeaturePython)
  n = 2
  ref = O_element
FEATURE [App::DocumentObjectGroupPython] G4_THYMINE  # scripted group (container) (typed FeaturePython)
  Dunit = g/cm3
  Dvalue = 1.23
  Group = -> [H_element123,C_element133,N_element052,O_element114]
  conduct = 2
  density = 1
  expand = 3
  formula = G4_THYMINE
  name = G4_THYMINE
  specific = 4
FEATURE [App::DocumentObjectGroupPython] H_element124  label="H_element : 071"  # scripted group (container) (typed FeaturePython)
  n = 4
  ref = H_element
FEATURE [App::DocumentObjectGroupPython] C_element134  label="C_element : 079"  # scripted group (container) (typed FeaturePython)
  n = 4
  ref = C_element
FEATURE [App::DocumentObjectGroupPython] N_element053  label="N_element : 025"  # scripted group (container) (typed FeaturePython)
  n = 2
  ref = N_element
FEATURE [App::DocumentObjectGroupPython] O_element115  label="O_element : 068"  # scripted group (container) (typed FeaturePython)
  n = 2
  ref = O_element
FEATURE [App::DocumentObjectGroupPython] G4_URACIL  # scripted group (container) (typed FeaturePython)
  Dunit = g/cm3
  Dvalue = 1.32
  Group = -> [H_element124,C_element134,N_element053,O_element115]
  conduct = 2
  density = 1
  expand = 3
  formula = G4_URACIL
  name = G4_URACIL
  specific = 4
FEATURE [App::DocumentObjectGroupPython] H_element125  label="H_element : 072"  # scripted group (container) (typed FeaturePython)
  n = 4
  ref = H_element
FEATURE [App::DocumentObjectGroupPython] C_element135  label="C_element : 080"  # scripted group (container) (typed FeaturePython)
  n = 5
  ref = C_element
FEATURE [App::DocumentObjectGroupPython] N_element054  label="N_element : 026"  # scripted group (container) (typed FeaturePython)
  n = 5
  ref = N_element
FEATURE [App::DocumentObjectGroupPython] G4_DNA_ADENINE  # scripted group (container) (typed FeaturePython)
  Dunit = g/cm3
  Dvalue = 1
  Group = -> [H_element125,C_element135,N_element054]
  conduct = 2
  density = 1
  expand = 3
  formula = G4_DNA_ADENINE
  name = G4_DNA_ADENINE
  specific = 4
FEATURE [App::DocumentObjectGroupPython] H_element126  label="H_element : 073"  # scripted group (container) (typed FeaturePython)
  n = 4
  ref = H_element
FEATURE [App::DocumentObjectGroupPython] C_element136  label="C_element : 081"  # scripted group (container) (typed FeaturePython)
  n = 5
  ref = C_element
FEATURE [App::DocumentObjectGroupPython] N_element055  label="N_element : 027"  # scripted group (container) (typed FeaturePython)
  n = 5
  ref = N_element
FEATURE [App::DocumentObjectGroupPython] O_element116  label="O_element : 069"  # scripted group (container) (typed FeaturePython)
  n = 1
  ref = O_element
FEATURE [App::DocumentObjectGroupPython] G4_DNA_GUANINE  # scripted group (container) (typed FeaturePython)
  Dunit = g/cm3
  Dvalue = 1
  Group = -> [H_element126,C_element136,N_element055,O_element116]
  conduct = 2
  density = 1
  expand = 3
  formula = G4_DNA_GUANINE
  name = G4_DNA_GUANINE
  specific = 4
FEATURE [App::DocumentObjectGroupPython] H_element127  label="H_element : 074"  # scripted group (container) (typed FeaturePython)
  n = 4
  ref = H_element
FEATURE [App::DocumentObjectGroupPython] C_element137  label="C_element : 082"  # scripted group (container) (typed FeaturePython)
  n = 4
  ref = C_element
FEATURE [App::DocumentObjectGroupPython] N_element056  label="N_element : 028"  # scripted group (container) (typed FeaturePython)
  n = 3
  ref = N_element
FEATURE [App::DocumentObjectGroupPython] O_element117  label="O_element : 070"  # scripted group (container) (typed FeaturePython)
  n = 1
  ref = O_element
FEATURE [App::DocumentObjectGroupPython] G4_DNA_CYTOSINE  # scripted group (container) (typed FeaturePython)
  Dunit = g/cm3
  Dvalue = 1
  Group = -> [H_element127,C_element137,N_element056,O_element117]
  conduct = 2
  density = 1
  expand = 3
  formula = G4_DNA_CYTOSINE
  name = G4_DNA_CYTOSINE
  specific = 4
FEATURE [App::DocumentObjectGroupPython] H_element128  label="H_element : 075"  # scripted group (container) (typed FeaturePython)
  n = 5
  ref = H_element
FEATURE [App::DocumentObjectGroupPython] C_element138  label="C_element : 083"  # scripted group (container) (typed FeaturePython)
  n = 5
  ref = C_element
FEATURE [App::DocumentObjectGroupPython] N_element057  label="N_element : 029"  # scripted group (container) (typed FeaturePython)
  n = 2
  ref = N_element
FEATURE [App::DocumentObjectGroupPython] O_element118  label="O_element : 071"  # scripted group (container) (typed FeaturePython)
  n = 2
  ref = O_element
FEATURE [App::DocumentObjectGroupPython] G4_DNA_THYMINE  # scripted group (container) (typed FeaturePython)
  Dunit = g/cm3
  Dvalue = 1
  Group = -> [H_element128,C_element138,N_element057,O_element118]
  conduct = 2
  density = 1
  expand = 3
  formula = G4_DNA_THYMINE
  name = G4_DNA_THYMINE
  specific = 4
FEATURE [App::DocumentObjectGroupPython] H_element129  label="H_element : 076"  # scripted group (container) (typed FeaturePython)
  n = 3
  ref = H_element
FEATURE [App::DocumentObjectGroupPython] C_element139  label="C_element : 084"  # scripted group (container) (typed FeaturePython)
  n = 4
  ref = C_element
FEATURE [App::DocumentObjectGroupPython] N_element058  label="N_element : 030"  # scripted group (container) (typed FeaturePython)
  n = 2
  ref = N_element
FEATURE [App::DocumentObjectGroupPython] O_element119  label="O_element : 072"  # scripted group (container) (typed FeaturePython)
  n = 2
  ref = O_element
FEATURE [App::DocumentObjectGroupPython] G4_DNA_URACIL  # scripted group (container) (typed FeaturePython)
  Dunit = g/cm3
  Dvalue = 1
  Group = -> [H_element129,C_element139,N_element058,O_element119]
  conduct = 2
  density = 1
  expand = 3
  formula = G4_DNA_URACIL
  name = G4_DNA_URACIL
  specific = 4
FEATURE [App::DocumentObjectGroupPython] H_element130  label="H_element : 077"  # scripted group (container) (typed FeaturePython)
  n = 10
  ref = H_element
FEATURE [App::DocumentObjectGroupPython] C_element140  label="C_element : 085"  # scripted group (container) (typed FeaturePython)
  n = 10
  ref = C_element
FEATURE [App::DocumentObjectGroupPython] N_element059  label="N_element : 031"  # scripted group (container) (typed FeaturePython)
  n = 5
  ref = N_element
FEATURE [App::DocumentObjectGroupPython] O_element120  label="O_element : 073"  # scripted group (container) (typed FeaturePython)
  n = 4
  ref = O_element
FEATURE [App::DocumentObjectGroupPython] G4_DNA_ADENOSINE  # scripted group (container) (typed FeaturePython)
  Dunit = g/cm3
  Dvalue = 1
  Group = -> [H_element130,C_element140,N_element059,O_element120]
  conduct = 2
  density = 1
  expand = 3
  formula = G4_DNA_ADENOSINE
  name = G4_DNA_ADENOSINE
  specific = 4
FEATURE [App::DocumentObjectGroupPython] H_element131  label="H_element : 078"  # scripted group (container) (typed FeaturePython)
  n = 10
  ref = H_element
FEATURE [App::DocumentObjectGroupPython] C_element141  label="C_element : 086"  # scripted group (container) (typed FeaturePython)
  n = 10
  ref = C_element
FEATURE [App::DocumentObjectGroupPython] N_element060  label="N_element : 032"  # scripted group (container) (typed FeaturePython)
  n = 5
  ref = N_element
FEATURE [App::DocumentObjectGroupPython] O_element121  label="O_element : 074"  # scripted group (container) (typed FeaturePython)
  n = 5
  ref = O_element
FEATURE [App::DocumentObjectGroupPython] G4_DNA_GUANOSINE  # scripted group (container) (typed FeaturePython)
  Dunit = g/cm3
  Dvalue = 1
  Group = -> [H_element131,C_element141,N_element060,O_element121]
  conduct = 2
  density = 1
  expand = 3
  formula = G4_DNA_GUANOSINE
  name = G4_DNA_GUANOSINE
  specific = 4
FEATURE [App::DocumentObjectGroupPython] H_element132  label="H_element : 079"  # scripted group (container) (typed FeaturePython)
  n = 10
  ref = H_element
FEATURE [App::DocumentObjectGroupPython] C_element142  label="C_element : 087"  # scripted group (container) (typed FeaturePython)
  n = 9
  ref = C_element
FEATURE [App::DocumentObjectGroupPython] N_element061  label="N_element : 033"  # scripted group (container) (typed FeaturePython)
  n = 3
  ref = N_element
FEATURE [App::DocumentObjectGroupPython] O_element122  label="O_element : 075"  # scripted group (container) (typed FeaturePython)
  n = 5
  ref = O_element
FEATURE [App::DocumentObjectGroupPython] G4_DNA_CYTIDINE  # scripted group (container) (typed FeaturePython)
  Dunit = g/cm3
  Dvalue = 1
  Group = -> [H_element132,C_element142,N_element061,O_element122]
  conduct = 2
  density = 1
  expand = 3
  formula = G4_DNA_CYTIDINE
  name = G4_DNA_CYTIDINE
  specific = 4
FEATURE [App::DocumentObjectGroupPython] H_element133  label="H_element : 080"  # scripted group (container) (typed FeaturePython)
  n = 9
  ref = H_element
FEATURE [App::DocumentObjectGroupPython] C_element143  label="C_element : 088"  # scripted group (container) (typed FeaturePython)
  n = 9
  ref = C_element
FEATURE [App::DocumentObjectGroupPython] N_element062  label="N_element : 034"  # scripted group (container) (typed FeaturePython)
  n = 2
  ref = N_element
FEATURE [App::DocumentObjectGroupPython] O_element123  label="O_element : 076"  # scripted group (container) (typed FeaturePython)
  n = 6
  ref = O_element
FEATURE [App::DocumentObjectGroupPython] G4_DNA_URIDINE  # scripted group (container) (typed FeaturePython)
  Dunit = g/cm3
  Dvalue = 1
  Group = -> [H_element133,C_element143,N_element062,O_element123]
  conduct = 2
  density = 1
  expand = 3
  formula = G4_DNA_URIDINE
  name = G4_DNA_URIDINE
  specific = 4
FEATURE [App::DocumentObjectGroupPython] H_element134  label="H_element : 081"  # scripted group (container) (typed FeaturePython)
  n = 11
  ref = H_element
FEATURE [App::DocumentObjectGroupPython] C_element144  label="C_element : 089"  # scripted group (container) (typed FeaturePython)
  n = 10
  ref = C_element
FEATURE [App::DocumentObjectGroupPython] N_element063  label="N_element : 035"  # scripted group (container) (typed FeaturePython)
  n = 2
  ref = N_element
FEATURE [App::DocumentObjectGroupPython] O_element124  label="O_element : 077"  # scripted group (container) (typed FeaturePython)
  n = 6
  ref = O_element
FEATURE [App::DocumentObjectGroupPython] G4_DNA_METHYLURIDINE  # scripted group (container) (typed FeaturePython)
  Dunit = g/cm3
  Dvalue = 1
  Group = -> [H_element134,C_element144,N_element063,O_element124]
  conduct = 2
  density = 1
  expand = 3
  formula = G4_DNA_METHYLURIDINE
  name = G4_DNA_METHYLURIDINE
  specific = 4
FEATURE [App::DocumentObjectGroupPython] P_element014  label="P_element : 003"  # scripted group (container) (typed FeaturePython)
  n = 1
  ref = P_element
FEATURE [App::DocumentObjectGroupPython] O_element125  label="O_element : 078"  # scripted group (container) (typed FeaturePython)
  n = 3
  ref = O_element
FEATURE [App::DocumentObjectGroupPython] G4_DNA_MONOPHOSPHATE  # scripted group (container) (typed FeaturePython)
  Dunit = g/cm3
  Dvalue = 1
  Group = -> [P_element014,O_element125]
  conduct = 2
  density = 1
  expand = 3
  formula = G4_DNA_MONOPHOSPHATE
  name = G4_DNA_MONOPHOSPHATE
  specific = 4
FEATURE [App::DocumentObjectGroupPython] H_element135  label="H_element : 082"  # scripted group (container) (typed FeaturePython)
  n = 10
  ref = H_element
FEATURE [App::DocumentObjectGroupPython] C_element145  label="C_element : 090"  # scripted group (container) (typed FeaturePython)
  n = 10
  ref = C_element
FEATURE [App::DocumentObjectGroupPython] N_element064  label="N_element : 036"  # scripted group (container) (typed FeaturePython)
  n = 5
  ref = N_element
FEATURE [App::DocumentObjectGroupPython] O_element126  label="O_element : 079"  # scripted group (container) (typed FeaturePython)
  n = 7
  ref = O_element
FEATURE [App::DocumentObjectGroupPython] P_element015  label="P_element : 004"  # scripted group (container) (typed FeaturePython)
  n = 1
  ref = P_element
FEATURE [App::DocumentObjectGroupPython] G4_DNA_A  # scripted group (container) (typed FeaturePython)
  Dunit = g/cm3
  Dvalue = 1
  Group = -> [H_element135,C_element145,N_element064,O_element126,P_element015]
  conduct = 2
  density = 1
  expand = 3
  formula = G4_DNA_A
  name = G4_DNA_A
  specific = 4
FEATURE [App::DocumentObjectGroupPython] H_element136  label="H_element : 083"  # scripted group (container) (typed FeaturePython)
  n = 10
  ref = H_element
FEATURE [App::DocumentObjectGroupPython] C_element146  label="C_element : 091"  # scripted group (container) (typed FeaturePython)
  n = 10
  ref = C_element
FEATURE [App::DocumentObjectGroupPython] N_element065  label="N_element : 037"  # scripted group (container) (typed FeaturePython)
  n = 5
  ref = N_element
FEATURE [App::DocumentObjectGroupPython] O_element127  label="O_element : 8"  # scripted group (container) (typed FeaturePython)
  n = 8
  ref = O_element
FEATURE [App::DocumentObjectGroupPython] P_element016  label="P_element : 005"  # scripted group (container) (typed FeaturePython)
  n = 1
  ref = P_element
FEATURE [App::DocumentObjectGroupPython] G4_DNA_G  # scripted group (container) (typed FeaturePython)
  Dunit = g/cm3
  Dvalue = 1
  Group = -> [H_element136,C_element146,N_element065,O_element127,P_element016]
  conduct = 2
  density = 1
  expand = 3
  formula = G4_DNA_G
  name = G4_DNA_G
  specific = 4
FEATURE [App::DocumentObjectGroupPython] H_element137  label="H_element : 084"  # scripted group (container) (typed FeaturePython)
  n = 10
  ref = H_element
FEATURE [App::DocumentObjectGroupPython] C_element147  label="C_element : 092"  # scripted group (container) (typed FeaturePython)
  n = 9
  ref = C_element
FEATURE [App::DocumentObjectGroupPython] N_element066  label="N_element : 038"  # scripted group (container) (typed FeaturePython)
  n = 3
  ref = N_element
FEATURE [App::DocumentObjectGroupPython] O_element128  label="O_element : 080"  # scripted group (container) (typed FeaturePython)
  n = 8
  ref = O_element
FEATURE [App::DocumentObjectGroupPython] P_element017  label="P_element : 006"  # scripted group (container) (typed FeaturePython)
  n = 1
  ref = P_element
FEATURE [App::DocumentObjectGroupPython] G4_DNA_C  # scripted group (container) (typed FeaturePython)
  Dunit = g/cm3
  Dvalue = 1
  Group = -> [H_element137,C_element147,N_element066,O_element128,P_element017]
  conduct = 2
  density = 1
  expand = 3
  formula = G4_DNA_C
  name = G4_DNA_C
  specific = 4
FEATURE [App::DocumentObjectGroupPython] H_element138  label="H_element : 085"  # scripted group (container) (typed FeaturePython)
  n = 9
  ref = H_element
FEATURE [App::DocumentObjectGroupPython] C_element148  label="C_element : 093"  # scripted group (container) (typed FeaturePython)
  n = 9
  ref = C_element
FEATURE [App::DocumentObjectGroupPython] N_element067  label="N_element : 039"  # scripted group (container) (typed FeaturePython)
  n = 2
  ref = N_element
FEATURE [App::DocumentObjectGroupPython] O_element129  label="O_element : 9"  # scripted group (container) (typed FeaturePython)
  n = 9
  ref = O_element
FEATURE [App::DocumentObjectGroupPython] P_element018  label="P_element : 007"  # scripted group (container) (typed FeaturePython)
  n = 1
  ref = P_element
FEATURE [App::DocumentObjectGroupPython] G4_DNA_U  # scripted group (container) (typed FeaturePython)
  Dunit = g/cm3
  Dvalue = 1
  Group = -> [H_element138,C_element148,N_element067,O_element129,P_element018]
  conduct = 2
  density = 1
  expand = 3
  formula = G4_DNA_U
  name = G4_DNA_U
  specific = 4
FEATURE [App::DocumentObjectGroupPython] H_element139  label="H_element : 086"  # scripted group (container) (typed FeaturePython)
  n = 11
  ref = H_element
FEATURE [App::DocumentObjectGroupPython] C_element149  label="C_element : 094"  # scripted group (container) (typed FeaturePython)
  n = 10
  ref = C_element
FEATURE [App::DocumentObjectGroupPython] N_element068  label="N_element : 040"  # scripted group (container) (typed FeaturePython)
  n = 2
  ref = N_element
FEATURE [App::DocumentObjectGroupPython] O_element130  label="O_element : 081"  # scripted group (container) (typed FeaturePython)
  n = 9
  ref = O_element
FEATURE [App::DocumentObjectGroupPython] P_element019  label="P_element : 008"  # scripted group (container) (typed FeaturePython)
  n = 1
  ref = P_element
FEATURE [App::DocumentObjectGroupPython] G4_DNA_MU  # scripted group (container) (typed FeaturePython)
  Dunit = g/cm3
  Dvalue = 1
  Group = -> [H_element139,C_element149,N_element068,O_element130,P_element019]
  conduct = 2
  density = 1
  expand = 3
  formula = G4_DNA_MU
  name = G4_DNA_MU
  specific = 4
FEATURE [App::DocumentObjectGroupPython] BioChemical  # scripted group (container) (typed FeaturePython)
  Group = -> [G4_CYTOSINE,G4_THYMINE,G4_URACIL,G4_DNA_ADENINE,G4_DNA_GUANINE,G4_DNA_CYTOSINE,G4_DNA_THYMINE,G4_DNA_URACIL,G4_DNA_ADENOSINE,G4_DNA_GUANOSINE,G4_DNA_CYTIDINE,G4_DNA_URIDINE,G4_DNA_METHYLURIDINE,G4_DNA_MONOPHOSPHATE,G4_DNA_A,G4_DNA_G,G4_DNA_C,G4_DNA_U,G4_DNA_MU]
FEATURE [App::DocumentObjectGroupPython] G4Materials  # scripted group (container) (typed FeaturePython)
  Group = -> [NIST,Element,HEP,Space,BioChemical]
  version = 1
FEATURE [App::DocumentObjectGroupPython] Geant4  # scripted group (container) (typed FeaturePython)
  Group = -> [G4Isotopes,G4Elements,G4Materials]
FEATURE [App::DocumentObjectGroupPython] Materials  # scripted group (container) (typed FeaturePython)
  Group = -> [Geant4]
FEATURE [Part::FeaturePython] GDMLBox_WorldBox  # WARN: FeaturePython — macro-defined, semantics opaque (R4)
  lunit = 2
  material = 5
  x = 100
  y = 100
  z = 100
FEATURE [Part::FeaturePython] GDMLBox_Box  # WARN: FeaturePython — macro-defined, semantics opaque (R4)
  Placement = pos=(30,0,0) rot=(0,0,1;0rad)
  lunit = 2
  material = 0
  x = 10
  y = 10
  z = 10
FEATURE [Part::FeaturePython] GDMLTorus  # WARN: FeaturePython — macro-defined, semantics opaque (R4)
  Placement = pos=(32,0,16) rot=(0,1,0;1.5708rad)
  aunit = deg
  deltaphi = 360
  lunit = 2
  material = 0
  rmax = 2
  rmin = 0
  rtor = 5
  startphi = 0
FEATURE [Part::MultiFuse] Fusion
  Shapes = -> [GDMLBox_Box,GDMLTorus]
FEATURE [Part::FeaturePython] Array  # Draft array (typed FeaturePython)
  AlwaysSyncPlacement = false
  Angle = 180
  ArrayType = 1
  Axis = (0,0,1)
  Base = -> Fusion
  Center = (0,0,0)
  Count = 5
  ExpandArray = false
  Fuse = false
  IntervalAxis = (0,0,0)
  IntervalX = (50,0,0)
  IntervalY = (0,50,0)
  IntervalZ = (0,0,50)
  NumberCircles = 3
  NumberPolar = 5
  NumberX = 2
  NumberY = 2
  NumberZ = 1
  PlacementList = 5 placements: [(0,0,0),(0,0,0),(0,0,0),(0,0,0),(0,0,0)]
  RadialDistance = 50
  ScaleList = (5) [(1,1,1),(1,1,1),(1,1,1),(1,1,1),(1,1,1)]
  Symmetry = 1
  TangentialDistance = 25
FEATURE [App::Part] Part001
  Group = -> [Array]
  Origin = -> Origin004
FEATURE [App::Part] worldVOL
  Group = -> [GDMLBox_WorldBox,Part001]
  Origin = -> Origin
